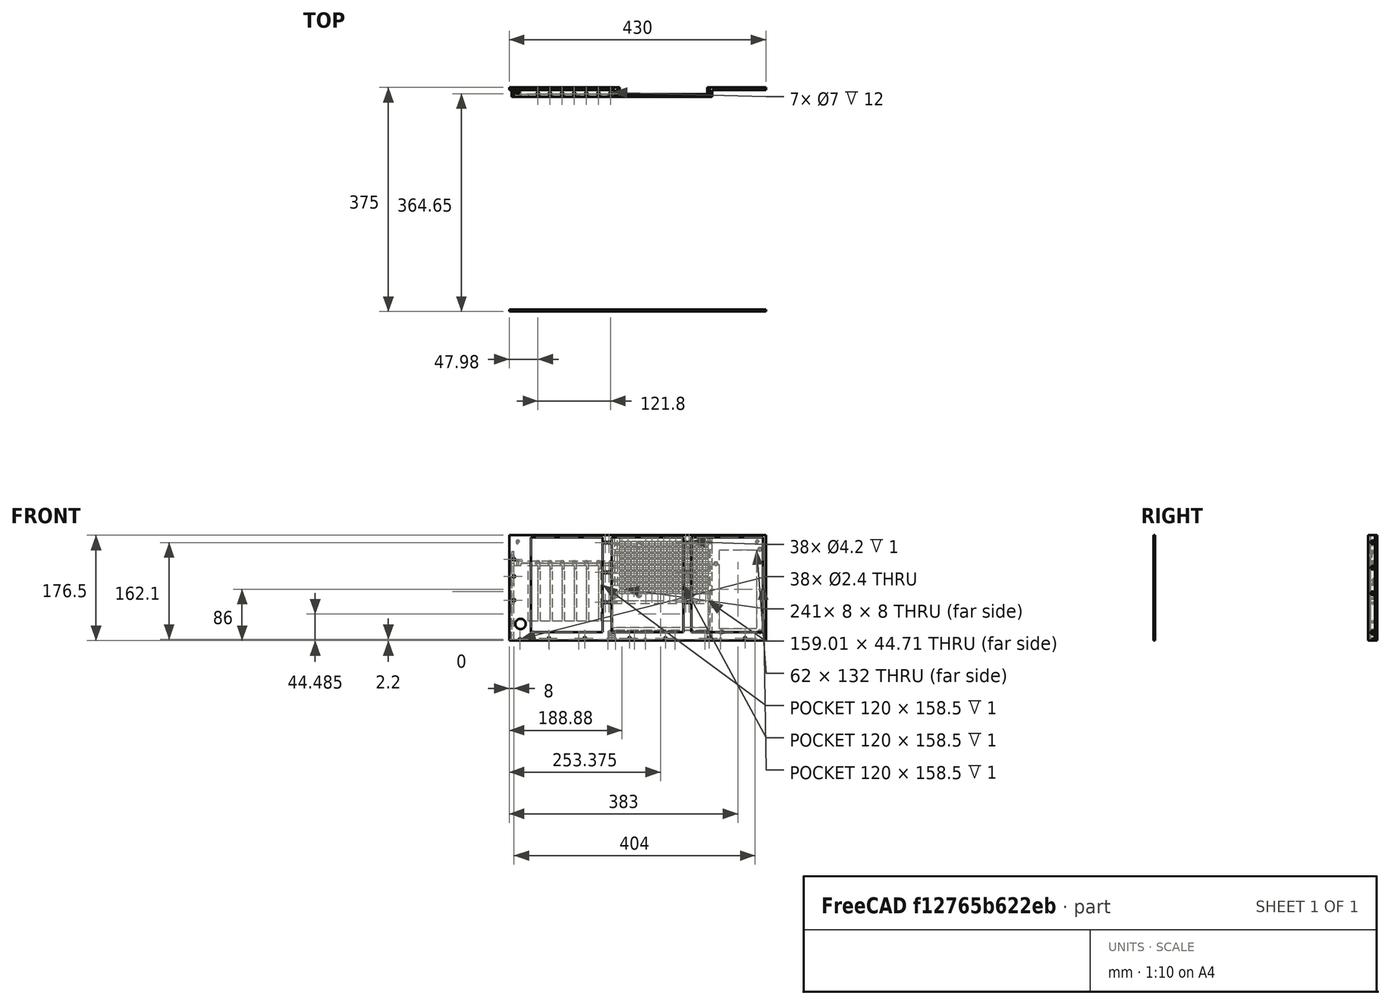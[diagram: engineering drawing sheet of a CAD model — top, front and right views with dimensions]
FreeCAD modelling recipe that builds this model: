
FCSTD DOCUMENT  (FreeCAD 1.0R39109 (Git))
Label: case-wrong-motherboard-height
License: Creative Commons Attribution-NonCommercial-ShareAlike 4.0
LicenseURL: https://creativecommons.org/licenses/by-nc-sa/4.0/
objects: Sketcher::SketchObject×78, Part::FeaturePython×52, PartDesign::Pocket×33, PartDesign::Hole×29, PartDesign::Body×15, PartDesign::FeatureBase×14, PartDesign::Pad×13, Part::Extrusion×11, App::DocumentObjectGroup×10, Part::Part2DObjectPython×6, PartDesign::LinearPattern×2, Spreadsheet::Sheet×1, PartDesign::MultiTransform×1, PartDesign::Fillet×1
note: 502 computed .brp shape members not serialized (recipe doc carries the construction recipe); baked Part::Feature solids carry a one-line shape summary decoded from their .brp

FEATURE [Sketcher::SketchObject] Sketch
  ArcFitTolerance = 1e-06
  AttachmentSupport = -> [XY_Plane]
  FullyConstrained = true
  MakeInternals = false
  MapMode = 5
  expr: Constraints[8] = Spreadsheet.width
  expr: Constraints[9] = Spreadsheet.depth
  sketch-geometry (4):
    g0: LineSegment StartX=-215 StartY=187.5 StartZ=0 EndX=-215 EndY=-187.5 EndZ=0
    g1: LineSegment StartX=-215 StartY=-187.5 StartZ=0 EndX=215 EndY=-187.5 EndZ=0
    g2: LineSegment StartX=215 StartY=-187.5 StartZ=0 EndX=215 EndY=187.5 EndZ=0
    g3: LineSegment StartX=215 StartY=187.5 StartZ=0 EndX=-215 EndY=187.5 EndZ=0
  constraints (11):
    c: Coincident(g0,g1)
    c: Coincident(g1,g2)
    c: Coincident(g2,g3)
    c: Coincident(g3,g0)
    c: Vertical(g0)
    c: Vertical(g2)
    c: Horizontal(g1)
    c: Horizontal(g3)
    c: Distance(g0,g2) = 430
    c: Distance(g1,g3) = 375
    c: Symmetric(g2,g0,g-1)
FEATURE [PartDesign::Pad] Pad  label="bottom"
  Direction = (0,0,1)
  Length = 8
  Length2 = 10
  Profile = -> Sketch
  ReferenceAxis = -> Sketch [N_Axis]
  Refine = true
  Suppressed = false
  Type = 0
  expr: Length = Spreadsheet.bottom_thickness
FEATURE [Spreadsheet::Sheet] Spreadsheet
  cells = A1='Width; B1(width)==430 mm; A2='Depth; B2(depth)==375 mm; A3='Rear wall height; B3(rear_wall_height)==176.5 mm; A4='Side walls height; B4(side_walls_height)==172.5 mm; A5='Front wall height; B5(front_wall_height)==176.5 mm; A6='Bottom thickness; B6(bottom_thickness)==8 mm; A7='Wall thickness; B7(wall_thickness)==4 mm; A8='Front wall thickness; B8(front_wall_thickness)==3 mm; A9='Motherboard left padding; B9(motherboard_left_padding)==6.5 mm; A10='Motherboard right padding; B10(motherboard_right_padding)==6.5 mm; A11='Motherboard front padding; B11(motherboard_front_padding)==6.35 mm; A12='Motherboard rear padding; B12(motherboard_rear_padding)==1.65 mm; A13='Motherboard width; B13(motherboard_width)==305 mm; A14='Motherboard depth; B14(motherboard_depth)==244 mm; A15='Motherboard standoff height; B15(motherboard_standoff_height)==6.5 mm; A16='Side fan thickness; B16(side_fan_thickness)==15 mm; A17='Chassis stiffening ribs height; B17(cChassis_stiffening_ribs_height)==10 mm; A18='PCIE begin; B18(pcie_begin)==160.8 mm; A19='PCIE end; B19(pcie_end)==298.6 mm; A20='PCIE center of first screw; B20(pcie_center_of_first_screw)==144.4 mm; C20='The location of the last PCIE tab screw hole from the left edge of an ATX motherboard; A21='PCIE tab depth; B21(pcie_tab_depth)==11.43 mm; D21='PCI Express™\nCard Electromechanical\nSpecification\nRevision 1.1; E21='Figure 6-4: Standard Add-in Card I/O Bracket; A22='PCIE bracket height; B22(pcie_bracket_height)=93.6; A23='PCIE motherboard thickness; B23(pcie_motherboard_thickness)==1.57 mm; D23='PCI Express™\nCard Electromechanical\nSpecification\nRevision 1.1; A24='PCIE finger bottom to motherboard top; B24(pcie_finger_bottom_to_motherboard_top)==7.9 mm; D24='PCI Express™\nCard Electromechanical\nSpecification\nRevision 1.1; E24='Figure 6-15: Card Assembled in Connector; A25='PCIE finger bottom to mounting tab bottom; B25(pcie_finger_bottom_to_mounting_tab_bottom)==100.36 mm; D25='PCI Express™\nCard Electromechanical\nSpecification\nRevision 1.1; E25='Figure 6-2: Standard Height PCI Express Add-in Card with the I/O Bracket and Card\nRetainer; A26='PCIE opening height from motherboard bottom; B26(pcie_opening_height_from_motherboard_bottom)==pcie_motherboard_thickness + pcie_finger_bottom_to_motherboard_top + pcie_finger_bottom_to_mounting_tab_bottom; C26='calculated; A27='PCIE opening from motherboard bottom; B27(pcie_opening_from_motherboard_bottom)==8.1 mm; A28='PCIE tab bottom padding; B28(pcie_tab_bottom_padding)==0.5 mm; A29='PCIE opening width; B29(pcie_opening_width)==15.9 mm; A30='PCIE spacing; B30(pcie_spacing)==4.4 mm; A31='PCIE opening distance from motherboard edge; B31(pcie_opening_distance_from_motherboard_edge)==6.4 mm; A32='PCIE fastener distance from bracket; B32(pcie_fastener_distance_from_bracket)==5.08 mm; A33='PCIE fastener distance from motherboard edge; B33(pcie_fastener_distance_from_motherboard_edge)==22.48 mm; A34='PCIE fastener spacing; B34(pcie_fastener_spacing)==20.3 mm; A35='IO cutout width; B35(io_cutout_width)==158.75 mm; A36='IO cutout height; B36(io_cutout_height)==44.45 mm; A37='IO cutout keepout zone; B37(io_cutout_keepout_zone)==2.5 mm; A38='IO cutout extra size; B38(io_cutout_extra_size)==0.13 mm; A39='IO cutout bottom to motherboard top; B39(io_cutout_bottom_to_motherboard_top)==3.81 mm; A40='ATX PSU width; B40(atx_psu_width)==150 mm; A41='ATX PSU height; B41(atx_psu_height)==86 mm; A42='ATX PSU depth; B42(atx_psu_depth)==170 mm; A43='Fan mounting hole diameter; B43(fan_mounting_hole_diameter)==4.2 mm; C43='Noctua seems to be using M5 screws which have 4.2. Arctic mentions 4.3. I have seen 4.4 in some drawings. Go figure :p; A44='PCIE mounting hole size; B44(pcie_mounting_hole_size)==3.5 mm; A46='Magnet diameter; B46(magnet_diameter)==6.05 mm; A47='Magnet thickness; B47(magnet_thickness)==3.05 mm; A49='Distance to top support screw; B49(distance_to_top_support_screw)==2.5 + 4 + 3 + 0.5; C49='Distance from the top of the wall to the top support screw
FEATURE [Sketcher::SketchObject] Sketch001
  ArcFitTolerance = 1e-06
  AttachmentSupport = -> [Pad]
  ExternalGeometry = -> [Pad]
  FullyConstrained = true
  MakeInternals = false
  MapMode = 5
  Placement = pos=(0,0,8) rot=(0,0,1;0rad)
  expr: Constraints[13] = Spreadsheet.wall_thickness
  expr: Constraints[14] = Spreadsheet.wall_thickness
  expr: Constraints[16] = Spreadsheet.front_wall_thickness
  expr: Constraints[17] = Spreadsheet.front_wall_thickness
  expr: Constraints[21] = Spreadsheet.wall_thickness
  expr: Constraints[23] = Spreadsheet.wall_thickness
  sketch-geometry (8):
    g0: LineSegment StartX=-215 StartY=183.5 StartZ=0 EndX=-215 EndY=-184.5 EndZ=0
    g1: LineSegment StartX=-215 StartY=-184.5 StartZ=0 EndX=-211 EndY=-184.5 EndZ=0
    g2: LineSegment StartX=-211 StartY=-184.5 StartZ=0 EndX=-211 EndY=183.5 EndZ=0
    g3: LineSegment StartX=-211 StartY=183.5 StartZ=0 EndX=-215 EndY=183.5 EndZ=0
    g4: LineSegment StartX=215 StartY=183.5 StartZ=0 EndX=211 EndY=183.5 EndZ=0
    g5: LineSegment StartX=211 StartY=183.5 StartZ=0 EndX=211 EndY=-184.5 EndZ=0
    g6: LineSegment StartX=211 StartY=-184.5 StartZ=0 EndX=215 EndY=-184.5 EndZ=0
    g7: LineSegment StartX=215 StartY=-184.5 StartZ=0 EndX=215 EndY=183.5 EndZ=0
  constraints (24):
    c: Coincident(g0,g1)
    c: Coincident(g1,g2)
    c: Coincident(g2,g3)
    c: Coincident(g3,g0)
    c: Vertical(g2)
    c: Horizontal(g1)
    c: Horizontal(g3)
    c: Coincident(g5,g6)
    c: Coincident(g6,g7)
    c: Coincident(g7,g4)
    c: Horizontal(g4)
    c: Horizontal(g6)
    c: Vertical(g5)
    c: Distance(g4,g4) = 4
    c: DistanceX(g0,g2) = 4
    c: PointOnObject(g6,g-5)
    c: DistanceY(g-5,g6) = 3
    c: DistanceY(g-4,g0) = 3
    c: PointOnObject(g0,g-4)
    c: Coincident(g4,g5)
    c: PointOnObject(g4,g-5)
    c: DistanceY(g4,g-5) = 4
    c: PointOnObject(g0,g-4)
    c: DistanceY(g0,g-4) = 4
FEATURE [PartDesign::Pad] Pad001  label="side walls"
  BaseFeature = -> Pad
  Direction = (0,0,1)
  Length = 164.5
  Length2 = 10
  Profile = -> Sketch001
  ReferenceAxis = -> Sketch001 [N_Axis]
  Refine = true
  Suppressed = false
  Type = 0
  expr: Length = Spreadsheet.side_walls_height - Spreadsheet.bottom_thickness
FEATURE [Sketcher::SketchObject] Sketch002
  ArcFitTolerance = 1e-06
  AttachmentSupport = -> [Pad001]
  ExternalGeometry = -> [Pad]
  FullyConstrained = true
  MakeInternals = false
  MapMode = 5
  Placement = pos=(0,0,8) rot=(0,0,1;0rad)
  expr: Constraints[16] = Spreadsheet.atx_psu_height + Spreadsheet.wall_thickness + 0.1 mm
  expr: Constraints[17] = Spreadsheet.wall_thickness
  expr: Constraints[22] = Spreadsheet.pcie_tab_depth + Spreadsheet.wall_thickness
  expr: Constraints[6] = Spreadsheet.wall_thickness
  sketch-geometry (8):
    g0: LineSegment StartX=120.9 StartY=176.07 StartZ=0 EndX=-215 EndY=176.07 EndZ=0
    g1: LineSegment StartX=-215 StartY=176.07 StartZ=0 EndX=-215 EndY=172.07 EndZ=0
    g2: LineSegment StartX=-215 StartY=172.07 StartZ=0 EndX=124.9 EndY=172.07 EndZ=0
    g3: LineSegment StartX=124.9 StartY=172.07 StartZ=0 EndX=124.9 EndY=183.5 EndZ=0
    g4: LineSegment StartX=120.9 StartY=176.07 StartZ=0 EndX=120.9 EndY=187.5 EndZ=0
    g5: LineSegment StartX=120.9 StartY=187.5 StartZ=0 EndX=215 EndY=187.5 EndZ=0
    g6: LineSegment StartX=215 StartY=187.5 StartZ=0 EndX=215 EndY=183.5 EndZ=0
    g7: LineSegment StartX=215 StartY=183.5 StartZ=0 EndX=124.9 EndY=183.5 EndZ=0
  constraints (23):
    c: Coincident(g0,g1)
    c: Coincident(g1,g2)
    c: Coincident(g2,g3)
    c: Horizontal(g0)
    c: Horizontal(g2)
    c: Vertical(g1)
    c: DistanceY(g1,g0) = 4
    c: Coincident(g0,g4)
    c: Vertical(g4)
    c: Coincident(g4,g5)
    c: Coincident(g5,g6)
    c: Coincident(g6,g7)
    c: Horizontal(g7)
    c: Coincident(g7,g3)
    c: Vertical(g3)
    c: Equal(g1,g6)
    c: DistanceX(g3,g6) = 90.1
    c: DistanceX(g4,g3) = 4
    c: PointOnObject(g0,g-3)
    c: Horizontal(g5)
    c: Coincident(g5,g-4)
    c: PointOnObject(g6,g-5)
    c: Distance(g2,g-4) = 15.43
FEATURE [PartDesign::Pad] Pad002  label="rear wall"
  BaseFeature = -> Pad001
  Direction = (0,0,1)
  Length = 121.83
  Length2 = 10
  Profile = -> Sketch002
  ReferenceAxis = -> Sketch002 [N_Axis]
  Refine = true
  Suppressed = false
  Type = 0
  expr: Length = Spreadsheet.cChassis_stiffening_ribs_height + Spreadsheet.motherboard_standoff_height + Spreadsheet.pcie_opening_height_from_motherboard_bottom - Spreadsheet.pcie_tab_bottom_padding - Spreadsheet.wall_thickness
FEATURE [Sketcher::SketchObject] Sketch003
  ArcFitTolerance = 1e-06
  AttachmentSupport = -> [Pad002]
  ExternalGeometry = -> [Pad002]
  FullyConstrained = true
  MakeInternals = false
  MapMode = 5
  Placement = pos=(0,0,129.83) rot=(0,0,1;0rad)
  expr: Constraints[9] = Spreadsheet.side_fan_thickness + Spreadsheet.motherboard_left_padding + Spreadsheet.pcie_center_of_first_screw + 2 * Spreadsheet.pcie_mounting_hole_size + Spreadsheet.wall_thickness
  sketch-geometry (7):
    g0: LineSegment StartX=-211 StartY=183.5 StartZ=0 EndX=-211 EndY=172.07 EndZ=0
    g1: LineSegment StartX=-211 StartY=172.07 StartZ=0 EndX=-34.1 EndY=172.07 EndZ=0
    g2: LineSegment StartX=-34.1 StartY=187.5 StartZ=0 EndX=-211 EndY=187.5 EndZ=0
    g3: LineSegment StartX=-34.1 StartY=187.5 StartZ=0 EndX=-34.1 EndY=172.07 EndZ=0
    g4: LineSegment StartX=-215 StartY=183.5 StartZ=0 EndX=-211 EndY=183.5 EndZ=0
    g5: LineSegment StartX=-211 StartY=187.5 StartZ=0 EndX=-215 EndY=187.5 EndZ=0
    g6: LineSegment StartX=-215 StartY=187.5 StartZ=0 EndX=-215 EndY=183.5 EndZ=0
  constraints (17):
    c: Coincident(g0,g1)
    c: Vertical(g0)
    c: Horizontal(g1)
    c: Horizontal(g2)
    c: Coincident(g2,g-3)
    c: PointOnObject(g1,g-4)
    c: Coincident(g3,g2)
    c: Coincident(g3,g1)
    c: Vertical(g3)
    c: DistanceX(g2,g2) = 176.9
    c: Coincident(g5,g6)
    c: Coincident(g6,g4)
    c: Coincident(g4,g-5)
    c: Coincident(g5,g-6)
    c: Coincident(g4,g-5)
    c: Coincident(g0,g4)
    c: Coincident(g2,g5)
FEATURE [PartDesign::Pad] Pad003  label="pcie flange"
  BaseFeature = -> Pad002
  Direction = (0,0,1)
  Length = 4
  Length2 = 10
  Profile = -> Sketch003
  ReferenceAxis = -> Sketch003 [N_Axis]
  Refine = true
  Suppressed = false
  Type = 0
  expr: Length = Spreadsheet.wall_thickness
FEATURE [Sketcher::SketchObject] Sketch004
  ArcFitTolerance = 1e-06
  AttachmentSupport = -> [Pad003]
  ExternalGeometry = -> [Pad003]
  FullyConstrained = true
  MakeInternals = false
  MapMode = 5
  Placement = pos=(0,176.07,0) rot=(0,0.707107,0.707107;3.14159rad)
  expr: Constraints[100] = Spreadsheet.io_cutout_extra_size
  expr: Constraints[106] = Spreadsheet.io_cutout_extra_size
  expr: Constraints[107] = Spreadsheet.io_cutout_extra_size
  expr: Constraints[108] = Spreadsheet.io_cutout_extra_size
  expr: Constraints[118] = Spreadsheet.pcie_opening_from_motherboard_bottom
  expr: Constraints[119] = Spreadsheet.pcie_bracket_height
  expr: Constraints[65] = Spreadsheet.pcie_opening_width
  expr: Constraints[66] = Spreadsheet.pcie_spacing
  expr: Constraints[67] = Spreadsheet.pcie_spacing
  expr: Constraints[68] = Spreadsheet.pcie_spacing
  expr: Constraints[69] = Spreadsheet.pcie_spacing
  expr: Constraints[70] = Spreadsheet.pcie_spacing
  expr: Constraints[71] = Spreadsheet.pcie_spacing
  expr: Constraints[80] = Spreadsheet.io_cutout_width
  expr: Constraints[81] = Spreadsheet.io_cutout_height
  expr: Constraints[82] = Spreadsheet.pcie_spacing
  expr: Constraints[91] = Spreadsheet.motherboard_width
  expr: Constraints[92] = Spreadsheet.pcie_motherboard_thickness
  expr: Constraints[93] = Spreadsheet.cChassis_stiffening_ribs_height + Spreadsheet.motherboard_standoff_height
  expr: Constraints[94] = Spreadsheet.io_cutout_bottom_to_motherboard_top
  expr: Constraints[95] = Spreadsheet.side_fan_thickness + Spreadsheet.motherboard_left_padding
  expr: Constraints[96] = Spreadsheet.pcie_opening_distance_from_motherboard_edge
  sketch-geometry (40):
    g0: LineSegment StartX=167.2 StartY=126.2 StartZ=0 EndX=167.2 EndY=32.6 EndZ=0
    g1: LineSegment StartX=183.1 StartY=32.6 StartZ=0 EndX=183.1 EndY=126.2 EndZ=0
    g2: LineSegment StartX=183.1 StartY=126.2 StartZ=0 EndX=167.2 EndY=126.2 EndZ=0
    g3: LineSegment StartX=146.9 StartY=126.2 StartZ=0 EndX=146.9 EndY=32.6 EndZ=0
    g4: LineSegment StartX=146.9 StartY=32.6 StartZ=0 EndX=162.8 EndY=32.6 EndZ=0
    g5: LineSegment StartX=162.8 StartY=32.6 StartZ=0 EndX=162.8 EndY=126.2 EndZ=0
    g6: LineSegment StartX=162.8 StartY=126.2 StartZ=0 EndX=146.9 EndY=126.2 EndZ=0
    g7: LineSegment StartX=106.3 StartY=126.2 StartZ=0 EndX=106.3 EndY=32.6 EndZ=0
    g8: LineSegment StartX=106.3 StartY=32.6 StartZ=0 EndX=122.2 EndY=32.6 EndZ=0
    g9: LineSegment StartX=122.2 StartY=32.6 StartZ=0 EndX=122.2 EndY=126.2 EndZ=0
    g10: LineSegment StartX=122.2 StartY=126.2 StartZ=0 EndX=106.3 EndY=126.2 EndZ=0
    g11: LineSegment StartX=126.6 StartY=126.2 StartZ=0 EndX=126.6 EndY=32.6 EndZ=0
    g12: LineSegment StartX=126.6 StartY=32.6 StartZ=0 EndX=142.5 EndY=32.6 EndZ=0
    g13: LineSegment StartX=142.5 StartY=32.6 StartZ=0 EndX=142.5 EndY=126.2 EndZ=0
    g14: LineSegment StartX=142.5 StartY=126.2 StartZ=0 EndX=126.6 EndY=126.2 EndZ=0
    g15: LineSegment StartX=101.9 StartY=126.2 StartZ=0 EndX=86 EndY=126.2 EndZ=0
    g16: LineSegment StartX=86 StartY=126.2 StartZ=0 EndX=86 EndY=32.6 EndZ=0
    g17: LineSegment StartX=86 StartY=32.6 StartZ=0 EndX=101.9 EndY=32.6 EndZ=0
    g18: LineSegment StartX=101.9 StartY=32.6 StartZ=0 EndX=101.9 EndY=126.2 EndZ=0
    g19: LineSegment StartX=81.6 StartY=126.2 StartZ=0 EndX=65.7 EndY=126.2 EndZ=0
    g20: LineSegment StartX=65.7 StartY=126.2 StartZ=0 EndX=65.7 EndY=32.6 EndZ=0
    g21: LineSegment StartX=65.7 StartY=32.6 StartZ=0 EndX=81.6 EndY=32.6 EndZ=0
    g22: LineSegment StartX=81.6 StartY=32.6 StartZ=0 EndX=81.6 EndY=126.2 EndZ=0
    g23: LineSegment StartX=61.3 StartY=126.2 StartZ=0 EndX=45.4 EndY=126.2 EndZ=0
    g24: LineSegment StartX=45.4 StartY=126.2 StartZ=0 EndX=45.4 EndY=32.6 EndZ=0
    g25: LineSegment StartX=45.4 StartY=32.6 StartZ=0 EndX=61.3 EndY=32.6 EndZ=0
    g26: LineSegment StartX=61.3 StartY=32.6 StartZ=0 EndX=61.3 EndY=126.2 EndZ=0
    g27: LineSegment [constr] StartX=41 StartY=66.71 StartZ=0 EndX=-117.75 EndY=66.71 EndZ=0
    g28: LineSegment [constr] StartX=-117.75 StartY=66.71 StartZ=0 EndX=-117.75 EndY=22.26 EndZ=0
    g29: LineSegment [constr] StartX=-117.75 StartY=22.26 StartZ=0 EndX=41 EndY=22.26 EndZ=0
    g30: LineSegment [constr] StartX=41 StartY=22.26 StartZ=0 EndX=41 EndY=66.71 EndZ=0
    g31: LineSegment [constr] StartX=-115.5 StartY=26.07 StartZ=0 EndX=-115.5 EndY=24.5 EndZ=0
    g32: LineSegment [constr] StartX=-115.5 StartY=24.5 StartZ=0 EndX=189.5 EndY=24.5 EndZ=0
    g33: LineSegment [constr] StartX=189.5 StartY=24.5 StartZ=0 EndX=189.5 EndY=26.07 EndZ=0
    g34: LineSegment [constr] StartX=189.5 StartY=26.07 StartZ=0 EndX=-115.5 EndY=26.07 EndZ=0
    g35: LineSegment StartX=41.13 StartY=22.13 StartZ=0 EndX=41.13 EndY=66.84 EndZ=0
    g36: LineSegment StartX=41.13 StartY=66.84 StartZ=0 EndX=-117.88 EndY=66.84 EndZ=0
    g37: LineSegment StartX=-117.88 StartY=66.84 StartZ=0 EndX=-117.88 EndY=22.13 EndZ=0
    g38: LineSegment StartX=-117.88 StartY=22.13 StartZ=0 EndX=41.13 EndY=22.13 EndZ=0
    g39: LineSegment StartX=167.2 StartY=32.6 StartZ=0 EndX=183.1 EndY=32.6 EndZ=0
  constraints (120):
    c: Coincident(g1,g2)
    c: Coincident(g2,g0)
    c: Vertical(g0)
    c: Vertical(g1)
    c: Horizontal(g2)
    c: Coincident(g3,g4)
    c: Coincident(g4,g5)
    c: Coincident(g5,g6)
    c: Coincident(g6,g3)
    c: Vertical(g3)
    c: Vertical(g5)
    c: Horizontal(g4)
    c: Horizontal(g6)
    c: Coincident(g7,g8)
    c: Coincident(g8,g9)
    c: Coincident(g9,g10)
    c: Coincident(g10,g7)
    c: Vertical(g7)
    c: Vertical(g9)
    c: Horizontal(g8)
    c: Horizontal(g10)
    c: Coincident(g11,g12)
    c: Coincident(g12,g13)
    c: Coincident(g13,g14)
    c: Coincident(g14,g11)
    c: Vertical(g11)
    c: Vertical(g13)
    c: Horizontal(g12)
    c: Horizontal(g14)
    c: Coincident(g15,g16)
    c: Coincident(g16,g17)
    c: Coincident(g17,g18)
    c: Coincident(g18,g15)
    c: Horizontal(g15)
    c: Horizontal(g17)
    c: Vertical(g16)
    c: Vertical(g18)
    c: Coincident(g19,g20)
    c: Coincident(g20,g21)
    c: Coincident(g21,g22)
    c: Coincident(g22,g19)
    c: Horizontal(g19)
    c: Horizontal(g21)
    c: Vertical(g20)
    c: Vertical(g22)
    c: Coincident(g23,g24)
    c: Coincident(g24,g25)
    c: Coincident(g25,g26)
    c: Coincident(g26,g23)
    c: Horizontal(g23)
    c: Horizontal(g25)
    c: Vertical(g24)
    c: Vertical(g26)
    c: Equal(g2,g6)
    c: Equal(g23,g19)
    c: Equal(g19,g15)
    c: Equal(g15,g10)
    c: Equal(g10,g14)
    c: Equal(g14,g6)
    c: Horizontal(g0,g5)
    c: Horizontal(g3,g13)
    c: Horizontal(g11,g9)
    c: Horizontal(g7,g15)
    c: Horizontal(g15,g19)
    c: Horizontal(g19,g23)
    c: DistanceX(g0,g1) = 15.9
    c: DistanceX(g4,g0) = 4.4
    c: DistanceX(g12,g3) = 4.4
    c: DistanceX(g8,g11) = 4.4
    c: DistanceX(g17,g7) = 4.4
    c: DistanceX(g21,g16) = 4.4
    c: DistanceX(g25,g20) = 4.4
    c: Coincident(g27,g28)
    c: Coincident(g28,g29)
    c: Coincident(g29,g30)
    c: Coincident(g30,g27)
    c: Horizontal(g27)
    c: Horizontal(g29)
    c: Vertical(g28)
    c: Vertical(g30)
    c: DistanceX(g27,g27) = 158.75
    c: DistanceY(g29,g27) = 44.45
    c: DistanceX(g29,g24) = 4.4
    c: Coincident(g31,g32)
    c: Coincident(g32,g33)
    c: Coincident(g33,g34)
    c: Coincident(g34,g31)
    c: Vertical(g31)
    c: Vertical(g33)
    c: Horizontal(g32)
    c: Horizontal(g34)
    c: DistanceX(g31,g33) = 305
    c: DistanceY(g31,g31) = 1.57
    c: Distance(g31,g-4) = 16.5
    c: DistanceY(g28,g31) = 3.81
    c: Distance(g33,g-3) = 21.5
    c: Distance(g33,g1) = 6.4
    c: Parallel(g35,g30)
    c: Parallel(g36,g27)
    c: Parallel(g37,g28)
    c: Distance(g38,g29) = 0.13
    c: Coincident(g37,g38)
    c: Coincident(g36,g37)
    c: Coincident(g35,g38)
    c: Coincident(g35,g36)
    c: Horizontal(g38)
    c: Distance(g27,g36) = 0.13
    c: DistanceX(g36,g27) = 0.13
    c: DistanceX(g29,g35) = 0.13
    c: Coincident(g39,g0)
    c: Coincident(g39,g1)
    c: Horizontal(g39)
    c: Horizontal(g0,g4)
    c: Horizontal(g3,g12)
    c: Horizontal(g11,g8)
    c: Horizontal(g7,g17)
    c: Horizontal(g16,g21)
    c: Horizontal(g20,g25)
    c: Distance(g32,g39) = 8.1
    c: DistanceY(g1,g1) = 93.6
FEATURE [PartDesign::Pocket] Pocket  label="rear cutouts"
  BaseFeature = -> Pad003
  Direction = (0,-1,2e-16)
  Length = 4
  Length2 = 5
  Profile = -> Sketch004
  ReferenceAxis = -> Sketch004 [N_Axis]
  Refine = true
  Suppressed = false
  Type = 0
  expr: Length = Spreadsheet.wall_thickness
FEATURE [Sketcher::SketchObject] Sketch005
  ArcFitTolerance = 1e-06
  AttachmentSupport = -> [Pad002]
  FullyConstrained = true
  MakeInternals = false
  MapMode = 5
  Placement = pos=(0,187.5,0) rot=(0,0.707107,0.707107;3.14159rad)
  sketch-geometry (12):
    g0: LineSegment [constr] StartX=-125 StartY=158 StartZ=0 EndX=-211 EndY=158 EndZ=0
    g1: LineSegment [constr] StartX=-211 StartY=158 StartZ=0 EndX=-211 EndY=8 EndZ=0
    g2: LineSegment [constr] StartX=-211 StartY=8 StartZ=0 EndX=-125 EndY=8 EndZ=0
    g3: LineSegment [constr] StartX=-125 StartY=8 StartZ=0 EndX=-125 EndY=158 EndZ=0
    g4: Circle CenterX=-205 CenterY=152 CenterZ=0 NormalX=0 NormalY=0 NormalZ=1 AngleXU=0 Radius=1.7525
    g5: Circle CenterX=-131 CenterY=128 CenterZ=0 NormalX=0 NormalY=0 NormalZ=1 AngleXU=0 Radius=1.7525
    g6: Circle CenterX=-205 CenterY=14 CenterZ=0 NormalX=0 NormalY=0 NormalZ=1 AngleXU=0 Radius=1.7525
    g7: Circle CenterX=-141 CenterY=14 CenterZ=0 NormalX=0 NormalY=0 NormalZ=1 AngleXU=0 Radius=1.7525
    g8: LineSegment StartX=-199 StartY=152 StartZ=0 EndX=-199 EndY=20 EndZ=0
    g9: LineSegment StartX=-199 StartY=20 StartZ=0 EndX=-137 EndY=20 EndZ=0
    g10: LineSegment StartX=-137 StartY=20 StartZ=0 EndX=-137 EndY=152 EndZ=0
    g11: LineSegment StartX=-137 StartY=152 StartZ=0 EndX=-199 EndY=152 EndZ=0
  constraints (35):
    c: Coincident(g0,g1)
    c: Coincident(g1,g2)
    c: Coincident(g2,g3)
    c: Coincident(g3,g0)
    c: Horizontal(g0)
    c: Horizontal(g2)
    c: Vertical(g1)
    c: Vertical(g3)
    c: DistanceX(g0,g0) = 86
    c: Distance(g0,g1) = 150
    c: DistanceY(g6,g4) = 138
    c: DistanceY(g7,g5) = 114
    c: DistanceX(g6,g7) = 64
    c: Horizontal(g7,g6)
    c: Vertical(g4,g6)
    c: Coincident(g1,g-4)
    c: DistanceY(g2,g7) = 6
    c: Distance(g7,g3) = 16
    c: Distance(g5,g3) = 6
    c: Diameter(g7) = 3.505
    c: Equal(g7,g6)
    c: Equal(g6,g4)
    c: Equal(g4,g5)
    c: Coincident(g8,g9)
    c: Coincident(g9,g10)
    c: Coincident(g10,g11)
    c: Coincident(g11,g8)
    c: Vertical(g8)
    c: Vertical(g10)
    c: Horizontal(g9)
    c: Horizontal(g11)
    c: Distance(g0,g11) = 6
    c: Distance(g8,g1) = 12
    c: Distance(g3,g10) = 12
    c: Distance(g2,g9) = 12
FEATURE [Sketcher::SketchObject] Sketch006
  ArcFitTolerance = 1e-06
  AttachmentSupport = -> [Pocket]
  ExternalGeometry = -> [Pocket,Pad003]
  FullyConstrained = true
  MakeInternals = false
  MapMode = 5
  Placement = pos=(0,0,133.83) rot=(0,0,1;0rad)
  expr: Constraints[10] = Spreadsheet.wall_thickness
  sketch-geometry (12):
    g0: LineSegment StartX=-215 StartY=187.5 StartZ=0 EndX=-215 EndY=183.5 EndZ=0
    g1: LineSegment StartX=-215 StartY=183.5 StartZ=0 EndX=-38.1 EndY=183.5 EndZ=0
    g2: LineSegment StartX=-38.1 StartY=172.07 StartZ=0 EndX=124.9 EndY=172.07 EndZ=0
    g3: LineSegment StartX=124.9 StartY=172.07 StartZ=0 EndX=124.9 EndY=183.5 EndZ=0
    g4: LineSegment StartX=120.9 StartY=176.07 StartZ=0 EndX=-34.1 EndY=176.07 EndZ=0
    g5: LineSegment StartX=-38.1 StartY=183.5 StartZ=0 EndX=-38.1 EndY=172.07 EndZ=0
    g6: LineSegment StartX=-34.1 StartY=176.07 StartZ=0 EndX=-34.1 EndY=187.5 EndZ=0
    g7: LineSegment StartX=120.9 StartY=176.07 StartZ=0 EndX=120.9 EndY=187.5 EndZ=0
    g8: LineSegment StartX=120.9 StartY=187.5 StartZ=0 EndX=215 EndY=187.5 EndZ=0
    g9: LineSegment StartX=215 StartY=187.5 StartZ=0 EndX=215 EndY=183.5 EndZ=0
    g10: LineSegment StartX=215 StartY=183.5 StartZ=0 EndX=124.9 EndY=183.5 EndZ=0
    g11: LineSegment StartX=-215 StartY=187.5 StartZ=0 EndX=-34.1 EndY=187.5 EndZ=0
  constraints (28):
    c: Coincident(g0,g1)
    c: Horizontal(g1)
    c: Coincident(g2,g3)
    c: Horizontal(g2)
    c: Horizontal(g4)
    c: Coincident(g1,g5)
    c: Vertical(g5)
    c: Coincident(g4,g6)
    c: Vertical(g6)
    c: Coincident(g2,g5)
    c: Distance(g5,g6) = 4
    c: Coincident(g-4,g4)
    c: Coincident(g-5,g2)
    c: Coincident(g3,g-5)
    c: Coincident(g4,g7)
    c: Coincident(g7,g-4)
    c: Coincident(g7,g8)
    c: Coincident(g8,g9)
    c: Coincident(g9,g-6)
    c: Coincident(g9,g10)
    c: Coincident(g10,g3)
    c: Vertical(g9)
    c: Horizontal(g8)
    c: Coincident(g11,g-7)
    c: Coincident(g11,g6)
    c: Coincident(g11,g0)
    c: Coincident(g0,g-8)
    c: Coincident(g-7,g6)
FEATURE [PartDesign::Pad] Pad004  label="rear wall top part"
  BaseFeature = -> Pocket
  Direction = (0,0,1)
  Length = 42.67
  Length2 = 4
  Profile = -> Sketch006
  ReferenceAxis = -> Sketch006 [N_Axis]
  Refine = true
  Suppressed = false
  Type = 4
  expr: Length = Spreadsheet.rear_wall_height - Spreadsheet.cChassis_stiffening_ribs_height - Spreadsheet.motherboard_standoff_height - Spreadsheet.pcie_opening_height_from_motherboard_bottom + Spreadsheet.pcie_tab_bottom_padding - 2 * Spreadsheet.wall_thickness
  expr: Length2 = <<pcie flange>>.Length
FEATURE [Sketcher::SketchObject] Sketch008
  ArcFitTolerance = 1e-06
  FullyConstrained = true
  MakeInternals = false
  MapMode = 5
  Placement = pos=(0,0,8) rot=(0,0,1;0rad)
  expr: Constraints[10] = Spreadsheet.motherboard_depth
  expr: Constraints[11] = Spreadsheet.motherboard_rear_padding
  expr: Constraints[8] = Spreadsheet.motherboard_width
  expr: Constraints[9] = Spreadsheet.side_fan_thickness + Spreadsheet.motherboard_left_padding
  sketch-geometry (16):
    g0: LineSegment StartX=-189.5 StartY=170.42 StartZ=0 EndX=-189.5 EndY=-73.58 EndZ=0
    g1: LineSegment StartX=-189.5 StartY=-73.58 StartZ=0 EndX=115.5 EndY=-73.58 EndZ=0
    g2: LineSegment StartX=115.5 StartY=-73.58 StartZ=0 EndX=115.5 EndY=170.42 EndZ=0
    g3: LineSegment StartX=115.5 StartY=170.42 StartZ=0 EndX=-189.5 EndY=170.42 EndZ=0
    g4: Circle CenterX=-172.8 CenterY=160.22 CenterZ=0 NormalX=0 NormalY=0 NormalZ=1 AngleXU=0 Radius=1.55
    g5: Circle CenterX=-94.1 CenterY=160.22 CenterZ=0 NormalX=0 NormalY=0 NormalZ=1 AngleXU=0 Radius=1.55
    g6: Circle CenterX=-48.3 CenterY=160.22 CenterZ=0 NormalX=0 NormalY=0 NormalZ=1 AngleXU=0 Radius=1.55
    g7: Circle CenterX=109.1 CenterY=137.42 CenterZ=0 NormalX=0 NormalY=0 NormalZ=1 AngleXU=0 Radius=1.55
    g8: Circle CenterX=-172.8 CenterY=5.32 CenterZ=0 NormalX=0 NormalY=0 NormalZ=1 AngleXU=0 Radius=1.55
    g9: Circle CenterX=-114.4 CenterY=5.32 CenterZ=0 NormalX=0 NormalY=0 NormalZ=1 AngleXU=0 Radius=1.55
    g10: Circle CenterX=-94.1 CenterY=5.32 CenterZ=0 NormalX=0 NormalY=0 NormalZ=1 AngleXU=0 Radius=1.55
    g11: Circle CenterX=-48.3 CenterY=5.32 CenterZ=0 NormalX=0 NormalY=0 NormalZ=1 AngleXU=0 Radius=1.55
    g12: Circle CenterX=109.1 CenterY=5.32 CenterZ=0 NormalX=0 NormalY=0 NormalZ=1 AngleXU=0 Radius=1.55
    g13: Circle CenterX=109.1 CenterY=-67.08 CenterZ=0 NormalX=0 NormalY=0 NormalZ=1 AngleXU=0 Radius=1.55
    g14: Circle CenterX=-172.8 CenterY=-67.08 CenterZ=0 NormalX=0 NormalY=0 NormalZ=1 AngleXU=0 Radius=1.55
    g15: Circle CenterX=-48.3 CenterY=-67.08 CenterZ=0 NormalX=0 NormalY=0 NormalZ=1 AngleXU=0 Radius=1.55
  constraints (48):
    c: Coincident(g0,g1)
    c: Coincident(g1,g2)
    c: Coincident(g2,g3)
    c: Coincident(g3,g0)
    c: Vertical(g0)
    c: Vertical(g2)
    c: Horizontal(g1)
    c: Horizontal(g3)
    c: DistanceX(g0,g2) = 305
    c: Distance(g-3,g0) = 21.5
    c: Distance(g1,g3) = 244
    c: Distance(g0,g-4) = 1.65
    c: Horizontal(g13,g15)
    c: Horizontal(g15,g14)
    c: Horizontal(g12,g11)
    c: Horizontal(g11,g10)
    c: Horizontal(g10,g9)
    c: Horizontal(g9,g8)
    c: Horizontal(g6,g5)
    c: Horizontal(g5,g4)
    c: Vertical(g4,g8)
    c: Vertical(g8,g14)
    c: Vertical(g5,g10)
    c: Vertical(g6,g11)
    c: Vertical(g11,g15)
    c: Vertical(g7,g12)
    c: Vertical(g12,g13)
    c: Equal(g4,g5)
    c: Equal(g5,g6)
    c: Equal(g6,g7)
    c: Equal(g7,g12)
    c: Equal(g12,g11)
    c: Equal(g11,g10)
    c: Equal(g10,g9)
    c: Equal(g9,g8)
    c: Equal(g8,g14)
    c: Equal(g14,g15)
    c: Equal(g15,g13)
    c: Diameter(g4) = 3.1
    c: Distance(g6,g3) = 10.2
    c: Distance(g7,g3) = 33
    c: Distance(g12,g3) = 165.1
    c: Distance(g13,g3) = 237.5
    c: Distance(g13,g2) = 6.4
    c: Distance(g15,g2) = 163.8
    c: Distance(g10,g2) = 209.6
    c: Distance(g9,g2) = 229.9
    c: Distance(g4,g2) = 288.3
FEATURE [Sketcher::SketchObject] Sketch011
  ArcFitTolerance = 1e-06
  FullyConstrained = true
  MakeInternals = false
  MapMode = 5
  Placement = pos=(0,0,133.83) rot=(0,0,1;0rad)
  expr: Constraints[11] = Spreadsheet.pcie_fastener_spacing
  expr: Constraints[12] = Spreadsheet.pcie_fastener_spacing
  expr: Constraints[13] = Spreadsheet.pcie_fastener_spacing
  expr: Constraints[14] = Spreadsheet.pcie_fastener_spacing
  expr: Constraints[15] = Spreadsheet.pcie_fastener_spacing
  expr: Constraints[17] = Spreadsheet.pcie_fastener_spacing
  expr: Constraints[24] = Spreadsheet.pcie_mounting_hole_size
  expr: Constraints[2] = Spreadsheet.pcie_fastener_distance_from_bracket
  expr: Constraints[5] = Spreadsheet.side_fan_thickness + Spreadsheet.motherboard_left_padding + Spreadsheet.pcie_fastener_distance_from_motherboard_edge
  sketch-geometry (8):
    g0: LineSegment [constr] StartX=-211 StartY=177.15 StartZ=0 EndX=-45 EndY=177.15 EndZ=0
    g1: Circle CenterX=-167.02 CenterY=177.15 CenterZ=0 NormalX=0 NormalY=0 NormalZ=1 AngleXU=0 Radius=1.75
    g2: Circle CenterX=-146.72 CenterY=177.15 CenterZ=0 NormalX=0 NormalY=0 NormalZ=1 AngleXU=0 Radius=1.75
    g3: Circle CenterX=-126.42 CenterY=177.15 CenterZ=0 NormalX=0 NormalY=0 NormalZ=1 AngleXU=0 Radius=1.75
    g4: Circle CenterX=-106.12 CenterY=177.15 CenterZ=0 NormalX=0 NormalY=0 NormalZ=1 AngleXU=0 Radius=1.75
    g5: Circle CenterX=-85.82 CenterY=177.15 CenterZ=0 NormalX=0 NormalY=0 NormalZ=1 AngleXU=0 Radius=1.75
    g6: Circle CenterX=-65.52 CenterY=177.15 CenterZ=0 NormalX=0 NormalY=0 NormalZ=1 AngleXU=0 Radius=1.75
    g7: Circle CenterX=-45.22 CenterY=177.15 CenterZ=0 NormalX=0 NormalY=0 NormalZ=1 AngleXU=0 Radius=1.75
  constraints (25):
    c: Horizontal(g0)
    c: PointOnObject(g0,g-4)
    c: Distance(g-3,g0) = 5.08
    c: PointOnObject(g0,g-3)
    c: PointOnObject(g1,g0)
    c: DistanceX(g0,g1) = 43.98
    c: PointOnObject(g2,g0)
    c: PointOnObject(g3,g0)
    c: PointOnObject(g4,g0)
    c: PointOnObject(g5,g0)
    c: PointOnObject(g6,g0)
    c: DistanceX(g1,g2) = 20.3
    c: Distance(g2,g3) = 20.3
    c: DistanceX(g5,g6) = 20.3
    c: DistanceX(g3,g4) = 20.3
    c: DistanceX(g4,g5) = 20.3
    c: PointOnObject(g7,g0)
    c: DistanceX(g6,g7) = 20.3
    c: Equal(g1,g2)
    c: Equal(g2,g3)
    c: Equal(g3,g4)
    c: Equal(g4,g5)
    c: Equal(g5,g6)
    c: Equal(g6,g7)
    c: Diameter(g1) = 3.5
FEATURE [Sketcher::SketchObject] Sketch020
  ArcFitTolerance = 1e-06
  FullyConstrained = true
  MakeInternals = false
  MapMode = 5
  Placement = pos=(215,0,0) rot=(0.57735,0.57735,0.57735;2.0944rad)
  sketch-geometry (4):
    g0: LineSegment StartX=162.07 StartY=156 StartZ=0 EndX=32.07 EndY=156 EndZ=0
    g1: LineSegment StartX=32.07 StartY=156 StartZ=0 EndX=32.07 EndY=10 EndZ=0
    g2: LineSegment StartX=32.07 StartY=10 StartZ=0 EndX=162.07 EndY=10 EndZ=0
    g3: LineSegment StartX=162.07 StartY=10 StartZ=0 EndX=162.07 EndY=156 EndZ=0
  constraints (12):
    c: Coincident(g0,g1)
    c: Coincident(g1,g2)
    c: Coincident(g2,g3)
    c: Coincident(g3,g0)
    c: Horizontal(g0)
    c: Horizontal(g2)
    c: Vertical(g1)
    c: Vertical(g3)
    c: DistanceY(g2,g0) = 146
    c: DistanceX(g0,g0) = 130
    c: DistanceX(g2,g-4) = 10
    c: DistanceY(g-4,g2) = 2
FEATURE [Part::Part2DObjectPython] ShapeString  label="ATX only"  # Draft 2D object (typed FeaturePython)
  FontFile = <path>
  Fuse = false
  Justification = 6
  JustificationReference = 0
  KeepLeftMargin = false
  MakeFace = true
  ObliqueAngle = 0
  Placement = pos=(-167.8,152.22,8) rot=(0,0,1;0rad)
  ScaleToSize = true
  Size = 10
  String = A
  Tracking = 0
FEATURE [Part::Part2DObjectPython] ShapeString001  label="ATX only001"  # Draft 2D object (typed FeaturePython)
  FontFile = <path>
  Fuse = false
  Justification = 6
  JustificationReference = 0
  KeepLeftMargin = false
  MakeFace = true
  ObliqueAngle = 0
  Placement = pos=(-165.8,-0.68,8) rot=(0,0,1;0rad)
  ScaleToSize = true
  Size = 10
  String = A
  Tracking = 0
FEATURE [Part::Part2DObjectPython] ShapeString002  label="ATX only002"  # Draft 2D object (typed FeaturePython)
  FontFile = <path>
  Fuse = false
  Justification = 6
  JustificationReference = 0
  KeepLeftMargin = false
  MakeFace = true
  ObliqueAngle = 0
  Placement = pos=(-165.8,-72.08,8) rot=(0,0,1;0rad)
  ScaleToSize = true
  Size = 10
  String = A
  Tracking = 0
FEATURE [Part::Part2DObjectPython] ShapeString003  label="mATX only"  # Draft 2D object (typed FeaturePython)
  FontFile = <path>
  Fuse = false
  Justification = 6
  JustificationReference = 0
  KeepLeftMargin = false
  MakeFace = true
  ObliqueAngle = 0
  Placement = pos=(-96.1,143.22,8) rot=(0,0,1;0rad)
  ScaleToSize = true
  Size = 10
  String = M
  Tracking = 0
FEATURE [Part::Part2DObjectPython] ShapeString004  label="mATX only001"  # Draft 2D object (typed FeaturePython)
  FontFile = <path>
  Fuse = false
  Justification = 6
  JustificationReference = 0
  KeepLeftMargin = false
  MakeFace = true
  ObliqueAngle = 0
  Placement = pos=(-119.4,-11.68,8) rot=(0,0,1;0rad)
  ScaleToSize = true
  Size = 10
  String = M
  Tracking = 0
FEATURE [Part::Part2DObjectPython] ShapeString005  label="mATX only002"  # Draft 2D object (typed FeaturePython)
  FontFile = <path>
  Fuse = false
  Justification = 6
  JustificationReference = 0
  KeepLeftMargin = false
  MakeFace = true
  ObliqueAngle = 0
  Placement = pos=(-99.1,-11.68,8) rot=(0,0,1;0rad)
  ScaleToSize = true
  Size = 10
  String = M
  Tracking = 0
FEATURE [PartDesign::Pocket] Pocket001  label="PSU cutout"
  BaseFeature = -> Pad004
  Direction = (0,-1,2e-16)
  Length = 4
  Length2 = 5
  Profile = -> Sketch005
  ReferenceAxis = -> Sketch005 [N_Axis]
  Refine = true
  Suppressed = false
  Type = 0
  expr: Length = Spreadsheet.wall_thickness
FEATURE [Sketcher::SketchObject] Sketch009
  ArcFitTolerance = 1e-06
  ExternalGeometry = -> [Pocket001]
  FullyConstrained = true
  MakeInternals = false
  MapMode = 5
  Placement = pos=(0,0,8) rot=(0,0,1;0rad)
  expr: Constraints[7] = Spreadsheet.front_wall_thickness
  sketch-geometry (4):
    g0: LineSegment StartX=-215 StartY=-187.5 StartZ=0 EndX=215 EndY=-187.5 EndZ=0
    g1: LineSegment StartX=215 StartY=-187.5 StartZ=0 EndX=215 EndY=-184.5 EndZ=0
    g2: LineSegment StartX=215 StartY=-184.5 StartZ=0 EndX=-215 EndY=-184.5 EndZ=0
    g3: LineSegment StartX=-215 StartY=-184.5 StartZ=0 EndX=-215 EndY=-187.5 EndZ=0
  constraints (10):
    c: Horizontal(g2)
    c: Vertical(g1)
    c: Vertical(g3)
    c: Coincident(g3,g2)
    c: Coincident(g3,g0)
    c: Coincident(g1,g0)
    c: Coincident(g2,g1)
    c: DistanceY(g0,g1) = 3
    c: Coincident(g0,g-5)
    c: Coincident(g0,g-6)
FEATURE [PartDesign::Pad] Pad006  label="front wall"
  BaseFeature = -> Pocket001
  Direction = (0,0,1)
  Length = 168.5
  Length2 = 10
  Profile = -> Sketch009
  ReferenceAxis = -> Sketch009 [N_Axis]
  Refine = true
  Suppressed = false
  Type = 0
  expr: Length = Spreadsheet.front_wall_height - Spreadsheet.bottom_thickness
FEATURE [PartDesign::Pocket] Pocket003  label="pcie fasteners"
  BaseFeature = -> Pad006
  Direction = (0,0,-1)
  Length = 8
  Length2 = 5
  Profile = -> Sketch011
  ReferenceAxis = -> Sketch011 [N_Axis]
  Refine = true
  Suppressed = false
  Type = 0
  expr: Length = Spreadsheet.wall_thickness * 2
FEATURE [Sketcher::SketchObject] Sketch016
  ArcFitTolerance = 1e-06
  ExternalGeometry = -> [Pocket003]
  FullyConstrained = true
  MakeInternals = false
  MapMode = 5
  Placement = pos=(0,176.07,0) rot=(0,0.707107,0.707107;3.14159rad)
  sketch-geometry (4):
    g0: LineSegment StartX=-117.88 StartY=166.5 StartZ=0 EndX=-117.88 EndY=158.5 EndZ=0
    g1: LineSegment StartX=-117.88 StartY=158.5 StartZ=0 EndX=-109.88 EndY=158.5 EndZ=0
    g2: LineSegment StartX=-109.88 StartY=158.5 StartZ=0 EndX=-109.88 EndY=166.5 EndZ=0
    g3: LineSegment StartX=-109.88 StartY=166.5 StartZ=0 EndX=-117.88 EndY=166.5 EndZ=0
  constraints (12):
    c: Coincident(g0,g1)
    c: Coincident(g1,g2)
    c: Coincident(g2,g3)
    c: Coincident(g3,g0)
    c: Vertical(g0)
    c: Vertical(g2)
    c: Horizontal(g1)
    c: Horizontal(g3)
    c: Distance(g0,g2) = 8
    c: Distance(g1,g3) = 8
    c: Vertical(g0,g-3)
    c: Distance(g2,g-4) = 10
FEATURE [PartDesign::Pocket] Pocket007  label="rear ventilation template"
  BaseFeature = -> Pocket003
  Direction = (-1e-16,-1,2e-16)
  Length = 4
  Length2 = 5
  Profile = -> Sketch016
  ReferenceAxis = -> Sketch016 [N_Axis]
  Refine = true
  Suppressed = false
  Type = 0
  expr: Length = Spreadsheet.wall_thickness
FEATURE [PartDesign::LinearPattern] LinearPattern
  Direction = -> Sketch016 [H_Axis]
  Length = 140
  Mode = 1
  Occurrences = 15
  Offset = 10
  Refine = true
  Suppressed = false
  TransformMode = 0
FEATURE [PartDesign::LinearPattern] LinearPattern004
  Direction = -> Sketch016 [V_Axis]
  Length = 80
  Mode = 1
  Occurrences = 9
  Offset = 10
  Refine = true
  Reversed = true
  Suppressed = false
  TransformMode = 0
FEATURE [PartDesign::MultiTransform] MultiTransform  label="rear ventilation"
  BaseFeature = -> Pocket007
  Originals = -> [Pocket007]
  Refine = true
  Suppressed = false
  TransformMode = 0
  Transformations = -> [LinearPattern,LinearPattern004]
FEATURE [PartDesign::Hole] Hole  label="motherboard standoff holes"
  BaseFeature = -> MultiTransform
  CustomThreadClearance = 0
  Depth = 1205.5
  DepthType = 1
  Diameter = 3.4
  DrillForDepth = false
  DrillPoint = 1
  DrillPointAngle = 118
  HoleCutCountersinkAngle = 90
  HoleCutCustomValues = false
  HoleCutDepth = 0
  HoleCutDiameter = 6.1
  HoleCutType = 0
  ModelThread = false
  Profile = -> Sketch008
  Refine = true
  Suppressed = false
  Tapered = false
  TaperedAngle = 90
  ThreadClass = 0
  ThreadDepth = 1205.5
  ThreadDepthType = 0
  ThreadDirection = 0
  ThreadFit = 0
  ThreadSize = 9
  ThreadType = 1
  Threaded = false
  UseCustomThreadClearance = false
FEATURE [Sketcher::SketchObject] Sketch021
  ArcFitTolerance = 1e-06
  ExternalGeometry = -> [Sketch008,Hole]
  FullyConstrained = true
  MakeInternals = false
  MapMode = 5
  Placement = pos=(0,0,8) rot=(0,0,1;0rad)
  expr: Constraints[8] = Spreadsheet.motherboard_front_padding
  sketch-geometry (24):
    g0: LineSegment StartX=-43.4 StartY=-79.93 StartZ=0 EndX=-43.4 EndY=-84.93 EndZ=0
    g1: LineSegment StartX=-43.4 StartY=-84.93 StartZ=0 EndX=76.6 EndY=-84.93 EndZ=0
    g2: LineSegment StartX=76.6 StartY=-84.93 StartZ=0 EndX=76.6 EndY=-79.93 EndZ=0
    g3: LineSegment StartX=76.6 StartY=-79.93 StartZ=0 EndX=-43.4 EndY=-79.93 EndZ=0
    g4: LineSegment StartX=-43.4 StartY=-136.6 StartZ=0 EndX=-43.4 EndY=-184.4 EndZ=0
    g5: LineSegment StartX=-43.4 StartY=-184.4 StartZ=0 EndX=76.6 EndY=-184.4 EndZ=0
    g6: LineSegment StartX=76.6 StartY=-184.4 StartZ=0 EndX=76.6 EndY=-136.6 EndZ=0
    g7: LineSegment StartX=76.6 StartY=-136.6 StartZ=0 EndX=-43.4 EndY=-136.6 EndZ=0
    g8: LineSegment StartX=-58.4 StartY=-79.93 StartZ=0 EndX=-178.4 EndY=-79.93 EndZ=0
    g9: LineSegment StartX=-178.4 StartY=-79.93 StartZ=0 EndX=-178.4 EndY=-84.93 EndZ=0
    g10: LineSegment StartX=-178.4 StartY=-84.93 StartZ=0 EndX=-58.4 EndY=-84.93 EndZ=0
    g11: LineSegment StartX=-58.4 StartY=-84.93 StartZ=0 EndX=-58.4 EndY=-79.93 EndZ=0
    g12: LineSegment StartX=-58.4 StartY=-136.6 StartZ=0 EndX=-178.4 EndY=-136.6 EndZ=0
    g13: LineSegment StartX=-178.4 StartY=-136.6 StartZ=0 EndX=-178.4 EndY=-184.4 EndZ=0
    g14: LineSegment StartX=-178.4 StartY=-184.4 StartZ=0 EndX=-58.4 EndY=-184.4 EndZ=0
    g15: LineSegment StartX=-58.4 StartY=-184.4 StartZ=0 EndX=-58.4 EndY=-136.6 EndZ=0
    g16: LineSegment StartX=90 StartY=-79.93 StartZ=0 EndX=90 EndY=-84.93 EndZ=0
    g17: LineSegment StartX=90 StartY=-84.93 StartZ=0 EndX=210 EndY=-84.93 EndZ=0
    g18: LineSegment StartX=210 StartY=-84.93 StartZ=0 EndX=210 EndY=-79.93 EndZ=0
    g19: LineSegment StartX=210 StartY=-79.93 StartZ=0 EndX=90 EndY=-79.93 EndZ=0
    g20: LineSegment StartX=90 StartY=-136.6 StartZ=0 EndX=90 EndY=-184.4 EndZ=0
    g21: LineSegment StartX=90 StartY=-184.4 StartZ=0 EndX=210 EndY=-184.4 EndZ=0
    g22: LineSegment StartX=210 StartY=-184.4 StartZ=0 EndX=210 EndY=-136.6 EndZ=0
    g23: LineSegment StartX=210 StartY=-136.6 StartZ=0 EndX=90 EndY=-136.6 EndZ=0
  constraints (72):
    c: Coincident(g0,g1)
    c: Coincident(g1,g2)
    c: Coincident(g2,g3)
    c: Coincident(g3,g0)
    c: Vertical(g0)
    c: Vertical(g2)
    c: Horizontal(g1)
    c: Horizontal(g3)
    c: Distance(g3,g-3) = 6.35
    c: DistanceY(g0,g0) = 5
    c: Coincident(g4,g5)
    c: Coincident(g5,g6)
    c: Coincident(g6,g7)
    c: Coincident(g7,g4)
    c: Vertical(g4)
    c: Vertical(g6)
    c: Horizontal(g5)
    c: Horizontal(g7)
    c: DistanceY(g4,g4) = 47.8
    c: Vertical(g0,g4)
    c: Vertical(g6,g1)
    c: Distance(g0,g7) = 51.67
    c: Coincident(g8,g9)
    c: Coincident(g9,g10)
    c: Coincident(g10,g11)
    c: Coincident(g11,g8)
    c: Horizontal(g8)
    c: Horizontal(g10)
    c: Vertical(g9)
    c: Vertical(g11)
    c: Coincident(g12,g13)
    c: Coincident(g13,g14)
    c: Coincident(g14,g15)
    c: Coincident(g15,g12)
    c: Horizontal(g12)
    c: Horizontal(g14)
    c: Vertical(g13)
    c: Vertical(g15)
    c: Equal(g11,g0)
    c: Horizontal(g0,g8)
    c: Equal(g4,g15)
    c: Horizontal(g4,g12)
    c: Vertical(g10,g12)
    c: DistanceX(g0,g1) = 120
    c: Equal(g1,g10)
    c: Equal(g10,g12)
    c: Coincident(g16,g17)
    c: Coincident(g17,g18)
    c: Coincident(g18,g19)
    c: Coincident(g19,g16)
    c: Vertical(g16)
    c: Vertical(g18)
    c: Horizontal(g17)
    c: Horizontal(g19)
    c: Coincident(g20,g21)
    c: Coincident(g21,g22)
    c: Coincident(g22,g23)
    c: Coincident(g23,g20)
    c: Vertical(g20)
    c: Vertical(g22)
    c: Horizontal(g21)
    c: Horizontal(g23)
    c: Horizontal(g2,g16)
    c: Equal(g18,g11)
    c: Vertical(g16,g20)
    c: Equal(g20,g6)
    c: Equal(g17,g23)
    c: Horizontal(g6,g20)
    c: Equal(g17,g1)
    c: DistanceX(g-6,g0) = 2
    c: Distance(g18,g-4) = 1
    c: Distance(g0,g8) = 15
FEATURE [PartDesign::Pad] Pad016  label="drive cage studs"
  BaseFeature = -> Hole
  Direction = (0,0,1)
  Length = 6.5
  Length2 = 10
  Profile = -> Sketch021
  ReferenceAxis = -> Sketch021 [N_Axis]
  Refine = true
  Suppressed = false
  Type = 0
FEATURE [Sketcher::SketchObject] Sketch022
  ArcFitTolerance = 1e-06
  AttachmentSupport = -> [Pad016]
  ExternalGeometry = -> [Pad016]
  FullyConstrained = true
  MakeInternals = false
  MapMode = 5
  Placement = pos=(0,0,14.5) rot=(0,0,1;0rad)
  sketch-geometry (37):
    g0: Circle CenterX=61.6 CenterY=-169.4 CenterZ=0 NormalX=0 NormalY=0 NormalZ=1 AngleXU=0 Radius=1.25
    g1: Circle CenterX=61.6 CenterY=-154.4 CenterZ=0 NormalX=0 NormalY=0 NormalZ=1 AngleXU=0 Radius=1.25
    g2: Circle CenterX=61.6 CenterY=-82.43 CenterZ=0 NormalX=0 NormalY=0 NormalZ=1 AngleXU=0 Radius=1.25
    g3: GeomPoint [constr] X=76.6 Y=-82.43 Z=0
    g4: Circle CenterX=31.6 CenterY=-82.43 CenterZ=0 NormalX=0 NormalY=0 NormalZ=1 AngleXU=0 Radius=1.25
    g5: Circle CenterX=1.6 CenterY=-82.43 CenterZ=0 NormalX=0 NormalY=0 NormalZ=1 AngleXU=0 Radius=1.25
    g6: Circle CenterX=-28.4 CenterY=-82.43 CenterZ=0 NormalX=0 NormalY=0 NormalZ=1 AngleXU=0 Radius=1.25
    g7: Circle CenterX=31.6 CenterY=-154.4 CenterZ=0 NormalX=0 NormalY=0 NormalZ=1 AngleXU=0 Radius=1.25
    g8: Circle CenterX=1.6 CenterY=-154.4 CenterZ=0 NormalX=0 NormalY=0 NormalZ=1 AngleXU=0 Radius=1.25
    g9: Circle CenterX=-28.4 CenterY=-154.4 CenterZ=0 NormalX=0 NormalY=0 NormalZ=1 AngleXU=0 Radius=1.25
    g10: Circle CenterX=31.6 CenterY=-169.4 CenterZ=0 NormalX=0 NormalY=0 NormalZ=1 AngleXU=0 Radius=1.25
    g11: Circle CenterX=1.6 CenterY=-169.4 CenterZ=0 NormalX=0 NormalY=0 NormalZ=1 AngleXU=0 Radius=1.25
    g12: Circle CenterX=-28.4 CenterY=-169.4 CenterZ=0 NormalX=0 NormalY=0 NormalZ=1 AngleXU=0 Radius=1.25
    g13: Circle CenterX=-163.4 CenterY=-82.43 CenterZ=0 NormalX=0 NormalY=0 NormalZ=1 AngleXU=0 Radius=1.25
    g14: Circle CenterX=-73.4 CenterY=-82.43 CenterZ=0 NormalX=0 NormalY=0 NormalZ=1 AngleXU=0 Radius=1.25
    g15: Circle CenterX=-103.4 CenterY=-82.43 CenterZ=0 NormalX=0 NormalY=0 NormalZ=1 AngleXU=0 Radius=1.25
    g16: Circle CenterX=-133.4 CenterY=-82.43 CenterZ=0 NormalX=0 NormalY=0 NormalZ=1 AngleXU=0 Radius=1.25
    g17: Circle CenterX=-163.4 CenterY=-154.4 CenterZ=0 NormalX=0 NormalY=0 NormalZ=1 AngleXU=0 Radius=1.25
    g18: Circle CenterX=-133.4 CenterY=-154.4 CenterZ=0 NormalX=0 NormalY=0 NormalZ=1 AngleXU=0 Radius=1.25
    g19: Circle CenterX=-103.4 CenterY=-154.4 CenterZ=0 NormalX=0 NormalY=0 NormalZ=1 AngleXU=0 Radius=1.25
    g20: Circle CenterX=-73.4 CenterY=-154.4 CenterZ=0 NormalX=0 NormalY=0 NormalZ=1 AngleXU=0 Radius=1.25
    g21: Circle CenterX=-73.4 CenterY=-169.4 CenterZ=0 NormalX=0 NormalY=0 NormalZ=1 AngleXU=0 Radius=1.25
    g22: Circle CenterX=-103.4 CenterY=-169.4 CenterZ=0 NormalX=0 NormalY=0 NormalZ=1 AngleXU=0 Radius=1.25
    g23: Circle CenterX=-133.4 CenterY=-169.4 CenterZ=0 NormalX=0 NormalY=0 NormalZ=1 AngleXU=0 Radius=1.25
    g24: Circle CenterX=-163.4 CenterY=-169.4 CenterZ=0 NormalX=0 NormalY=0 NormalZ=1 AngleXU=0 Radius=1.25
    g25: Circle CenterX=195 CenterY=-82.43 CenterZ=0 NormalX=0 NormalY=0 NormalZ=1 AngleXU=0 Radius=1.25
    g26: Circle CenterX=105 CenterY=-82.43 CenterZ=0 NormalX=0 NormalY=0 NormalZ=1 AngleXU=0 Radius=1.25
    g27: Circle CenterX=135 CenterY=-82.43 CenterZ=0 NormalX=0 NormalY=0 NormalZ=1 AngleXU=0 Radius=1.25
    g28: Circle CenterX=165 CenterY=-82.43 CenterZ=0 NormalX=0 NormalY=0 NormalZ=1 AngleXU=0 Radius=1.25
    g29: Circle CenterX=105 CenterY=-154.4 CenterZ=0 NormalX=0 NormalY=0 NormalZ=1 AngleXU=0 Radius=1.25
    g30: Circle CenterX=135 CenterY=-154.4 CenterZ=0 NormalX=0 NormalY=0 NormalZ=1 AngleXU=0 Radius=1.25
    g31: Circle CenterX=165 CenterY=-154.4 CenterZ=0 NormalX=0 NormalY=0 NormalZ=1 AngleXU=0 Radius=1.25
    g32: Circle CenterX=195 CenterY=-154.4 CenterZ=0 NormalX=0 NormalY=0 NormalZ=1 AngleXU=0 Radius=1.25
    g33: Circle CenterX=195 CenterY=-169.4 CenterZ=0 NormalX=0 NormalY=0 NormalZ=1 AngleXU=0 Radius=1.25
    g34: Circle CenterX=165 CenterY=-169.4 CenterZ=0 NormalX=0 NormalY=0 NormalZ=1 AngleXU=0 Radius=1.25
    g35: Circle CenterX=135 CenterY=-169.4 CenterZ=0 NormalX=0 NormalY=0 NormalZ=1 AngleXU=0 Radius=1.25
    g36: Circle CenterX=105 CenterY=-169.4 CenterZ=0 NormalX=0 NormalY=0 NormalZ=1 AngleXU=0 Radius=1.25
  constraints (109):
    c: Distance(g0,g-3) = 15
    c: Vertical(g1,g0)
    c: DistanceY(g0,g1) = 15
    c: Symmetric(g-5,g-5,g3)
    c: Horizontal(g2,g3)
    c: DistanceX(g2,g3) = 15
    c: Equal(g2,g1)
    c: Equal(g1,g0)
    c: Diameter(g2) = 2.5
    c: DistanceX(g1,g-4) = 15
    c: Equal(g2,g4)
    c: Equal(g4,g5)
    c: Equal(g5,g6)
    c: Equal(g1,g7)
    c: Equal(g7,g8)
    c: Equal(g8,g9)
    c: Horizontal(g2,g4)
    c: Horizontal(g4,g5)
    c: Horizontal(g5,g6)
    c: Equal(g12,g11)
    c: Equal(g11,g10)
    c: Equal(g10,g0)
    c: Horizontal(g1,g7)
    c: Horizontal(g7,g8)
    c: Horizontal(g8,g9)
    c: Horizontal(g12,g11)
    c: Horizontal(g11,g10)
    c: Horizontal(g10,g0)
    c: Vertical(g6,g9)
    c: Vertical(g9,g12)
    c: Vertical(g11,g8)
    c: Vertical(g8,g5)
    c: Vertical(g4,g7)
    c: Vertical(g7,g10)
    c: DistanceX(g10,g0) = 30
    c: DistanceX(g11,g10) = 30
    c: DistanceX(g12,g11) = 30
    c: Horizontal(g14,g15)
    c: Horizontal(g15,g16)
    c: Horizontal(g16,g13)
    c: Horizontal(g20,g19)
    c: Horizontal(g19,g18)
    c: Horizontal(g18,g17)
    c: Horizontal(g21,g22)
    c: Horizontal(g22,g23)
    c: Horizontal(g23,g24)
    c: Vertical(g14,g20)
    c: Vertical(g20,g21)
    c: Vertical(g22,g19)
    c: Vertical(g19,g15)
    c: Vertical(g16,g18)
    c: Vertical(g18,g23)
    c: Vertical(g13,g17)
    c: Vertical(g17,g24)
    c: DistanceX(g14,g-6) = 15
    c: Distance(g14,g15) = 30
    c: DistanceX(g16,g15) = 30
    c: DistanceX(g13,g16) = 30
    c: Horizontal(g6,g14)
    c: Horizontal(g9,g20)
    c: Horizontal(g12,g21)
    c: Equal(g20,g19)
    c: Equal(g19,g22)
    c: Equal(g22,g21)
    c: Equal(g21,g23)
    c: Equal(g23,g18)
    c: Equal(g18,g17)
    c: Equal(g17,g24)
    c: Equal(g24,g13)
    c: Equal(g13,g16)
    c: Equal(g16,g15)
    c: Equal(g15,g14)
    c: Equal(g14,g6)
    c: Horizontal(g26,g27)
    c: Horizontal(g27,g28)
    c: Horizontal(g28,g25)
    c: Horizontal(g32,g31)
    c: Horizontal(g31,g30)
    c: Horizontal(g30,g29)
    c: Horizontal(g36,g35)
    c: Horizontal(g35,g34)
    c: Horizontal(g34,g33)
    c: Vertical(g33,g32)
    c: Vertical(g32,g25)
    c: Vertical(g34,g31)
    c: Vertical(g31,g28)
    c: Vertical(g27,g30)
    c: Vertical(g30,g35)
    c: Vertical(g36,g29)
    c: Vertical(g29,g26)
    c: DistanceX(g28,g25) = 30
    c: DistanceX(g27,g28) = 30
    c: DistanceX(g26,g27) = 30
    c: DistanceX(g25,g-7) = 15
    c: Horizontal(g26,g2)
    c: Horizontal(g1,g29)
    c: Horizontal(g36,g0)
    c: Equal(g25,g28)
    c: Equal(g28,g27)
    c: Equal(g27,g26)
    c: Equal(g26,g29)
    c: Equal(g29,g36)
    c: Equal(g36,g35)
    c: Equal(g35,g30)
    c: Equal(g30,g31)
    c: Equal(g31,g34)
    c: Equal(g34,g33)
    c: Equal(g33,g32)
    c: Equal(g26,g2)
FEATURE [PartDesign::Hole] Hole001  label="drive cage hole"
  BaseFeature = -> Pad016
  CustomThreadClearance = 0
  Depth = 1205.5
  DepthType = 1
  Diameter = 2.9
  DrillForDepth = false
  DrillPoint = 1
  DrillPointAngle = 118
  HoleCutCountersinkAngle = 90
  HoleCutCustomValues = false
  HoleCutDepth = 0
  HoleCutDiameter = 6.1
  HoleCutType = 0
  ModelThread = false
  Profile = -> Sketch022
  Refine = true
  Suppressed = false
  Tapered = false
  TaperedAngle = 90
  ThreadClass = 0
  ThreadDepth = 1205.5
  ThreadDepthType = 0
  ThreadDirection = 0
  ThreadFit = 0
  ThreadSize = 8
  ThreadType = 1
  Threaded = false
  UseCustomThreadClearance = false
FEATURE [Sketcher::SketchObject] Sketch041
  ArcFitTolerance = 1e-06
  FullyConstrained = true
  MakeInternals = false
  MapMode = 5
  Placement = pos=(0,0,8) rot=(0,0,1;0rad)
  sketch-geometry (4):
    g0: LineSegment StartX=120.9 StartY=176.07 StartZ=0 EndX=120.9 EndY=187.5 EndZ=0
    g1: LineSegment StartX=120.9 StartY=187.5 StartZ=0 EndX=-215 EndY=187.5 EndZ=0
    g2: LineSegment StartX=-215 StartY=187.5 StartZ=0 EndX=-215 EndY=176.07 EndZ=0
    g3: LineSegment StartX=-215 StartY=176.07 StartZ=0 EndX=120.9 EndY=176.07 EndZ=0
  constraints (9):
    c: Coincident(g0,g1)
    c: Coincident(g1,g2)
    c: Coincident(g2,g3)
    c: Coincident(g3,g0)
    c: Vertical(g2)
    c: Horizontal(g3)
    c: Coincident(g0,g-4)
    c: Coincident(g0,g-4)
    c: Coincident(g1,g-6)
FEATURE [Sketcher::SketchObject] Sketch024
  ArcFitTolerance = 1e-06
  ExternalGeometry = -> [Hole001]
  FullyConstrained = true
  MakeInternals = false
  MapMode = 5
  Placement = pos=(0,-187.5,0) rot=(1,0,0;1.5708rad)
  sketch-geometry (1):
    g0: Circle CenterX=-196 CenterY=28 CenterZ=0 NormalX=0 NormalY=0 NormalZ=1 AngleXU=0 Radius=8
  constraints (3):
    c: Diameter(g0) = 16
    c: DistanceX(g-3,g0) = 15
    c: DistanceY(g-3,g0) = 20
FEATURE [PartDesign::Hole] Hole003  label="power switch"
  BaseFeature = -> Hole001
  CustomThreadClearance = 0
  Depth = 3
  DepthType = 0
  Diameter = 17.5
  DrillForDepth = false
  DrillPoint = 1
  DrillPointAngle = 118
  HoleCutCountersinkAngle = 90
  HoleCutCustomValues = false
  HoleCutDepth = 0
  HoleCutDiameter = 6.1
  HoleCutType = 0
  ModelThread = false
  Profile = -> Sketch024
  Refine = true
  Suppressed = false
  Tapered = false
  TaperedAngle = 90
  ThreadClass = 0
  ThreadDepth = 3
  ThreadDepthType = 0
  ThreadDirection = 0
  ThreadFit = 0
  ThreadSize = 22
  ThreadType = 1
  Threaded = false
  UseCustomThreadClearance = false
  expr: Depth = Spreadsheet.front_wall_thickness
FEATURE [PartDesign::Pocket] Pocket010
  BaseFeature = -> Hole003
  Direction = (0,0,-1)
  Length = 1
  Length2 = 5
  Profile = -> ShapeString
  ReferenceAxis = -> ShapeString [N_Axis]
  Refine = true
  Suppressed = false
  Type = 0
FEATURE [PartDesign::Pocket] Pocket011
  BaseFeature = -> Pocket010
  Direction = (0,0,-1)
  Length = 1
  Length2 = 5
  Profile = -> ShapeString001
  ReferenceAxis = -> ShapeString001 [N_Axis]
  Refine = true
  Suppressed = false
  Type = 0
FEATURE [PartDesign::Pocket] Pocket012
  BaseFeature = -> Pocket011
  Direction = (0,0,-1)
  Length = 1
  Length2 = 5
  Profile = -> ShapeString002
  ReferenceAxis = -> ShapeString002 [N_Axis]
  Refine = true
  Suppressed = false
  Type = 0
FEATURE [PartDesign::Pocket] Pocket013
  BaseFeature = -> Pocket012
  Direction = (0,0,-1)
  Length = 1
  Length2 = 5
  Profile = -> ShapeString003
  ReferenceAxis = -> ShapeString003 [N_Axis]
  Refine = true
  Suppressed = false
  Type = 0
FEATURE [PartDesign::Pocket] Pocket014
  BaseFeature = -> Pocket013
  Direction = (0,0,-1)
  Length = 1
  Length2 = 5
  Profile = -> ShapeString004
  ReferenceAxis = -> ShapeString004 [N_Axis]
  Refine = true
  Suppressed = false
  Type = 0
FEATURE [PartDesign::Pocket] Pocket015
  BaseFeature = -> Pocket014
  Direction = (0,0,-1)
  Length = 1
  Length2 = 5
  Profile = -> ShapeString005
  ReferenceAxis = -> ShapeString005 [N_Axis]
  Refine = true
  Suppressed = false
  Type = 0
FEATURE [PartDesign::Pocket] Pocket016  label="PSU fan opening"
  BaseFeature = -> Pocket015
  Direction = (-1,-1e-16,1e-16)
  Length = 1
  Length2 = 5
  Profile = -> Sketch020
  ReferenceAxis = -> Sketch020 [N_Axis]
  Refine = true
  Suppressed = false
  Type = 0
FEATURE [Sketcher::SketchObject] Sketch026
  ArcFitTolerance = 1e-06
  AttachmentSupport = -> [Pocket016]
  ExternalGeometry = -> [Pocket016]
  FullyConstrained = true
  MakeInternals = false
  MapMode = 5
  Placement = pos=(-215,0,0) rot=(0.57735,-0.57735,-0.57735;2.0944rad)
  expr: Constraints[33] = Spreadsheet.fan_mounting_hole_diameter
  sketch-geometry (15):
    g0: LineSegment [constr] StartX=-157.07 StartY=156 StartZ=0 EndX=-157.07 EndY=36 EndZ=0
    g1: LineSegment [constr] StartX=-157.07 StartY=36 StartZ=0 EndX=-37.07 EndY=36 EndZ=0
    g2: LineSegment [constr] StartX=-37.07 StartY=36 StartZ=0 EndX=-37.07 EndY=156 EndZ=0
    g3: LineSegment [constr] StartX=-37.07 StartY=156 StartZ=0 EndX=-157.07 EndY=156 EndZ=0
    g4: LineSegment [constr] StartX=-149.82 StartY=148.75 StartZ=0 EndX=-149.82 EndY=43.25 EndZ=0
    g5: LineSegment [constr] StartX=-149.82 StartY=43.25 StartZ=0 EndX=-44.32 EndY=43.25 EndZ=0
    g6: LineSegment [constr] StartX=-44.32 StartY=43.25 StartZ=0 EndX=-44.32 EndY=148.75 EndZ=0
    g7: LineSegment [constr] StartX=-44.32 StartY=148.75 StartZ=0 EndX=-149.82 EndY=148.75 EndZ=0
    g8: LineSegment [constr] StartX=-157.07 StartY=156 StartZ=0 EndX=-37.07 EndY=36 EndZ=0
    g9: LineSegment [constr] StartX=-37.07 StartY=156 StartZ=0 EndX=-157.07 EndY=36 EndZ=0
    g10: GeomPoint [constr] X=-97.07 Y=96 Z=0
    g11: Circle CenterX=-149.82 CenterY=43.25 CenterZ=0 NormalX=0 NormalY=0 NormalZ=1 AngleXU=0 Radius=2.1
    g12: Circle CenterX=-149.82 CenterY=148.75 CenterZ=0 NormalX=0 NormalY=0 NormalZ=1 AngleXU=0 Radius=2.1
    g13: Circle CenterX=-44.32 CenterY=148.75 CenterZ=0 NormalX=0 NormalY=0 NormalZ=1 AngleXU=0 Radius=2.1
    g14: Circle CenterX=-44.32 CenterY=43.25 CenterZ=0 NormalX=0 NormalY=0 NormalZ=1 AngleXU=0 Radius=2.1
  constraints (36):
    c: Coincident(g0,g1)
    c: Coincident(g1,g2)
    c: Coincident(g2,g3)
    c: Coincident(g3,g0)
    c: Vertical(g0)
    c: Vertical(g2)
    c: Horizontal(g1)
    c: Horizontal(g3)
    c: DistanceY(g1,g2) = 120
    c: Coincident(g4,g5)
    c: Coincident(g5,g6)
    c: Coincident(g6,g7)
    c: Coincident(g7,g4)
    c: Vertical(g4)
    c: Vertical(g6)
    c: Horizontal(g5)
    c: Horizontal(g7)
    c: Distance(g4,g6) = 105.5
    c: Distance(g5,g7) = 105.5
    c: Coincident(g8,g0)
    c: Coincident(g8,g1)
    c: Coincident(g9,g2)
    c: Coincident(g9,g0)
    c: Symmetric(g9,g9,g10)
    c: Equal(g2,g1)
    c: Symmetric(g6,g4,g10)
    c: Coincident(g11,g4)
    c: Coincident(g12,g4)
    c: Coincident(g13,g6)
    c: Coincident(g14,g5)
    c: Equal(g14,g11)
    c: Equal(g11,g12)
    c: Equal(g12,g13)
    c: Diameter(g12) = 4.2
    c: DistanceX(g-4,g0) = 15
    c: Distance(g-4,g1) = 28
FEATURE [PartDesign::Hole] Hole007  label="side fan mount holes"
  BaseFeature = -> Pocket016
  CustomThreadClearance = 0
  Depth = 4
  DepthType = 0
  Diameter = 5.5
  DrillForDepth = false
  DrillPoint = 0
  DrillPointAngle = 118
  HoleCutCountersinkAngle = 90
  HoleCutCustomValues = false
  HoleCutDepth = 1.5
  HoleCutDiameter = 10
  HoleCutType = 1
  ModelThread = false
  Profile = -> Sketch026
  Refine = true
  Suppressed = false
  Tapered = false
  TaperedAngle = 90
  ThreadClass = 0
  ThreadDepth = 4
  ThreadDepthType = 0
  ThreadDirection = 0
  ThreadFit = 0
  ThreadSize = 13
  ThreadType = 1
  Threaded = false
  UseCustomThreadClearance = false
  expr: Depth = Spreadsheet.wall_thickness
FEATURE [Sketcher::SketchObject] Sketch027
  ArcFitTolerance = 1e-06
  AttachmentSupport = -> [Hole007]
  ExternalGeometry = -> [Sketch026]
  FullyConstrained = true
  MakeInternals = false
  MapMode = 5
  Placement = pos=(-215,0,0) rot=(0.57735,-0.57735,-0.57735;2.0944rad)
  sketch-geometry (6):
    g0: GeomPoint [constr] X=-97.07 Y=96 Z=0
    g1: LineSegment [constr] StartX=-157.07 StartY=156 StartZ=0 EndX=-157.07 EndY=36 EndZ=0
    g2: LineSegment [constr] StartX=-157.07 StartY=36 StartZ=0 EndX=-37.07 EndY=36 EndZ=0
    g3: LineSegment [constr] StartX=-37.07 StartY=36 StartZ=0 EndX=-37.07 EndY=156 EndZ=0
    g4: LineSegment [constr] StartX=-37.07 StartY=156 StartZ=0 EndX=-157.07 EndY=156 EndZ=0
    g5: Circle CenterX=-97.07 CenterY=96 CenterZ=0 NormalX=0 NormalY=0 NormalZ=1 AngleXU=0 Radius=59
  constraints (14):
    c: Coincident(g1,g2)
    c: Coincident(g2,g3)
    c: Coincident(g3,g4)
    c: Coincident(g4,g1)
    c: Vertical(g1)
    c: Vertical(g3)
    c: Horizontal(g2)
    c: Horizontal(g4)
    c: Distance(g1,g3) = 120
    c: Distance(g2,g4) = 120
    c: Symmetric(g1,g3,g0)
    c: Diameter(g5) = 118
    c: Coincident(g5,g0)
    c: Symmetric(g-4,g-6,g0)
FEATURE [PartDesign::Pocket] Pocket017  label="side fan opening"
  BaseFeature = -> Hole007
  Direction = (1,0,0)
  Length = 1
  Length2 = 5
  Profile = -> Sketch027
  ReferenceAxis = -> Sketch027 [N_Axis]
  Refine = true
  Suppressed = false
  Type = 0
FEATURE [Sketcher::SketchObject] Sketch028
  ArcFitTolerance = 1e-06
  AttachmentSupport = -> [Pocket017]
  ExternalGeometry = -> [Pocket017]
  FullyConstrained = true
  MakeInternals = false
  MapMode = 5
  Placement = pos=(0,-187.5,0) rot=(1,0,0;1.5708rad)
  sketch-geometry (12):
    g0: LineSegment StartX=-178.4 StartY=173 StartZ=0 EndX=-178.4 EndY=14.5 EndZ=0
    g1: LineSegment StartX=-178.4 StartY=14.5 StartZ=0 EndX=-58.4 EndY=14.5 EndZ=0
    g2: LineSegment StartX=-58.4 StartY=14.5 StartZ=0 EndX=-58.4 EndY=173 EndZ=0
    g3: LineSegment StartX=-58.4 StartY=173 StartZ=0 EndX=-178.4 EndY=173 EndZ=0
    g4: LineSegment StartX=-43.4 StartY=173 StartZ=0 EndX=-43.4 EndY=14.5 EndZ=0
    g5: LineSegment StartX=-43.4 StartY=14.5 StartZ=0 EndX=76.6 EndY=14.5 EndZ=0
    g6: LineSegment StartX=76.6 StartY=14.5 StartZ=0 EndX=76.6 EndY=173 EndZ=0
    g7: LineSegment StartX=76.6 StartY=173 StartZ=0 EndX=-43.4 EndY=173 EndZ=0
    g8: LineSegment StartX=90 StartY=173 StartZ=0 EndX=90 EndY=14.5 EndZ=0
    g9: LineSegment StartX=90 StartY=14.5 StartZ=0 EndX=210 EndY=14.5 EndZ=0
    g10: LineSegment StartX=210 StartY=14.5 StartZ=0 EndX=210 EndY=173 EndZ=0
    g11: LineSegment StartX=210 StartY=173 StartZ=0 EndX=90 EndY=173 EndZ=0
  constraints (33):
    c: Coincident(g0,g1)
    c: Coincident(g1,g2)
    c: Coincident(g2,g3)
    c: Coincident(g3,g0)
    c: Vertical(g0)
    c: Vertical(g2)
    c: Horizontal(g1)
    c: Horizontal(g3)
    c: Coincident(g4,g5)
    c: Coincident(g5,g6)
    c: Coincident(g6,g7)
    c: Coincident(g7,g4)
    c: Vertical(g4)
    c: Vertical(g6)
    c: Horizontal(g5)
    c: Horizontal(g7)
    c: Coincident(g8,g9)
    c: Coincident(g9,g10)
    c: Coincident(g10,g11)
    c: Coincident(g11,g8)
    c: Vertical(g8)
    c: Vertical(g10)
    c: Horizontal(g9)
    c: Horizontal(g11)
    c: DistanceY(g0,g-6) = 2
    c: DistanceX(g0,g2) = 120
    c: Equal(g2,g4)
    c: Equal(g4,g8)
    c: Equal(g3,g7)
    c: Equal(g7,g11)
    c: Coincident(g0,g-3)
    c: Coincident(g-4,g4)
    c: Coincident(g8,g-5)
FEATURE [PartDesign::Pocket] Pocket018  label="front wall mesh placeholders"
  BaseFeature = -> Pocket017
  Direction = (0,1,-2e-16)
  Length = 1
  Length2 = 5
  Profile = -> Sketch028
  ReferenceAxis = -> Sketch028 [N_Axis]
  Refine = true
  Suppressed = false
  Type = 0
FEATURE [Sketcher::SketchObject] Sketch029
  ArcFitTolerance = 1e-06
  AttachmentSupport = -> [Pocket018]
  ExternalGeometry = -> [Pocket018]
  FullyConstrained = true
  MakeInternals = false
  MapMode = 5
  Placement = pos=(0,0,0) rot=(1,0,0;3.14159rad)
  sketch-geometry (36):
    g0: LineSegment StartX=200 StartY=172.4 StartZ=0 EndX=100 EndY=172.4 EndZ=0
    g1: LineSegment StartX=100 StartY=172.4 StartZ=0 EndX=100 EndY=166.4 EndZ=0
    g2: LineSegment StartX=100 StartY=166.4 StartZ=0 EndX=200 EndY=166.4 EndZ=0
    g3: LineSegment StartX=200 StartY=166.4 StartZ=0 EndX=200 EndY=172.4 EndZ=0
    g4: LineSegment StartX=200 StartY=157.4 StartZ=0 EndX=100 EndY=157.4 EndZ=0
    g5: LineSegment StartX=100 StartY=157.4 StartZ=0 EndX=100 EndY=151.4 EndZ=0
    g6: LineSegment StartX=100 StartY=151.4 StartZ=0 EndX=200 EndY=151.4 EndZ=0
    g7: LineSegment StartX=200 StartY=151.4 StartZ=0 EndX=200 EndY=157.4 EndZ=0
    g8: LineSegment StartX=200 StartY=85.43 StartZ=0 EndX=100 EndY=85.43 EndZ=0
    g9: LineSegment StartX=100 StartY=85.43 StartZ=0 EndX=100 EndY=79.43 EndZ=0
    g10: LineSegment StartX=100 StartY=79.43 StartZ=0 EndX=200 EndY=79.43 EndZ=0
    g11: LineSegment StartX=200 StartY=79.43 StartZ=0 EndX=200 EndY=85.43 EndZ=0
    g12: LineSegment StartX=66.6 StartY=85.43 StartZ=0 EndX=-33.4 EndY=85.43 EndZ=0
    g13: LineSegment StartX=-33.4 StartY=85.43 StartZ=0 EndX=-33.4 EndY=79.43 EndZ=0
    g14: LineSegment StartX=-33.4 StartY=79.43 StartZ=0 EndX=66.6 EndY=79.43 EndZ=0
    g15: LineSegment StartX=66.6 StartY=79.43 StartZ=0 EndX=66.6 EndY=85.43 EndZ=0
    g16: LineSegment StartX=66.6 StartY=157.4 StartZ=0 EndX=-33.4 EndY=157.4 EndZ=0
    g17: LineSegment StartX=-33.4 StartY=157.4 StartZ=0 EndX=-33.4 EndY=151.4 EndZ=0
    g18: LineSegment StartX=-33.4 StartY=151.4 StartZ=0 EndX=66.6 EndY=151.4 EndZ=0
    g19: LineSegment StartX=66.6 StartY=151.4 StartZ=0 EndX=66.6 EndY=157.4 EndZ=0
    g20: LineSegment StartX=66.6 StartY=172.4 StartZ=0 EndX=-33.4 EndY=172.4 EndZ=0
    g21: LineSegment StartX=-33.4 StartY=172.4 StartZ=0 EndX=-33.4 EndY=166.4 EndZ=0
    g22: LineSegment StartX=-33.4 StartY=166.4 StartZ=0 EndX=66.6 EndY=166.4 EndZ=0
    g23: LineSegment StartX=66.6 StartY=166.4 StartZ=0 EndX=66.6 EndY=172.4 EndZ=0
    g24: LineSegment StartX=-68.4 StartY=172.4 StartZ=0 EndX=-168.4 EndY=172.4 EndZ=0
    g25: LineSegment StartX=-168.4 StartY=172.4 StartZ=0 EndX=-168.4 EndY=166.4 EndZ=0
    g26: LineSegment StartX=-168.4 StartY=166.4 StartZ=0 EndX=-68.4 EndY=166.4 EndZ=0
    g27: LineSegment StartX=-68.4 StartY=166.4 StartZ=0 EndX=-68.4 EndY=172.4 EndZ=0
    g28: LineSegment StartX=-68.4 StartY=157.4 StartZ=0 EndX=-168.4 EndY=157.4 EndZ=0
    g29: LineSegment StartX=-168.4 StartY=157.4 StartZ=0 EndX=-168.4 EndY=151.4 EndZ=0
    g30: LineSegment StartX=-168.4 StartY=151.4 StartZ=0 EndX=-68.4 EndY=151.4 EndZ=0
    g31: LineSegment StartX=-68.4 StartY=151.4 StartZ=0 EndX=-68.4 EndY=157.4 EndZ=0
    g32: LineSegment StartX=-68.4 StartY=85.43 StartZ=0 EndX=-168.4 EndY=85.43 EndZ=0
    g33: LineSegment StartX=-168.4 StartY=85.43 StartZ=0 EndX=-168.4 EndY=79.43 EndZ=0
    g34: LineSegment StartX=-168.4 StartY=79.43 StartZ=0 EndX=-68.4 EndY=79.43 EndZ=0
    g35: LineSegment StartX=-68.4 StartY=79.43 StartZ=0 EndX=-68.4 EndY=85.43 EndZ=0
  constraints (108):
    c: Coincident(g0,g1)
    c: Coincident(g1,g2)
    c: Coincident(g2,g3)
    c: Coincident(g3,g0)
    c: Horizontal(g0)
    c: Horizontal(g2)
    c: Vertical(g1)
    c: Vertical(g3)
    c: Coincident(g4,g5)
    c: Coincident(g5,g6)
    c: Coincident(g6,g7)
    c: Coincident(g7,g4)
    c: Horizontal(g4)
    c: Horizontal(g6)
    c: Vertical(g5)
    c: Vertical(g7)
    c: Coincident(g8,g9)
    c: Coincident(g9,g10)
    c: Coincident(g10,g11)
    c: Coincident(g11,g8)
    c: Horizontal(g8)
    c: Horizontal(g10)
    c: Vertical(g9)
    c: Vertical(g11)
    c: Coincident(g12,g13)
    c: Coincident(g13,g14)
    c: Coincident(g14,g15)
    c: Coincident(g15,g12)
    c: Horizontal(g12)
    c: Horizontal(g14)
    c: Vertical(g13)
    c: Vertical(g15)
    c: Coincident(g16,g17)
    c: Coincident(g17,g18)
    c: Coincident(g18,g19)
    c: Coincident(g19,g16)
    c: Horizontal(g16)
    c: Horizontal(g18)
    c: Vertical(g17)
    c: Vertical(g19)
    c: Coincident(g20,g21)
    c: Coincident(g21,g22)
    c: Coincident(g22,g23)
    c: Coincident(g23,g20)
    c: Horizontal(g20)
    c: Horizontal(g22)
    c: Vertical(g21)
    c: Vertical(g23)
    c: Coincident(g24,g25)
    c: Coincident(g25,g26)
    c: Coincident(g26,g27)
    c: Coincident(g27,g24)
    c: Horizontal(g24)
    c: Horizontal(g26)
    c: Vertical(g25)
    c: Vertical(g27)
    c: Coincident(g28,g29)
    c: Coincident(g29,g30)
    c: Coincident(g30,g31)
    c: Coincident(g31,g28)
    c: Horizontal(g28)
    c: Horizontal(g30)
    c: Vertical(g29)
    c: Vertical(g31)
    c: Coincident(g32,g33)
    c: Coincident(g33,g34)
    c: Coincident(g34,g35)
    c: Coincident(g35,g32)
    c: Horizontal(g32)
    c: Horizontal(g34)
    c: Vertical(g33)
    c: Vertical(g35)
    c: DistanceX(g-8,g10) = 5
    c: DistanceX(g9,g-7) = 5
    c: DistanceX(g-6,g14) = 5
    c: DistanceX(g13,g-5) = 5
    c: DistanceX(g-4,g34) = 5
    c: DistanceX(g33,g-3) = 5
    c: Vertical(g32,g28)
    c: Vertical(g28,g24)
    c: Vertical(g24,g28)
    c: Vertical(g28,g32)
    c: Vertical(g12,g16)
    c: Vertical(g16,g20)
    c: Vertical(g12,g16)
    c: Vertical(g16,g20)
    c: Vertical(g0,g4)
    c: Vertical(g4,g8)
    c: Vertical(g8,g4)
    c: Vertical(g4,g0)
    c: DistanceY(g-6,g12) = 3
    c: DistanceY(g14,g-6) = 3
    c: Horizontal(g8,g12)
    c: Horizontal(g12,g32)
    c: Horizontal(g33,g13)
    c: Horizontal(g13,g9)
    c: Horizontal(g5,g17)
    c: Horizontal(g17,g29)
    c: Horizontal(g25,g21)
    c: Horizontal(g21,g1)
    c: Horizontal(g4,g16)
    c: Horizontal(g16,g28)
    c: Horizontal(g24,g20)
    c: Horizontal(g20,g0)
    c: DistanceY(g-9,g20) = 3
    c: DistanceY(g22,g-9) = 3
    c: DistanceY(g-10,g16) = 3
    c: DistanceY(g18,g-10) = 3
FEATURE [PartDesign::Pocket] Pocket019  label="drive screws bottom pocket"
  BaseFeature = -> Pocket018
  Direction = (0,0,1)
  Length = 2.2
  Length2 = 5
  Profile = -> Sketch029
  ReferenceAxis = -> Sketch029 [N_Axis]
  Refine = true
  Suppressed = false
  Type = 0
FEATURE [Sketcher::SketchObject] Sketch030
  ArcFitTolerance = 1e-06
  AttachmentSupport = -> [Pocket019]
  ExternalGeometry = -> [Pocket019]
  FullyConstrained = true
  MakeInternals = false
  MapMode = 5
  Placement = pos=(0,0,0) rot=(1,0,0;3.14159rad)
  sketch-geometry (12):
    g0: Circle CenterX=-172.8 CenterY=-160.22 CenterZ=0 NormalX=0 NormalY=0 NormalZ=1 AngleXU=0 Radius=5
    g1: Circle CenterX=-94.1 CenterY=-160.22 CenterZ=0 NormalX=0 NormalY=0 NormalZ=1 AngleXU=0 Radius=5
    g2: Circle CenterX=-48.3 CenterY=-160.22 CenterZ=0 NormalX=0 NormalY=0 NormalZ=1 AngleXU=0 Radius=5
    g3: Circle CenterX=109.1 CenterY=-137.42 CenterZ=0 NormalX=0 NormalY=0 NormalZ=1 AngleXU=0 Radius=5
    g4: Circle CenterX=109.1 CenterY=-5.32 CenterZ=0 NormalX=0 NormalY=0 NormalZ=1 AngleXU=0 Radius=5
    g5: Circle CenterX=-48.3 CenterY=-5.32 CenterZ=0 NormalX=0 NormalY=0 NormalZ=1 AngleXU=0 Radius=5
    g6: Circle CenterX=-94.1 CenterY=-5.32 CenterZ=0 NormalX=0 NormalY=0 NormalZ=1 AngleXU=0 Radius=5
    g7: Circle CenterX=-114.4 CenterY=-5.32 CenterZ=0 NormalX=0 NormalY=0 NormalZ=1 AngleXU=0 Radius=5
    g8: Circle CenterX=-172.8 CenterY=-5.32 CenterZ=0 NormalX=0 NormalY=0 NormalZ=1 AngleXU=0 Radius=5
    g9: Circle CenterX=-172.8 CenterY=67.08 CenterZ=0 NormalX=0 NormalY=0 NormalZ=1 AngleXU=0 Radius=5
    g10: Circle CenterX=-48.3 CenterY=67.08 CenterZ=0 NormalX=0 NormalY=0 NormalZ=1 AngleXU=0 Radius=5
    g11: Circle CenterX=109.1 CenterY=67.08 CenterZ=0 NormalX=0 NormalY=0 NormalZ=1 AngleXU=0 Radius=5
  constraints (24):
    c: Diameter(g0) = 10
    c: Coincident(g0,g-14)
    c: Coincident(g1,g-13)
    c: Coincident(g2,g-12)
    c: Coincident(g3,g-11)
    c: Coincident(g4,g-9)
    c: Coincident(g5,g-8)
    c: Coincident(g6,g-7)
    c: Coincident(g7,g-6)
    c: Coincident(g8,g-4)
    c: Coincident(g9,g-3)
    c: Coincident(g10,g-5)
    c: Coincident(g11,g-10)
    c: Equal(g11,g10)
    c: Equal(g10,g9)
    c: Equal(g9,g8)
    c: Equal(g8,g7)
    c: Equal(g7,g6)
    c: Equal(g6,g5)
    c: Equal(g5,g4)
    c: Equal(g4,g3)
    c: Equal(g3,g2)
    c: Equal(g2,g1)
    c: Equal(g1,g0)
FEATURE [PartDesign::Pocket] Pocket020  label="motherboard standoffs bottom pocket"
  BaseFeature = -> Pocket019
  Direction = (0,0,1)
  Length = 6.5
  Length2 = 5
  Profile = -> Sketch030
  ReferenceAxis = -> Sketch030 [N_Axis]
  Refine = true
  Suppressed = false
  Type = 0
FEATURE [Sketcher::SketchObject] Sketch031
  ArcFitTolerance = 1e-06
  AttachmentSupport = -> [Pocket020]
  ExternalGeometry = -> [Pad016,Pad006]
  FullyConstrained = true
  MakeInternals = false
  MapMode = 5
  Placement = pos=(0,0,8) rot=(0,0,1;0rad)
  expr: Constraints[65] = Spreadsheet.magnet_thickness + 1 mm
  expr: Constraints[66] = Spreadsheet.magnet_thickness
  expr: Constraints[67] = Spreadsheet.magnet_diameter
  sketch-geometry (30):
    g0: LineSegment StartX=-136.425 StartY=-177.4 StartZ=0 EndX=-136.425 EndY=-180.45 EndZ=0
    g1: LineSegment StartX=-136.425 StartY=-180.45 StartZ=0 EndX=-130.375 EndY=-180.45 EndZ=0
    g2: LineSegment StartX=-130.375 StartY=-180.45 StartZ=0 EndX=-130.375 EndY=-177.4 EndZ=0
    g3: LineSegment StartX=-130.375 StartY=-177.4 StartZ=0 EndX=-136.425 EndY=-177.4 EndZ=0
    g4: LineSegment StartX=-106.425 StartY=-177.4 StartZ=0 EndX=-106.425 EndY=-180.45 EndZ=0
    g5: LineSegment StartX=-106.425 StartY=-180.45 StartZ=0 EndX=-100.375 EndY=-180.45 EndZ=0
    g6: LineSegment StartX=-100.375 StartY=-180.45 StartZ=0 EndX=-100.375 EndY=-177.4 EndZ=0
    g7: LineSegment StartX=-100.375 StartY=-177.4 StartZ=0 EndX=-106.425 EndY=-177.4 EndZ=0
    g8: LineSegment StartX=-1.425 StartY=-177.4 StartZ=0 EndX=-1.425 EndY=-180.45 EndZ=0
    g9: LineSegment StartX=-1.425 StartY=-180.45 StartZ=0 EndX=4.625 EndY=-180.45 EndZ=0
    g10: LineSegment StartX=4.625 StartY=-180.45 StartZ=0 EndX=4.625 EndY=-177.4 EndZ=0
    g11: LineSegment StartX=4.625 StartY=-177.4 StartZ=0 EndX=-1.425 EndY=-177.4 EndZ=0
    g12: LineSegment StartX=28.575 StartY=-177.4 StartZ=0 EndX=28.575 EndY=-180.45 EndZ=0
    g13: LineSegment StartX=28.575 StartY=-180.45 StartZ=0 EndX=34.625 EndY=-180.45 EndZ=0
    g14: LineSegment StartX=34.625 StartY=-180.45 StartZ=0 EndX=34.625 EndY=-177.4 EndZ=0
    g15: LineSegment StartX=34.625 StartY=-177.4 StartZ=0 EndX=28.575 EndY=-177.4 EndZ=0
    g16: LineSegment StartX=131.975 StartY=-177.4 StartZ=0 EndX=131.975 EndY=-180.45 EndZ=0
    g17: LineSegment StartX=131.975 StartY=-180.45 StartZ=0 EndX=138.025 EndY=-180.45 EndZ=0
    g18: LineSegment StartX=138.025 StartY=-180.45 StartZ=0 EndX=138.025 EndY=-177.4 EndZ=0
    g19: LineSegment StartX=138.025 StartY=-177.4 StartZ=0 EndX=131.975 EndY=-177.4 EndZ=0
    g20: LineSegment StartX=161.975 StartY=-177.4 StartZ=0 EndX=161.975 EndY=-180.45 EndZ=0
    g21: LineSegment StartX=161.975 StartY=-180.45 StartZ=0 EndX=168.025 EndY=-180.45 EndZ=0
    g22: LineSegment StartX=168.025 StartY=-180.45 StartZ=0 EndX=168.025 EndY=-177.4 EndZ=0
    g23: LineSegment StartX=168.025 StartY=-177.4 StartZ=0 EndX=161.975 EndY=-177.4 EndZ=0
    g24: GeomPoint [constr] X=165 Y=-177.4 Z=0
    g25: GeomPoint [constr] X=135 Y=-177.4 Z=0
    g26: GeomPoint [constr] X=31.6 Y=-177.4 Z=0
    g27: GeomPoint [constr] X=1.6 Y=-177.4 Z=0
    g28: GeomPoint [constr] X=-103.4 Y=-177.4 Z=0
    g29: GeomPoint [constr] X=-133.4 Y=-177.4 Z=0
  constraints (78):
    c: Coincident(g0,g1)
    c: Coincident(g1,g2)
    c: Coincident(g2,g3)
    c: Coincident(g3,g0)
    c: Vertical(g0)
    c: Vertical(g2)
    c: Horizontal(g1)
    c: Horizontal(g3)
    c: Coincident(g4,g5)
    c: Coincident(g5,g6)
    c: Coincident(g6,g7)
    c: Coincident(g7,g4)
    c: Vertical(g4)
    c: Vertical(g6)
    c: Horizontal(g5)
    c: Horizontal(g7)
    c: Coincident(g8,g9)
    c: Coincident(g9,g10)
    c: Coincident(g10,g11)
    c: Coincident(g11,g8)
    c: Vertical(g8)
    c: Vertical(g10)
    c: Horizontal(g9)
    c: Horizontal(g11)
    c: Coincident(g12,g13)
    c: Coincident(g13,g14)
    c: Coincident(g14,g15)
    c: Coincident(g15,g12)
    c: Vertical(g12)
    c: Vertical(g14)
    c: Horizontal(g13)
    c: Horizontal(g15)
    c: Coincident(g16,g17)
    c: Coincident(g17,g18)
    c: Coincident(g18,g19)
    c: Coincident(g19,g16)
    c: Vertical(g16)
    c: Vertical(g18)
    c: Horizontal(g17)
    c: Horizontal(g19)
    c: Coincident(g20,g21)
    c: Coincident(g21,g22)
    c: Coincident(g22,g23)
    c: Coincident(g23,g20)
    c: Vertical(g20)
    c: Vertical(g22)
    c: Horizontal(g21)
    c: Horizontal(g23)
    c: Symmetric(g23,g23,g24)
    c: Symmetric(g19,g19,g25)
    c: Symmetric(g15,g15,g26)
    c: Symmetric(g11,g11,g27)
    c: Symmetric(g7,g7,g28)
    c: Symmetric(g3,g3,g29)
    c: DistanceX(g29,g28) = 30
    c: DistanceX(g27,g26) = 30
    c: DistanceX(g25,g24) = 30
    c: Distance(g25,g-5) = 45
    c: Distance(g27,g-6) = 45
    c: Distance(g29,g-7) = 45
    c: Horizontal(g20,g16)
    c: Horizontal(g16,g12)
    c: Horizontal(g12,g8)
    c: Horizontal(g8,g4)
    c: Horizontal(g4,g0)
    c: Distance(g0,g-9) = 4.05
    c: DistanceY(g2,g2) = 3.05
    c: DistanceX(g3,g3) = 6.05
    c: Equal(g2,g6)
    c: Equal(g6,g10)
    c: Equal(g10,g14)
    c: Equal(g14,g18)
    c: Equal(g18,g22)
    c: Equal(g21,g17)
    c: Equal(g17,g13)
    c: Equal(g13,g9)
    c: Equal(g9,g5)
    c: Equal(g5,g1)
FEATURE [PartDesign::Pocket] Pocket021  label="front magnets - body"
  BaseFeature = -> Pocket020
  Direction = (0,0,-1)
  Length = 6.55
  Length2 = 0.1
  Profile = -> Sketch031
  ReferenceAxis = -> Sketch031 [N_Axis]
  Refine = true
  Suppressed = false
  Type = 4
  expr: Length = Spreadsheet.magnet_diameter + 0.5 mm
FEATURE [Sketcher::SketchObject] Sketch035
  ArcFitTolerance = 1e-06
  ExternalGeometry = -> [Pocket021]
  FullyConstrained = true
  MakeInternals = false
  MapMode = 5
  Placement = pos=(0,176.07,0) rot=(0,0.707107,0.707107;3.14159rad)
  expr: Constraints[38] = Spreadsheet.fan_mounting_hole_diameter
  sketch-geometry (19):
    g0: LineSegment [constr] StartX=-84.65 StartY=160.25 StartZ=0 EndX=-84.65 EndY=77.75 EndZ=0
    g1: LineSegment [constr] StartX=-84.65 StartY=77.75 StartZ=0 EndX=-2.15 EndY=77.75 EndZ=0
    g2: LineSegment [constr] StartX=-2.15 StartY=77.75 StartZ=0 EndX=-2.15 EndY=160.25 EndZ=0
    g3: LineSegment [constr] StartX=-2.15 StartY=160.25 StartZ=0 EndX=-84.65 EndY=160.25 EndZ=0
    g4: LineSegment [constr] StartX=-89.4 StartY=165 StartZ=0 EndX=-89.4 EndY=73 EndZ=0
    g5: LineSegment [constr] StartX=-89.4 StartY=73 StartZ=0 EndX=2.6 EndY=73 EndZ=0
    g6: LineSegment [constr] StartX=2.6 StartY=73 StartZ=0 EndX=2.6 EndY=165 EndZ=0
    g7: LineSegment [constr] StartX=2.6 StartY=165 StartZ=0 EndX=-89.4 EndY=165 EndZ=0
    g8: LineSegment [constr] StartX=2.6 StartY=165 StartZ=0 EndX=-89.4 EndY=73 EndZ=0
    g9: GeomPoint [constr] X=-43.4 Y=119 Z=0
    g10: GeomPoint [constr] X=-43.4 Y=176.5 Z=0
    g11: Circle CenterX=-84.65 CenterY=160.25 CenterZ=0 NormalX=0 NormalY=0 NormalZ=1 AngleXU=0 Radius=2.1
    g12: Circle CenterX=-84.65 CenterY=160.25 CenterZ=0 NormalX=0 NormalY=0 NormalZ=1 AngleXU=0 Radius=5
    g13: Circle CenterX=-2.15 CenterY=160.25 CenterZ=0 NormalX=0 NormalY=0 NormalZ=1 AngleXU=0 Radius=2.1
    g14: Circle CenterX=-2.15 CenterY=160.25 CenterZ=0 NormalX=0 NormalY=0 NormalZ=1 AngleXU=0 Radius=5
    g15: Circle CenterX=-2.15 CenterY=77.75 CenterZ=0 NormalX=0 NormalY=0 NormalZ=1 AngleXU=0 Radius=2.1
    g16: Circle CenterX=-2.15 CenterY=77.75 CenterZ=0 NormalX=0 NormalY=0 NormalZ=1 AngleXU=0 Radius=5
    g17: Circle CenterX=-84.65 CenterY=77.75 CenterZ=0 NormalX=0 NormalY=0 NormalZ=1 AngleXU=0 Radius=2.1
    g18: Circle CenterX=-84.65 CenterY=77.75 CenterZ=0 NormalX=0 NormalY=0 NormalZ=1 AngleXU=0 Radius=5
  constraints (43):
    c: Coincident(g0,g1)
    c: Coincident(g1,g2)
    c: Coincident(g2,g3)
    c: Coincident(g3,g0)
    c: Vertical(g0)
    c: Vertical(g2)
    c: Horizontal(g1)
    c: Horizontal(g3)
    c: Distance(g0,g2) = 82.5
    c: Distance(g1,g3) = 82.5
    c: Coincident(g4,g5)
    c: Coincident(g5,g6)
    c: Coincident(g6,g7)
    c: Coincident(g7,g4)
    c: Vertical(g4)
    c: Vertical(g6)
    c: Horizontal(g5)
    c: Horizontal(g7)
    c: DistanceX(g4,g6) = 92
    c: DistanceY(g4,g4) = 92
    c: Coincident(g8,g6)
    c: Coincident(g8,g4)
    c: Symmetric(g8,g8,g9)
    c: Symmetric(g0,g2,g9)
    c: Coincident(g11,g0)
    c: Coincident(g12,g0)
    c: Coincident(g13,g2)
    c: Coincident(g14,g2)
    c: Coincident(g15,g1)
    c: Coincident(g16,g1)
    c: Coincident(g17,g0)
    c: Coincident(g18,g0)
    c: Equal(g18,g16)
    c: Equal(g16,g14)
    c: Equal(g14,g12)
    c: Equal(g11,g13)
    c: Equal(g13,g15)
    c: Equal(g15,g17)
    c: Diameter(g11) = 4.2
    c: Diameter(g12) = 10
    c: Symmetric(g-3,g-3,g10)
    c: Vertical(g10,g9)
    c: Distance(g4,g-3) = 11.5
FEATURE [PartDesign::Pad] Pad018  label="rear fan mount holes support"
  BaseFeature = -> Pocket021
  Direction = (1e-16,1,-2e-16)
  Length = 4
  Length2 = 10
  Profile = -> Sketch035
  ReferenceAxis = -> Sketch035 [N_Axis]
  Refine = true
  Reversed = true
  Suppressed = false
  Type = 0
  expr: Length = Spreadsheet.wall_thickness
FEATURE [Sketcher::SketchObject] Sketch036
  ArcFitTolerance = 1e-06
  AttachmentSupport = -> [Pad018]
  ExternalGeometry = -> [Sketch035]
  FullyConstrained = true
  MakeInternals = false
  MapMode = 5
  Placement = pos=(0,176.07,0) rot=(0,0.707107,0.707107;3.14159rad)
  sketch-geometry (4):
    g0: Circle CenterX=-84.65 CenterY=77.75 CenterZ=0 NormalX=0 NormalY=0 NormalZ=1 AngleXU=0 Radius=2.1
    g1: Circle CenterX=-2.15 CenterY=77.75 CenterZ=0 NormalX=0 NormalY=0 NormalZ=1 AngleXU=0 Radius=2.1
    g2: Circle CenterX=-2.15 CenterY=160.25 CenterZ=0 NormalX=0 NormalY=0 NormalZ=1 AngleXU=0 Radius=2.1
    g3: Circle CenterX=-84.65 CenterY=160.25 CenterZ=0 NormalX=0 NormalY=0 NormalZ=1 AngleXU=0 Radius=2.1
  constraints (8):
    c: Coincident(g0,g-5)
    c: Equal(g0,g-5)
    c: Coincident(g1,g-6)
    c: Equal(g1,g-6)
    c: Coincident(g2,g-4)
    c: Equal(g2,g-4)
    c: Coincident(g3,g-3)
    c: Equal(g3,g-3)
FEATURE [PartDesign::Hole] Hole009  label="rear fan mount holes"
  BaseFeature = -> Pad018
  CustomThreadClearance = 0
  Depth = 4
  DepthType = 0
  Diameter = 5.5
  DrillForDepth = false
  DrillPoint = 0
  DrillPointAngle = 118
  HoleCutCountersinkAngle = 90
  HoleCutCustomValues = false
  HoleCutDepth = 1.5
  HoleCutDiameter = 10
  HoleCutType = 1
  ModelThread = false
  Profile = -> Sketch036
  Refine = true
  Suppressed = false
  Tapered = false
  TaperedAngle = 90
  ThreadClass = 0
  ThreadDepth = 4
  ThreadDepthType = 0
  ThreadDirection = 0
  ThreadFit = 0
  ThreadSize = 13
  ThreadType = 1
  Threaded = false
  UseCustomThreadClearance = false
  expr: Depth = Spreadsheet.wall_thickness
FEATURE [Sketcher::SketchObject] Sketch037
  ArcFitTolerance = 1e-06
  AttachmentSupport = -> [Hole009]
  ExternalGeometry = -> [Hole009]
  FullyConstrained = true
  MakeInternals = false
  MapMode = 5
  Placement = pos=(-215,0,0) rot=(0.57735,-0.57735,-0.57735;2.0944rad)
  expr: Constraints[46] = 7.1
  sketch-geometry (16):
    g0: LineSegment StartX=14.5 StartY=168 StartZ=0 EndX=-1.5 EndY=168 EndZ=0
    g1: LineSegment StartX=-1.5 StartY=168 StartZ=0 EndX=-1.5 EndY=8 EndZ=0
    g2: LineSegment StartX=-1.5 StartY=8 StartZ=0 EndX=14.5 EndY=8 EndZ=0
    g3: LineSegment StartX=14.5 StartY=8 StartZ=0 EndX=14.5 EndY=168 EndZ=0
    g4: Circle CenterX=10.5 CenterY=148 CenterZ=0 NormalX=0 NormalY=0 NormalZ=1 AngleXU=0 Radius=1.5
    g5: Circle CenterX=2.5 CenterY=148 CenterZ=0 NormalX=0 NormalY=0 NormalZ=1 AngleXU=0 Radius=1.5
    g6: Circle CenterX=10.5 CenterY=108 CenterZ=0 NormalX=0 NormalY=0 NormalZ=1 AngleXU=0 Radius=1.5
    g7: Circle CenterX=2.5 CenterY=108 CenterZ=0 NormalX=0 NormalY=0 NormalZ=1 AngleXU=0 Radius=1.5
    g8: Circle CenterX=2.5 CenterY=68 CenterZ=0 NormalX=0 NormalY=0 NormalZ=1 AngleXU=0 Radius=1.5
    g9: Circle CenterX=10.5 CenterY=68 CenterZ=0 NormalX=0 NormalY=0 NormalZ=1 AngleXU=0 Radius=1.5
    g10: Circle CenterX=10.5 CenterY=28 CenterZ=0 NormalX=0 NormalY=0 NormalZ=1 AngleXU=0 Radius=1.5
    g11: Circle CenterX=2.5 CenterY=28 CenterZ=0 NormalX=0 NormalY=0 NormalZ=1 AngleXU=0 Radius=1.5
    g12: LineSegment [constr] StartX=-1.5 StartY=158 StartZ=0 EndX=2.5 EndY=158 EndZ=0
    g13: LineSegment [constr] StartX=2.5 StartY=158 StartZ=0 EndX=10.5 EndY=158 EndZ=0
    g14: LineSegment [constr] StartX=10.5 StartY=158 StartZ=0 EndX=14.5 EndY=158 EndZ=0
    g15: Circle CenterX=-173 CenterY=165.4 CenterZ=0 NormalX=0 NormalY=0 NormalZ=1 AngleXU=0 Radius=1.5
  constraints (49):
    c: Coincident(g0,g1)
    c: Coincident(g1,g2)
    c: Coincident(g2,g3)
    c: Coincident(g3,g0)
    c: Horizontal(g0)
    c: Horizontal(g2)
    c: Vertical(g1)
    c: Vertical(g3)
    c: DistanceX(g1,g2) = 16
    c: PointOnObject(g1,g-3)
    c: Equal(g4,g6)
    c: Equal(g6,g9)
    c: Equal(g9,g10)
    c: Equal(g10,g5)
    c: Equal(g5,g7)
    c: Equal(g7,g8)
    c: Equal(g8,g11)
    c: Horizontal(g4,g5)
    c: Horizontal(g6,g7)
    c: Horizontal(g9,g8)
    c: Horizontal(g10,g11)
    c: DistanceY(g2,g10) = 20
    c: DistanceY(g10,g9) = 40
    c: DistanceY(g9,g6) = 40
    c: DistanceY(g6,g4) = 40
    c: Horizontal(g12)
    c: Coincident(g12,g13)
    c: Horizontal(g13)
    c: Coincident(g13,g14)
    c: PointOnObject(g14,g3)
    c: Horizontal(g14)
    c: Vertical(g10,g9)
    c: Vertical(g9,g6)
    c: Vertical(g6,g4)
    c: Vertical(g4,g13)
    c: Vertical(g12,g5)
    c: Vertical(g5,g7)
    c: Vertical(g7,g8)
    c: Vertical(g8,g11)
    c: Diameter(g5) = 3
    c: DistanceY(g14,g0) = 10
    c: PointOnObject(g12,g1)
    c: Equal(g12,g14)
    c: DistanceX(g12,g13) = 8
    c: DistanceX(g2,g-5) = 170
    c: Diameter(g15) = 3
    c: Distance(g15,g-4) = 7.1
    c: DistanceY(g1,g0) = 160
    c: Distance(g15,g-6) = 10.5
FEATURE [PartDesign::Hole] Hole010  label="left side wall and corner support holes"
  BaseFeature = -> Hole009
  CustomThreadClearance = 0
  Depth = 4
  DepthType = 0
  Diameter = 3.4
  DrillForDepth = false
  DrillPoint = 1
  DrillPointAngle = 118
  HoleCutCountersinkAngle = 90
  HoleCutCustomValues = false
  HoleCutDepth = 0
  HoleCutDiameter = 6.1
  HoleCutType = 2
  ModelThread = false
  Profile = -> Sketch037
  Refine = true
  Suppressed = false
  Tapered = false
  TaperedAngle = 90
  ThreadClass = 0
  ThreadDepth = 4
  ThreadDepthType = 0
  ThreadDirection = 0
  ThreadFit = 0
  ThreadSize = 9
  ThreadType = 1
  Threaded = false
  UseCustomThreadClearance = false
  expr: Depth = Spreadsheet.wall_thickness
FEATURE [Sketcher::SketchObject] Sketch038
  ArcFitTolerance = 1e-06
  AttachmentSupport = -> [Hole010]
  ExternalGeometry = -> [Hole010]
  FullyConstrained = true
  MakeInternals = false
  MapMode = 5
  Placement = pos=(215,0,0) rot=(0.57735,0.57735,0.57735;2.0944rad)
  sketch-geometry (16):
    g0: LineSegment StartX=1.5 StartY=168 StartZ=0 EndX=-14.5 EndY=168 EndZ=0
    g1: LineSegment StartX=-14.5 StartY=168 StartZ=0 EndX=-14.5 EndY=8 EndZ=0
    g2: LineSegment StartX=-14.5 StartY=8 StartZ=0 EndX=1.5 EndY=8 EndZ=0
    g3: LineSegment StartX=1.5 StartY=8 StartZ=0 EndX=1.5 EndY=168 EndZ=0
    g4: Circle CenterX=-2.5 CenterY=28 CenterZ=0 NormalX=0 NormalY=0 NormalZ=1 AngleXU=0 Radius=1.5
    g5: Circle CenterX=-10.5 CenterY=28 CenterZ=0 NormalX=0 NormalY=0 NormalZ=1 AngleXU=0 Radius=1.5
    g6: Circle CenterX=-2.5 CenterY=68 CenterZ=0 NormalX=0 NormalY=0 NormalZ=1 AngleXU=0 Radius=1.5
    g7: Circle CenterX=-10.5 CenterY=68 CenterZ=0 NormalX=0 NormalY=0 NormalZ=1 AngleXU=0 Radius=1.5
    g8: Circle CenterX=-2.5 CenterY=108 CenterZ=0 NormalX=0 NormalY=0 NormalZ=1 AngleXU=0 Radius=1.5
    g9: Circle CenterX=-10.5 CenterY=108 CenterZ=0 NormalX=0 NormalY=0 NormalZ=1 AngleXU=0 Radius=1.5
    g10: Circle CenterX=-2.5 CenterY=148 CenterZ=0 NormalX=0 NormalY=0 NormalZ=1 AngleXU=0 Radius=1.5
    g11: Circle CenterX=-10.5 CenterY=148 CenterZ=0 NormalX=0 NormalY=0 NormalZ=1 AngleXU=0 Radius=1.5
    g12: Circle CenterX=173 CenterY=165.4 CenterZ=0 NormalX=0 NormalY=0 NormalZ=1 AngleXU=0 Radius=1.5
    g13: LineSegment [constr] StartX=-14.5 StartY=168 StartZ=0 EndX=-10.5 EndY=168 EndZ=0
    g14: LineSegment [constr] StartX=-10.5 StartY=168 StartZ=0 EndX=-2.5 EndY=168 EndZ=0
    g15: LineSegment [constr] StartX=-2.5 StartY=168 StartZ=0 EndX=1.5 EndY=168 EndZ=0
  constraints (48):
    c: Coincident(g0,g1)
    c: Coincident(g1,g2)
    c: Coincident(g2,g3)
    c: Coincident(g3,g0)
    c: Horizontal(g0)
    c: Horizontal(g2)
    c: Vertical(g1)
    c: Vertical(g3)
    c: Equal(g10,g11)
    c: Equal(g11,g9)
    c: Equal(g9,g8)
    c: Equal(g8,g6)
    c: Equal(g6,g7)
    c: Equal(g7,g4)
    c: Equal(g4,g5)
    c: Diameter(g11) = 3
    c: DistanceX(g0,g0) = 16
    c: Horizontal(g10,g11)
    c: Horizontal(g8,g9)
    c: Horizontal(g6,g7)
    c: Horizontal(g4,g5)
    c: Vertical(g4,g6)
    c: Vertical(g6,g8)
    c: Vertical(g8,g10)
    c: Vertical(g5,g7)
    c: Vertical(g7,g9)
    c: Vertical(g9,g11)
    c: DistanceY(g1,g0) = 160
    c: DistanceY(g2,g4) = 20
    c: DistanceY(g4,g6) = 40
    c: DistanceY(g6,g8) = 40
    c: DistanceY(g8,g10) = 40
    c: PointOnObject(g2,g-3)
    c: DistanceX(g-4,g1) = 170
    c: Diameter(g12) = 3
    c: Horizontal(g13)
    c: Coincident(g13,g14)
    c: Coincident(g14,g15)
    c: PointOnObject(g15,g3)
    c: Horizontal(g15)
    c: Horizontal(g14)
    c: Equal(g15,g13)
    c: DistanceX(g13,g14) = 8
    c: Vertical(g10,g14)
    c: Vertical(g11,g13)
    c: Coincident(g0,g13)
    c: Distance(g12,g-5) = 10.5
    c: DistanceY(g12,g-5) = 7.1
FEATURE [PartDesign::Hole] Hole011  label="right side wall and corner support holes"
  BaseFeature = -> Hole010
  CustomThreadClearance = 0
  Depth = 4
  DepthType = 0
  Diameter = 3.4
  DrillForDepth = false
  DrillPoint = 1
  DrillPointAngle = 118
  HoleCutCountersinkAngle = 90
  HoleCutCustomValues = false
  HoleCutDepth = 0
  HoleCutDiameter = 6.1
  HoleCutType = 2
  ModelThread = false
  Profile = -> Sketch038
  Refine = true
  Suppressed = false
  Tapered = false
  TaperedAngle = 90
  ThreadClass = 0
  ThreadDepth = 4
  ThreadDepthType = 0
  ThreadDirection = 0
  ThreadFit = 0
  ThreadSize = 9
  ThreadType = 1
  Threaded = false
  UseCustomThreadClearance = false
  expr: Depth = Spreadsheet.wall_thickness
FEATURE [Sketcher::SketchObject] Sketch039
  ArcFitTolerance = 1e-06
  AttachmentSupport = -> [Hole011]
  ExternalGeometry = -> [Hole011]
  FullyConstrained = true
  MakeInternals = false
  MapMode = 5
  Placement = pos=(0,187.5,0) rot=(0,0.707107,0.707107;3.14159rad)
  sketch-geometry (6):
    g0: Circle CenterX=200.5 CenterY=165.4 CenterZ=0 NormalX=0 NormalY=0 NormalZ=1 AngleXU=0 Radius=1.5
    g1: Circle CenterX=-200.5 CenterY=165.4 CenterZ=0 NormalX=0 NormalY=0 NormalZ=1 AngleXU=0 Radius=1.5
    g2: GeomPoint [constr] X=-213.65 Y=165.4 Z=0
    g3: LineSegment [constr] StartX=-213.65 StartY=165.4 StartZ=0 EndX=-211 EndY=165.4 EndZ=0
    g4: GeomPoint [constr] X=213.65 Y=165.4 Z=0
    g5: LineSegment [constr] StartX=213.65 StartY=165.4 StartZ=0 EndX=211 EndY=165.4 EndZ=0
  constraints (14):
    c: Diameter(g0) = 3
    c: Diameter(g1) = 3
    c: Symmetric(g-6,g-6,g2)
    c: Coincident(g3,g2)
    c: PointOnObject(g3,g-7)
    c: Horizontal(g3)
    c: Horizontal(g1,g3)
    c: DistanceX(g3,g1) = 10.5
    c: Symmetric(g-4,g-4,g4)
    c: Coincident(g5,g4)
    c: PointOnObject(g5,g-5)
    c: Horizontal(g4,g5)
    c: Horizontal(g5,g0)
    c: DistanceX(g0,g5) = 10.5
FEATURE [PartDesign::Hole] Hole012  label="rear corner support holes"
  BaseFeature = -> Hole011
  CustomThreadClearance = 0
  Depth = 4
  DepthType = 0
  Diameter = 3.4
  DrillForDepth = false
  DrillPoint = 1
  DrillPointAngle = 118
  HoleCutCountersinkAngle = 90
  HoleCutCustomValues = false
  HoleCutDepth = 0
  HoleCutDiameter = 6.1
  HoleCutType = 2
  ModelThread = false
  Profile = -> Sketch039
  Refine = true
  Suppressed = false
  Tapered = false
  TaperedAngle = 90
  ThreadClass = 0
  ThreadDepth = 4
  ThreadDepthType = 0
  ThreadDirection = 0
  ThreadFit = 0
  ThreadSize = 9
  ThreadType = 1
  Threaded = false
  UseCustomThreadClearance = false
  expr: Depth = Spreadsheet.wall_thickness
FEATURE [PartDesign::Pocket] Pocket022  label="bottom shaper"
  BaseFeature = -> Hole012
  Direction = (0,0,-1)
  Length = 8
  Length2 = 122
  Profile = -> Sketch041
  ReferenceAxis = -> Sketch041 [N_Axis]
  Refine = true
  Suppressed = false
  Type = 4
  expr: Length = Spreadsheet.bottom_thickness
FEATURE [Sketcher::SketchObject] Sketch042
  ArcFitTolerance = 1e-06
  AttachmentSupport = -> [Pocket022]
  ExternalGeometry = -> [Pocket022]
  FullyConstrained = true
  MakeInternals = false
  MapMode = 5
  Placement = pos=(-215,0,0) rot=(0.57735,-0.57735,-0.57735;2.0944rad)
  sketch-geometry (14):
    g0: Circle CenterX=-158.07 CenterY=2.2 CenterZ=0 NormalX=0 NormalY=0 NormalZ=1 AngleXU=0 Radius=1
    g1: Circle CenterX=-51.0233 CenterY=2.2 CenterZ=0 NormalX=0 NormalY=0 NormalZ=1 AngleXU=0 Radius=1
    g2: Circle CenterX=-104.547 CenterY=2.2 CenterZ=0 NormalX=0 NormalY=0 NormalZ=1 AngleXU=0 Radius=1
    g3: Circle CenterX=116.5 CenterY=2.2 CenterZ=0 NormalX=0 NormalY=0 NormalZ=1 AngleXU=0 Radius=1
    g4: Circle CenterX=169.5 CenterY=2.2 CenterZ=0 NormalX=0 NormalY=0 NormalZ=1 AngleXU=0 Radius=1
    g5: Circle CenterX=2.5 CenterY=2.2 CenterZ=0 NormalX=0 NormalY=0 NormalZ=1 AngleXU=0 Radius=1
    g6: LineSegment [constr] StartX=2.5 StartY=2.2 StartZ=0 EndX=-51.0233 EndY=2.2 EndZ=0
    g7: LineSegment [constr] StartX=-51.0233 StartY=2.2 StartZ=0 EndX=-104.547 EndY=2.2 EndZ=0
    g8: LineSegment [constr] StartX=-104.547 StartY=2.2 StartZ=0 EndX=-158.07 EndY=2.2 EndZ=0
    g9: Circle CenterX=63.5 CenterY=2.2 CenterZ=0 NormalX=0 NormalY=0 NormalZ=1 AngleXU=0 Radius=1
    g10: Circle CenterX=10.5 CenterY=2.2 CenterZ=0 NormalX=0 NormalY=0 NormalZ=1 AngleXU=0 Radius=1
    g11: LineSegment [constr] StartX=169.5 StartY=2.2 StartZ=0 EndX=116.5 EndY=2.2 EndZ=0
    g12: LineSegment [constr] StartX=116.5 StartY=2.2 StartZ=0 EndX=63.5 EndY=2.2 EndZ=0
    g13: LineSegment [constr] StartX=10.5 StartY=2.2 StartZ=0 EndX=63.5 EndY=2.2 EndZ=0
  constraints (36):
    c: Diameter(g0) = 2
    c: Diameter(g1) = 2
    c: Diameter(g2) = 2
    c: Diameter(g3) = 2
    c: Diameter(g4) = 2
    c: Diameter(g5) = 2
    c: Horizontal(g0,g2)
    c: Horizontal(g2,g1)
    c: Horizontal(g1,g5)
    c: Horizontal(g5,g3)
    c: Horizontal(g3,g4)
    c: Distance(g0,g-3) = 2.2
    c: Distance(g0,g-4) = 18
    c: Vertical(g-5,g5)
    c: Coincident(g6,g5)
    c: Coincident(g6,g1)
    c: Coincident(g7,g1)
    c: Coincident(g7,g2)
    c: Coincident(g8,g2)
    c: Coincident(g8,g0)
    c: Equal(g8,g7)
    c: Equal(g7,g6)
    c: Diameter(g9) = 2
    c: Diameter(g10) = 2
    c: Horizontal(g3,g9)
    c: Horizontal(g9,g10)
    c: Vertical(g10,g-6)
    c: DistanceX(g4,g-3) = 18
    c: Coincident(g11,g4)
    c: Coincident(g11,g3)
    c: Coincident(g11,g12)
    c: Coincident(g12,g9)
    c: Coincident(g13,g10)
    c: Coincident(g13,g9)
    c: Equal(g13,g12)
    c: Equal(g12,g11)
FEATURE [PartDesign::Hole] Hole013  label="left bottom screw holes"
  BaseFeature = -> Pocket022
  CustomThreadClearance = 0
  Depth = 8
  DepthType = 0
  Diameter = 2.4
  DrillForDepth = false
  DrillPoint = 0
  DrillPointAngle = 118
  HoleCutCountersinkAngle = 90
  HoleCutCustomValues = false
  HoleCutDepth = 1
  HoleCutDiameter = 4.2
  HoleCutType = 1
  ModelThread = false
  Profile = -> Sketch042
  Refine = true
  Suppressed = false
  Tapered = false
  TaperedAngle = 90
  ThreadClass = 0
  ThreadDepth = 8
  ThreadDepthType = 0
  ThreadDirection = 0
  ThreadFit = 0
  ThreadSize = 6
  ThreadType = 1
  Threaded = false
  UseCustomThreadClearance = false
  expr: Depth = Spreadsheet.wall_thickness * 2
FEATURE [Sketcher::SketchObject] Sketch043
  ArcFitTolerance = 1e-06
  AttachmentSupport = -> [Hole013]
  ExternalGeometry = -> [Hole013]
  FullyConstrained = true
  MakeInternals = false
  MapMode = 5
  Placement = pos=(215,0,0) rot=(0.57735,0.57735,0.57735;2.0944rad)
  sketch-geometry (14):
    g0: Circle CenterX=-169.5 CenterY=2.2 CenterZ=0 NormalX=0 NormalY=0 NormalZ=1 AngleXU=0 Radius=1.2
    g1: Circle CenterX=-116.5 CenterY=2.2 CenterZ=0 NormalX=0 NormalY=0 NormalZ=1 AngleXU=0 Radius=1.2
    g2: Circle CenterX=-63.5 CenterY=2.2 CenterZ=0 NormalX=0 NormalY=0 NormalZ=1 AngleXU=0 Radius=1.2
    g3: Circle CenterX=-10.5 CenterY=2.2 CenterZ=0 NormalX=0 NormalY=0 NormalZ=1 AngleXU=0 Radius=1.2
    g4: Circle CenterX=-2.5 CenterY=2.2 CenterZ=0 NormalX=0 NormalY=0 NormalZ=1 AngleXU=0 Radius=1.2
    g5: Circle CenterX=54.8333 CenterY=2.2 CenterZ=0 NormalX=0 NormalY=0 NormalZ=1 AngleXU=0 Radius=1.2
    g6: Circle CenterX=112.167 CenterY=2.2 CenterZ=0 NormalX=0 NormalY=0 NormalZ=1 AngleXU=0 Radius=1.2
    g7: Circle CenterX=169.5 CenterY=2.2 CenterZ=0 NormalX=0 NormalY=0 NormalZ=1 AngleXU=0 Radius=1.2
    g8: LineSegment [constr] StartX=-2.5 StartY=2.2 StartZ=0 EndX=54.8333 EndY=2.2 EndZ=0
    g9: LineSegment [constr] StartX=54.8333 StartY=2.2 StartZ=0 EndX=112.167 EndY=2.2 EndZ=0
    g10: LineSegment [constr] StartX=112.167 StartY=2.2 StartZ=0 EndX=169.5 EndY=2.2 EndZ=0
    g11: LineSegment [constr] StartX=-10.5 StartY=2.2 StartZ=0 EndX=-63.5 EndY=2.2 EndZ=0
    g12: LineSegment [constr] StartX=-63.5 StartY=2.2 StartZ=0 EndX=-116.5 EndY=2.2 EndZ=0
    g13: LineSegment [constr] StartX=-116.5 StartY=2.2 StartZ=0 EndX=-169.5 EndY=2.2 EndZ=0
  constraints (35):
    c: Coincident(g0,g-3)
    c: Equal(g0,g-3)
    c: DistanceX(g7,g-4) = 18
    c: Horizontal(g7,g6)
    c: Horizontal(g6,g5)
    c: Horizontal(g5,g4)
    c: Coincident(g8,g5)
    c: Coincident(g9,g5)
    c: Coincident(g9,g6)
    c: Coincident(g10,g6)
    c: Coincident(g10,g7)
    c: Equal(g10,g9)
    c: Equal(g9,g8)
    c: Equal(g4,g5)
    c: Equal(g5,g6)
    c: Equal(g6,g7)
    c: Coincident(g4,g8)
    c: Vertical(g-5,g4)
    c: Vertical(g-6,g3)
    c: Equal(g0,g1)
    c: Equal(g1,g2)
    c: Equal(g2,g3)
    c: Equal(g3,g4)
    c: Horizontal(g0,g1)
    c: Horizontal(g1,g2)
    c: Horizontal(g2,g3)
    c: Horizontal(g3,g4)
    c: Coincident(g11,g3)
    c: Coincident(g11,g2)
    c: Coincident(g11,g12)
    c: Coincident(g12,g1)
    c: Coincident(g12,g13)
    c: Coincident(g13,g0)
    c: Equal(g13,g12)
    c: Equal(g12,g11)
FEATURE [PartDesign::Hole] Hole014  label="right bottom screw holes"
  BaseFeature = -> Hole013
  CustomThreadClearance = 0
  Depth = 8
  DepthType = 0
  Diameter = 2.4
  DrillForDepth = false
  DrillPoint = 0
  DrillPointAngle = 118
  HoleCutCountersinkAngle = 90
  HoleCutCustomValues = false
  HoleCutDepth = 1
  HoleCutDiameter = 4.2
  HoleCutType = 1
  ModelThread = false
  Profile = -> Sketch043
  Refine = true
  Suppressed = false
  Tapered = false
  TaperedAngle = 90
  ThreadClass = 0
  ThreadDepth = 8
  ThreadDepthType = 0
  ThreadDirection = 0
  ThreadFit = 0
  ThreadSize = 6
  ThreadType = 1
  Threaded = false
  UseCustomThreadClearance = false
  expr: Depth = Spreadsheet.wall_thickness * 2
FEATURE [Sketcher::SketchObject] Sketch044
  ArcFitTolerance = 1e-06
  AttachmentSupport = -> [Hole014]
  ExternalGeometry = -> [Hole014]
  FullyConstrained = true
  MakeInternals = false
  MapMode = 5
  Placement = pos=(0,0,0) rot=(1,0,0;3.14159rad)
  expr: Constraints[153] = Spreadsheet.wall_thickness * 2
  expr: Constraints[154] = Spreadsheet.wall_thickness * 2
  expr: Constraints[185] = Spreadsheet.wall_thickness * 2
  expr: Constraints[72] = Spreadsheet.wall_thickness * 2
  expr: Constraints[73] = Spreadsheet.wall_thickness * 2
  sketch-geometry (84):
    g0: LineSegment StartX=-207 StartY=126.6 StartZ=0 EndX=-207 EndY=106.6 EndZ=0
    g1: LineSegment StartX=-207 StartY=106.6 StartZ=0 EndX=-197 EndY=106.6 EndZ=0
    g2: LineSegment StartX=-197 StartY=106.6 StartZ=0 EndX=-197 EndY=126.6 EndZ=0
    g3: LineSegment StartX=-197 StartY=126.6 StartZ=0 EndX=-207 EndY=126.6 EndZ=0
    g4: LineSegment StartX=-207 StartY=73.6 StartZ=0 EndX=-207 EndY=53.6 EndZ=0
    g5: LineSegment StartX=-207 StartY=53.6 StartZ=0 EndX=-187 EndY=53.6 EndZ=0
    g6: LineSegment StartX=-187 StartY=53.6 StartZ=0 EndX=-187 EndY=73.6 EndZ=0
    g7: LineSegment StartX=-187 StartY=73.6 StartZ=0 EndX=-207 EndY=73.6 EndZ=0
    g8: LineSegment StartX=-207 StartY=-40.9233 StartZ=0 EndX=-207 EndY=-60.9233 EndZ=0
    g9: LineSegment StartX=-207 StartY=-60.9233 StartZ=0 EndX=-187 EndY=-60.9233 EndZ=0
    g10: LineSegment StartX=-187 StartY=-60.9233 StartZ=0 EndX=-187 EndY=-40.9233 EndZ=0
    g11: LineSegment StartX=-187 StartY=-40.9233 StartZ=0 EndX=-207 EndY=-40.9233 EndZ=0
    g12: LineSegment StartX=-207 StartY=-94.4467 StartZ=0 EndX=-207 EndY=-114.447 EndZ=0
    g13: LineSegment StartX=-207 StartY=-114.447 StartZ=0 EndX=-187 EndY=-114.447 EndZ=0
    g14: LineSegment StartX=-187 StartY=-114.447 StartZ=0 EndX=-187 EndY=-94.4467 EndZ=0
    g15: LineSegment StartX=-187 StartY=-94.4467 StartZ=0 EndX=-207 EndY=-94.4467 EndZ=0
    g16: LineSegment StartX=-207 StartY=179.5 StartZ=0 EndX=-207 EndY=159.5 EndZ=0
    g17: LineSegment StartX=-207 StartY=159.5 StartZ=0 EndX=-187 EndY=159.5 EndZ=0
    g18: LineSegment StartX=-187 StartY=159.5 StartZ=0 EndX=-187 EndY=179.5 EndZ=0
    g19: LineSegment StartX=-187 StartY=179.5 StartZ=0 EndX=-207 EndY=179.5 EndZ=0
    g20: LineSegment StartX=-207 StartY=20.6 StartZ=0 EndX=-207 EndY=-7.6 EndZ=0
    g21: LineSegment StartX=-207 StartY=-7.6 StartZ=0 EndX=-187 EndY=-7.6 EndZ=0
    g22: LineSegment StartX=-187 StartY=-7.6 StartZ=0 EndX=-187 EndY=20.6 EndZ=0
    g23: LineSegment StartX=-187 StartY=20.6 StartZ=0 EndX=-207 EndY=20.6 EndZ=0
    g24: LineSegment StartX=-207 StartY=-148.07 StartZ=0 EndX=-207 EndY=-168.07 EndZ=0
    g25: LineSegment StartX=-207 StartY=-168.07 StartZ=0 EndX=-187 EndY=-168.07 EndZ=0
    g26: LineSegment StartX=-187 StartY=-168.07 StartZ=0 EndX=-187 EndY=-148.07 EndZ=0
    g27: LineSegment StartX=-187 StartY=-148.07 StartZ=0 EndX=-207 EndY=-148.07 EndZ=0
    g28: LineSegment StartX=207 StartY=-159.5 StartZ=0 EndX=187 EndY=-159.5 EndZ=0
    g29: LineSegment StartX=187 StartY=-159.5 StartZ=0 EndX=187 EndY=-179.5 EndZ=0
    g30: LineSegment StartX=187 StartY=-179.5 StartZ=0 EndX=207 EndY=-179.5 EndZ=0
    g31: LineSegment StartX=207 StartY=-179.5 StartZ=0 EndX=207 EndY=-159.5 EndZ=0
    g32: LineSegment StartX=207 StartY=-102.067 StartZ=0 EndX=187 EndY=-102.067 EndZ=0
    g33: LineSegment StartX=187 StartY=-102.067 StartZ=0 EndX=187 EndY=-122.067 EndZ=0
    g34: LineSegment StartX=187 StartY=-122.067 StartZ=0 EndX=207 EndY=-122.067 EndZ=0
    g35: LineSegment StartX=207 StartY=-122.067 StartZ=0 EndX=207 EndY=-102.067 EndZ=0
    g36: LineSegment StartX=207 StartY=-44.7333 StartZ=0 EndX=187 EndY=-44.7333 EndZ=0
    g37: LineSegment StartX=187 StartY=-44.7333 StartZ=0 EndX=187 EndY=-64.7333 EndZ=0
    g38: LineSegment StartX=187 StartY=-64.7333 StartZ=0 EndX=207 EndY=-64.7333 EndZ=0
    g39: LineSegment StartX=207 StartY=-64.7333 StartZ=0 EndX=207 EndY=-44.7333 EndZ=0
    g40: LineSegment StartX=207 StartY=20.6 StartZ=0 EndX=187 EndY=20.6 EndZ=0
    g41: LineSegment StartX=187 StartY=20.6 StartZ=0 EndX=187 EndY=-7.6 EndZ=0
    g42: LineSegment StartX=187 StartY=-7.6 StartZ=0 EndX=207 EndY=-7.6 EndZ=0
    g43: LineSegment StartX=207 StartY=-7.6 StartZ=0 EndX=207 EndY=20.6 EndZ=0
    g44: LineSegment StartX=207 StartY=73.6 StartZ=0 EndX=187 EndY=73.6 EndZ=0
    g45: LineSegment StartX=187 StartY=73.6 StartZ=0 EndX=187 EndY=53.6 EndZ=0
    g46: LineSegment StartX=187 StartY=53.6 StartZ=0 EndX=207 EndY=53.6 EndZ=0
    g47: LineSegment StartX=207 StartY=53.6 StartZ=0 EndX=207 EndY=73.6 EndZ=0
    g48: LineSegment StartX=207 StartY=126.6 StartZ=0 EndX=197 EndY=126.6 EndZ=0
    g49: LineSegment StartX=197 StartY=126.6 StartZ=0 EndX=197 EndY=106.6 EndZ=0
    g50: LineSegment StartX=197 StartY=106.6 StartZ=0 EndX=207 EndY=106.6 EndZ=0
    g51: LineSegment StartX=207 StartY=106.6 StartZ=0 EndX=207 EndY=126.6 EndZ=0
    g52: LineSegment StartX=207 StartY=179.5 StartZ=0 EndX=187 EndY=179.5 EndZ=0
    g53: LineSegment StartX=187 StartY=179.5 StartZ=0 EndX=187 EndY=159.5 EndZ=0
    g54: LineSegment StartX=187 StartY=159.5 StartZ=0 EndX=207 EndY=159.5 EndZ=0
    g55: LineSegment StartX=207 StartY=159.5 StartZ=0 EndX=207 EndY=179.5 EndZ=0
    g56: LineSegment StartX=128.9 StartY=-159.5 StartZ=0 EndX=128.9 EndY=-179.5 EndZ=0
    g57: LineSegment StartX=128.9 StartY=-179.5 StartZ=0 EndX=148.9 EndY=-179.5 EndZ=0
    g58: LineSegment StartX=148.9 StartY=-179.5 StartZ=0 EndX=148.9 EndY=-159.5 EndZ=0
    g59: LineSegment StartX=148.9 StartY=-159.5 StartZ=0 EndX=128.9 EndY=-159.5 EndZ=0
    g60: LineSegment StartX=-61.5 StartY=-148.07 StartZ=0 EndX=-61.5 EndY=-168.07 EndZ=0
    g61: LineSegment StartX=-61.5 StartY=-168.07 StartZ=0 EndX=-25.03 EndY=-168.07 EndZ=0
    g62: LineSegment StartX=-25.03 StartY=-168.07 StartZ=0 EndX=-25.03 EndY=-148.07 EndZ=0
    g63: LineSegment StartX=-25.03 StartY=-148.07 StartZ=0 EndX=-61.5 EndY=-148.07 EndZ=0
    g64: LineSegment StartX=74.99 StartY=-148.07 StartZ=0 EndX=54.99 EndY=-148.07 EndZ=0
    g65: LineSegment StartX=54.99 StartY=-148.07 StartZ=0 EndX=54.99 EndY=-168.07 EndZ=0
    g66: LineSegment StartX=54.99 StartY=-168.07 StartZ=0 EndX=74.99 EndY=-168.07 EndZ=0
    g67: LineSegment StartX=74.99 StartY=-168.07 StartZ=0 EndX=74.99 EndY=-148.07 EndZ=0
    g68: LineSegment StartX=24.98 StartY=-148.07 StartZ=0 EndX=4.98 EndY=-148.07 EndZ=0
    g69: LineSegment StartX=4.98 StartY=-148.07 StartZ=0 EndX=4.98 EndY=-168.07 EndZ=0
    g70: LineSegment StartX=4.98 StartY=-168.07 StartZ=0 EndX=24.98 EndY=-168.07 EndZ=0
    g71: LineSegment StartX=24.98 StartY=-168.07 StartZ=0 EndX=24.98 EndY=-148.07 EndZ=0
    g72: LineSegment StartX=-139.9 StartY=-148.07 StartZ=0 EndX=-159.9 EndY=-148.07 EndZ=0
    g73: LineSegment StartX=-159.9 StartY=-148.07 StartZ=0 EndX=-159.9 EndY=-168.07 EndZ=0
    g74: LineSegment StartX=-159.9 StartY=-168.07 StartZ=0 EndX=-139.9 EndY=-168.07 EndZ=0
    g75: LineSegment StartX=-139.9 StartY=-168.07 StartZ=0 EndX=-139.9 EndY=-148.07 EndZ=0
    g76: LineSegment StartX=-110.7 StartY=-148.07 StartZ=0 EndX=-110.7 EndY=-168.07 EndZ=0
    g77: LineSegment StartX=-110.7 StartY=-168.07 StartZ=0 EndX=-81.5 EndY=-168.07 EndZ=0
    g78: LineSegment StartX=-81.5 StartY=-168.07 StartZ=0 EndX=-81.5 EndY=-148.07 EndZ=0
    g79: LineSegment StartX=-81.5 StartY=-148.07 StartZ=0 EndX=-110.7 EndY=-148.07 EndZ=0
    g80: LineSegment StartX=128.9 StartY=-176.97 StartZ=0 EndX=128.9 EndY=-183.17 EndZ=0
    g81: LineSegment StartX=128.9 StartY=-183.17 StartZ=0 EndX=133.9 EndY=-183.17 EndZ=0
    g82: LineSegment StartX=133.9 StartY=-183.17 StartZ=0 EndX=133.9 EndY=-176.97 EndZ=0
    g83: LineSegment StartX=133.9 StartY=-176.97 StartZ=0 EndX=128.9 EndY=-176.97 EndZ=0
  constraints (252):
    c: Coincident(g0,g1)
    c: Coincident(g1,g2)
    c: Coincident(g2,g3)
    c: Coincident(g3,g0)
    c: Vertical(g0)
    c: Vertical(g2)
    c: Horizontal(g1)
    c: Horizontal(g3)
    c: Distance(g0,g2) = 10
    c: Distance(g1,g3) = 20
    c: Coincident(g4,g5)
    c: Coincident(g5,g6)
    c: Coincident(g6,g7)
    c: Coincident(g7,g4)
    c: Vertical(g4)
    c: Vertical(g6)
    c: Horizontal(g5)
    c: Horizontal(g7)
    c: Coincident(g8,g9)
    c: Coincident(g9,g10)
    c: Coincident(g10,g11)
    c: Coincident(g11,g8)
    c: Vertical(g8)
    c: Vertical(g10)
    c: Horizontal(g9)
    c: Horizontal(g11)
    c: Coincident(g12,g13)
    c: Coincident(g13,g14)
    c: Coincident(g14,g15)
    c: Coincident(g15,g12)
    c: Vertical(g12)
    c: Vertical(g14)
    c: Horizontal(g13)
    c: Horizontal(g15)
    c: Coincident(g16,g17)
    c: Coincident(g17,g18)
    c: Coincident(g18,g19)
    c: Coincident(g19,g16)
    c: Vertical(g16)
    c: Vertical(g18)
    c: Horizontal(g17)
    c: Horizontal(g19)
    c: Coincident(g20,g21)
    c: Coincident(g21,g22)
    c: Coincident(g22,g23)
    c: Coincident(g23,g20)
    c: Vertical(g20)
    c: Vertical(g22)
    c: Horizontal(g21)
    c: Horizontal(g23)
    c: Coincident(g24,g25)
    c: Coincident(g25,g26)
    c: Coincident(g26,g27)
    c: Coincident(g27,g24)
    c: Vertical(g24)
    c: Vertical(g26)
    c: Horizontal(g25)
    c: Horizontal(g27)
    c: Equal(g13,g12)
    c: Equal(g12,g9)
    c: Equal(g9,g8)
    c: Equal(g8,g21)
    c: Equal(g21,g5)
    c: Equal(g5,g4)
    c: Equal(g0,g17)
    c: Equal(g17,g27)
    c: Vertical(g24,g12)
    c: Vertical(g12,g8)
    c: Vertical(g8,g20)
    c: Vertical(g20,g4)
    c: Vertical(g4,g0)
    c: Vertical(g0,g16)
    c: Distance(g16,g-3) = 8
    c: DistanceY(g-3,g24) = 8
    c: DistanceY(g-4,g12) = 8
    c: DistanceY(g-5,g8) = 8
    c: DistanceY(g-6,g4) = 8
    c: DistanceY(g-7,g0) = 8
    c: DistanceY(g-8,g20) = 8
    c: DistanceY(g20,g-9) = 8
    c: Equal(g27,g26)
    c: Coincident(g28,g29)
    c: Coincident(g29,g30)
    c: Coincident(g30,g31)
    c: Coincident(g31,g28)
    c: Horizontal(g28)
    c: Horizontal(g30)
    c: Vertical(g29)
    c: Vertical(g31)
    c: Coincident(g32,g33)
    c: Coincident(g33,g34)
    c: Coincident(g34,g35)
    c: Coincident(g35,g32)
    c: Horizontal(g32)
    c: Horizontal(g34)
    c: Vertical(g33)
    c: Vertical(g35)
    c: Coincident(g36,g37)
    c: Coincident(g37,g38)
    c: Coincident(g38,g39)
    c: Coincident(g39,g36)
    c: Horizontal(g36)
    c: Horizontal(g38)
    c: Vertical(g37)
    c: Vertical(g39)
    c: Coincident(g40,g41)
    c: Coincident(g41,g42)
    c: Coincident(g42,g43)
    c: Coincident(g43,g40)
    c: Horizontal(g40)
    c: Horizontal(g42)
    c: Vertical(g41)
    c: Vertical(g43)
    c: Coincident(g44,g45)
    c: Coincident(g45,g46)
    c: Coincident(g46,g47)
    c: Coincident(g47,g44)
    c: Horizontal(g44)
    c: Horizontal(g46)
    c: Vertical(g45)
    c: Vertical(g47)
    c: Coincident(g48,g49)
    c: Coincident(g49,g50)
    c: Coincident(g50,g51)
    c: Coincident(g51,g48)
    c: Horizontal(g48)
    c: Horizontal(g50)
    c: Vertical(g49)
    c: Vertical(g51)
    c: Coincident(g52,g53)
    c: Coincident(g53,g54)
    c: Coincident(g54,g55)
    c: Coincident(g55,g52)
    c: Horizontal(g52)
    c: Horizontal(g54)
    c: Vertical(g53)
    c: Vertical(g55)
    c: Equal(g42,g46)
    c: Equal(g46,g47)
    c: Equal(g51,g54)
    c: Equal(g54,g39)
    c: Equal(g39,g38)
    c: Equal(g38,g35)
    c: Equal(g35,g34)
    c: Equal(g34,g31)
    c: Equal(g31,g30)
    c: Equal(g30,g25)
    c: Vertical(g28,g32)
    c: Vertical(g32,g36)
    c: Vertical(g36,g40)
    c: Vertical(g40,g44)
    c: Vertical(g44,g48)
    c: Vertical(g48,g52)
    c: DistanceY(g-13,g30) = 8
    c: DistanceX(g30,g-13) = 8
    c: DistanceY(g-14,g32) = 8
    c: DistanceY(g-15,g36) = 8
    c: DistanceY(g-19,g48) = 8
    c: DistanceY(g-18,g44) = 8
    c: DistanceY(g-16,g40) = 8
    c: DistanceY(g42,g-17) = 8
    c: Distance(g19,g-20) = 8
    c: Distance(g52,g-20) = 8
    c: Equal(g52,g55)
    c: Equal(g18,g19)
    c: Coincident(g56,g57)
    c: Coincident(g57,g58)
    c: Coincident(g58,g59)
    c: Coincident(g59,g56)
    c: Vertical(g56)
    c: Vertical(g58)
    c: Horizontal(g57)
    c: Horizontal(g59)
    c: Equal(g57,g56)
    c: Equal(g56,g30)
    c: Horizontal(g29,g57)
    c: DistanceX(g-12,g56) = 8
    c: Coincident(g60,g61)
    c: Coincident(g61,g62)
    c: Coincident(g62,g63)
    c: Coincident(g63,g60)
    c: Vertical(g60)
    c: Vertical(g62)
    c: Horizontal(g61)
    c: Horizontal(g63)
    c: Distance(g60,g-21) = 8
    c: Equal(g56,g62)
    c: Coincident(g64,g65)
    c: Coincident(g65,g66)
    c: Coincident(g66,g67)
    c: Coincident(g67,g64)
    c: Horizontal(g64)
    c: Horizontal(g66)
    c: Vertical(g65)
    c: Vertical(g67)
    c: Coincident(g68,g69)
    c: Coincident(g69,g70)
    c: Coincident(g70,g71)
    c: Coincident(g71,g68)
    c: Horizontal(g68)
    c: Horizontal(g70)
    c: Vertical(g69)
    c: Vertical(g71)
    c: Coincident(g72,g73)
    c: Coincident(g73,g74)
    c: Coincident(g74,g75)
    c: Coincident(g75,g72)
    c: Horizontal(g72)
    c: Horizontal(g74)
    c: Vertical(g73)
    c: Vertical(g75)
    c: Coincident(g76,g77)
    c: Coincident(g77,g78)
    c: Coincident(g78,g79)
    c: Coincident(g79,g76)
    c: Vertical(g76)
    c: Vertical(g78)
    c: Horizontal(g77)
    c: Equal(g73,g74)
    c: Equal(g74,g76)
    c: Equal(g70,g69)
    c: Equal(g69,g65)
    c: Equal(g65,g66)
    c: Equal(g66,g34)
    c: Horizontal(g65,g69)
    c: Horizontal(g69,g60)
    c: Horizontal(g60,g76)
    c: Horizontal(g76,g73)
    c: DistanceX(g-25,g66) = 10
    c: DistanceX(g-24,g70) = 10
    c: DistanceX(g76,g-23) = 10
    c: DistanceX(g73,g-22) = 10
    c: DistanceX(g-27,g61) = 10
    c: DistanceX(g60,g-26) = 10
    c: Equal(g78,g76)
    c: Equal(g76,g60)
    c: DistanceX(g-23,g77) = 15
    c: Coincident(g80,g81)
    c: Coincident(g81,g82)
    c: Coincident(g82,g83)
    c: Coincident(g83,g80)
    c: Vertical(g80)
    c: Vertical(g82)
    c: Horizontal(g81)
    c: Horizontal(g83)
    c: DistanceX(g-21,g80) = 8
    c: DistanceX(g80,g82) = 5
    c: DistanceY(g-28,g80) = 1
    c: DistanceY(g80,g-28) = 1
    c: Equal(g15,g27)
    c: Equal(g42,g38)
    c: DistanceX(g50,g50) = 10
FEATURE [Sketcher::SketchObject] Sketch045
  ArcFitTolerance = 1e-06
  ExternalGeometry = -> [Hole014]
  FullyConstrained = true
  MakeInternals = false
  MapMode = 5
  Placement = pos=(0,187.5,0) rot=(0,0.707107,0.707107;3.14159rad)
  sketch-geometry (2):
    g0: Circle CenterX=-197 CenterY=2.2 CenterZ=0 NormalX=0 NormalY=0 NormalZ=1 AngleXU=0 Radius=1
    g1: Circle CenterX=-138.9 CenterY=2.2 CenterZ=0 NormalX=0 NormalY=0 NormalZ=1 AngleXU=0 Radius=1
  constraints (6):
    c: Diameter(g0) = 2
    c: Diameter(g1) = 2
    c: Horizontal(g1,g0)
    c: Distance(g0,g-3) = 2.2
    c: DistanceX(g-3,g0) = 18
    c: DistanceX(g1,g-3) = 18
FEATURE [PartDesign::Hole] Hole015  label="PSU bottom screw holes"
  BaseFeature = -> Hole014
  CustomThreadClearance = 0
  Depth = 8
  DepthType = 0
  Diameter = 2.4
  DrillForDepth = false
  DrillPoint = 1
  DrillPointAngle = 118
  HoleCutCountersinkAngle = 90
  HoleCutCustomValues = false
  HoleCutDepth = 1
  HoleCutDiameter = 4.2
  HoleCutType = 1
  ModelThread = false
  Profile = -> Sketch045
  Refine = true
  Suppressed = false
  Tapered = false
  TaperedAngle = 90
  ThreadClass = 0
  ThreadDepth = 8
  ThreadDepthType = 0
  ThreadDirection = 0
  ThreadFit = 0
  ThreadSize = 6
  ThreadType = 1
  Threaded = false
  UseCustomThreadClearance = false
  expr: Depth = Spreadsheet.wall_thickness * 2
FEATURE [Sketcher::SketchObject] Sketch046
  ArcFitTolerance = 1e-06
  ExternalGeometry = -> [Hole015]
  FullyConstrained = true
  MakeInternals = false
  MapMode = 5
  Placement = pos=(0,176.07,0) rot=(0,0.707107,0.707107;3.14159rad)
  sketch-geometry (15):
    g0: Circle CenterX=197 CenterY=2.2 CenterZ=0 NormalX=0 NormalY=0 NormalZ=1 AngleXU=0 Radius=1
    g1: Circle CenterX=147.8 CenterY=2.2 CenterZ=0 NormalX=0 NormalY=0 NormalZ=1 AngleXU=0 Radius=1
    g2: Circle CenterX=-12.88 CenterY=2.2 CenterZ=0 NormalX=0 NormalY=0 NormalZ=1 AngleXU=0 Radius=1
    g3: Circle CenterX=49.4 CenterY=2.2 CenterZ=0 NormalX=0 NormalY=0 NormalZ=1 AngleXU=0 Radius=1
    g4: Circle CenterX=-112.9 CenterY=2.2 CenterZ=0 NormalX=0 NormalY=0 NormalZ=1 AngleXU=0 Radius=1
    g5: Circle CenterX=37.13 CenterY=2.2 CenterZ=0 NormalX=0 NormalY=0 NormalZ=1 AngleXU=0 Radius=1
    g6: Circle CenterX=98.6 CenterY=2.2 CenterZ=0 NormalX=0 NormalY=0 NormalZ=1 AngleXU=0 Radius=1
    g7: Circle CenterX=-62.89 CenterY=2.2 CenterZ=0 NormalX=0 NormalY=0 NormalZ=1 AngleXU=0 Radius=1
    g8: LineSegment [constr] StartX=49.4 StartY=2.2 StartZ=0 EndX=98.6 EndY=2.2 EndZ=0
    g9: LineSegment [constr] StartX=98.6 StartY=2.2 StartZ=0 EndX=147.8 EndY=2.2 EndZ=0
    g10: LineSegment [constr] StartX=147.8 StartY=2.2 StartZ=0 EndX=197 EndY=2.2 EndZ=0
    g11: LineSegment [constr] StartX=-112.9 StartY=2.2 StartZ=0 EndX=-62.89 EndY=2.2 EndZ=0
    g12: LineSegment [constr] StartX=-62.89 StartY=2.2 StartZ=0 EndX=-12.88 EndY=2.2 EndZ=0
    g13: LineSegment [constr] StartX=-12.88 StartY=2.2 StartZ=0 EndX=37.13 EndY=2.2 EndZ=0
    g14: Circle CenterX=5.12 CenterY=2.2 CenterZ=0 NormalX=0 NormalY=0 NormalZ=1 AngleXU=0 Radius=1
  constraints (39):
    c: Diameter(g0) = 2
    c: DistanceX(g0,g-3) = 18
    c: Distance(g0,g-3) = 2.2
    c: Diameter(g1) = 2
    c: Diameter(g2) = 2
    c: Diameter(g3) = 2
    c: Diameter(g4) = 2
    c: Diameter(g5) = 2
    c: Horizontal(g1,g3)
    c: Horizontal(g3,g5)
    c: Horizontal(g5,g2)
    c: Horizontal(g2,g4)
    c: DistanceX(g-5,g3) = 4
    c: DistanceX(g5,g-4) = 4
    c: Diameter(g6) = 2
    c: Diameter(g7) = 2
    c: Horizontal(g6,g7)
    c: Horizontal(g7,g0)
    c: Horizontal(g0,g1)
    c: Coincident(g8,g3)
    c: Coincident(g8,g6)
    c: Coincident(g8,g9)
    c: Coincident(g9,g1)
    c: Coincident(g9,g10)
    c: Coincident(g10,g0)
    c: Equal(g10,g8)
    c: Equal(g8,g9)
    c: DistanceX(g-3,g4) = 8
    c: Coincident(g11,g4)
    c: Coincident(g11,g7)
    c: Coincident(g11,g12)
    c: Coincident(g12,g2)
    c: Coincident(g12,g13)
    c: Coincident(g13,g5)
    c: Equal(g13,g12)
    c: Equal(g12,g11)
    c: Diameter(g14) = 2
    c: PointOnObject(g14,g12)
    c: DistanceX(g2,g14) = 18
FEATURE [PartDesign::Hole] Hole016  label="rear bottom screw holes"
  BaseFeature = -> Hole015
  CustomThreadClearance = 0
  Depth = 8
  DepthType = 0
  Diameter = 2.4
  DrillForDepth = false
  DrillPoint = 0
  DrillPointAngle = 118
  HoleCutCountersinkAngle = 90
  HoleCutCustomValues = false
  HoleCutDepth = 1
  HoleCutDiameter = 4.2
  HoleCutType = 1
  ModelThread = false
  Profile = -> Sketch046
  Refine = true
  Suppressed = false
  Tapered = false
  TaperedAngle = 90
  ThreadClass = 0
  ThreadDepth = 8
  ThreadDepthType = 0
  ThreadDirection = 0
  ThreadFit = 0
  ThreadSize = 6
  ThreadType = 1
  Threaded = false
  UseCustomThreadClearance = false
  expr: Depth = Spreadsheet.wall_thickness * 2
FEATURE [Sketcher::SketchObject] Sketch047
  ArcFitTolerance = 1e-06
  AttachmentSupport = -> [Hole016]
  ExternalGeometry = -> [Hole016]
  FullyConstrained = true
  MakeInternals = false
  MapMode = 5
  Placement = pos=(120.9,0,0) rot=(0.57735,-0.57735,-0.57735;2.0944rad)
  sketch-geometry (1):
    g0: Circle CenterX=-180.07 CenterY=2.2 CenterZ=0 NormalX=0 NormalY=0 NormalZ=1 AngleXU=0 Radius=1
  constraints (3):
    c: Diameter(g0) = 2
    c: Distance(g0,g-1) = 2.2
    c: DistanceX(g0,g-3) = 4
FEATURE [PartDesign::Hole] Hole017  label="PSU side bottom screw holes"
  BaseFeature = -> Hole016
  CustomThreadClearance = 0
  Depth = 8
  DepthType = 0
  Diameter = 2.4
  DrillForDepth = false
  DrillPoint = 0
  DrillPointAngle = 118
  HoleCutCountersinkAngle = 90
  HoleCutCustomValues = false
  HoleCutDepth = 1
  HoleCutDiameter = 4.2
  HoleCutType = 1
  ModelThread = false
  Profile = -> Sketch047
  Refine = true
  Suppressed = false
  Tapered = false
  TaperedAngle = 90
  ThreadClass = 0
  ThreadDepth = 8
  ThreadDepthType = 0
  ThreadDirection = 0
  ThreadFit = 0
  ThreadSize = 6
  ThreadType = 1
  Threaded = false
  UseCustomThreadClearance = false
  expr: Depth = Spreadsheet.wall_thickness * 2
FEATURE [PartDesign::Pocket] Pocket023  label="bottom pockets for bottom screws"
  BaseFeature = -> Hole017
  Direction = (0,0,1)
  Length = 4.4
  Length2 = 5
  Profile = -> Sketch044
  ReferenceAxis = -> Sketch044 [N_Axis]
  Refine = true
  Suppressed = false
  Type = 0
FEATURE [Sketcher::SketchObject] Sketch049
  ArcFitTolerance = 1e-06
  AttachmentSupport = -> [Pocket023]
  ExternalGeometry = -> [Pocket023]
  FullyConstrained = true
  MakeInternals = false
  MapMode = 5
  Placement = pos=(0,-187.5,0) rot=(1,0,0;1.5708rad)
  sketch-geometry (32):
    g0: Circle CenterX=180 CenterY=4 CenterZ=0 NormalX=0 NormalY=0 NormalZ=1 AngleXU=0 Radius=1.5
    g1: Circle CenterX=120 CenterY=4 CenterZ=0 NormalX=0 NormalY=0 NormalZ=1 AngleXU=0 Radius=1.5
    g2: Circle CenterX=46.6 CenterY=4 CenterZ=0 NormalX=0 NormalY=0 NormalZ=1 AngleXU=0 Radius=1.5
    g3: Circle CenterX=-13.4 CenterY=4 CenterZ=0 NormalX=0 NormalY=0 NormalZ=1 AngleXU=0 Radius=1.5
    g4: Circle CenterX=-88.4 CenterY=4 CenterZ=0 NormalX=0 NormalY=0 NormalZ=1 AngleXU=0 Radius=1.5
    g5: Circle CenterX=-148.4 CenterY=4 CenterZ=0 NormalX=0 NormalY=0 NormalZ=1 AngleXU=0 Radius=1.5
    g6: GeomPoint [constr] X=180 Y=14.5 Z=0
    g7: GeomPoint [constr] X=120 Y=14.5 Z=0
    g8: GeomPoint [constr] X=46.6 Y=14.5 Z=0
    g9: GeomPoint [constr] X=-13.4 Y=14.5 Z=0
    g10: GeomPoint [constr] X=-88.4 Y=14.5 Z=0
    g11: GeomPoint [constr] X=-148.4 Y=14.5 Z=0
    g12: Circle CenterX=-197 CenterY=2.2 CenterZ=0 NormalX=0 NormalY=0 NormalZ=1 AngleXU=0 Radius=1.5
    g13: GeomPoint [constr] X=-197 Y=1.8e-15 Z=0
    g14: Circle CenterX=86.3 CenterY=164.3 CenterZ=0 NormalX=0 NormalY=0 NormalZ=1 AngleXU=0 Radius=1
    g15: Circle CenterX=80.3 CenterY=164.3 CenterZ=0 NormalX=0 NormalY=0 NormalZ=1 AngleXU=0 Radius=1
    g16: Circle CenterX=86.3 CenterY=114.3 CenterZ=0 NormalX=0 NormalY=0 NormalZ=1 AngleXU=0 Radius=1
    g17: Circle CenterX=80.3 CenterY=114.3 CenterZ=0 NormalX=0 NormalY=0 NormalZ=1 AngleXU=0 Radius=1
    g18: Circle CenterX=86.3 CenterY=64.3 CenterZ=0 NormalX=0 NormalY=0 NormalZ=1 AngleXU=0 Radius=1
    g19: Circle CenterX=80.3 CenterY=64.3 CenterZ=0 NormalX=0 NormalY=0 NormalZ=1 AngleXU=0 Radius=1
    g20: Circle CenterX=-47.9 CenterY=164.3 CenterZ=0 NormalX=0 NormalY=0 NormalZ=1 AngleXU=0 Radius=1
    g21: Circle CenterX=-47.9 CenterY=114.3 CenterZ=0 NormalX=0 NormalY=0 NormalZ=1 AngleXU=0 Radius=1
    g22: Circle CenterX=-47.9 CenterY=64.3 CenterZ=0 NormalX=0 NormalY=0 NormalZ=1 AngleXU=0 Radius=1
    g23: Circle CenterX=-53.9 CenterY=164.3 CenterZ=0 NormalX=0 NormalY=0 NormalZ=1 AngleXU=0 Radius=1
    g24: Circle CenterX=-53.9 CenterY=114.3 CenterZ=0 NormalX=0 NormalY=0 NormalZ=1 AngleXU=0 Radius=1
    g25: Circle CenterX=-53.9 CenterY=64.3 CenterZ=0 NormalX=0 NormalY=0 NormalZ=1 AngleXU=0 Radius=1
    g26: GeomPoint [constr] X=83.3 Y=173 Z=0
    g27: GeomPoint [constr] X=-50.9 Y=173 Z=0
    g28: LineSegment [constr] StartX=-47.9 StartY=164.3 StartZ=0 EndX=-50.9 EndY=173 EndZ=0
    g29: LineSegment [constr] StartX=-50.9 StartY=173 StartZ=0 EndX=-53.9 EndY=164.3 EndZ=0
    g30: LineSegment [constr] StartX=86.3 StartY=164.3 StartZ=0 EndX=83.3 EndY=173 EndZ=0
    g31: LineSegment [constr] StartX=83.3 StartY=173 StartZ=0 EndX=80.3 EndY=164.3 EndZ=0
  constraints (74):
    c: Diameter(g0) = 3
    c: Diameter(g1) = 3
    c: Diameter(g2) = 3
    c: Diameter(g3) = 3
    c: Diameter(g4) = 3
    c: Diameter(g5) = 3
    c: Distance(g5,g-15) = 4
    c: Horizontal(g5,g4)
    c: Horizontal(g4,g3)
    c: Horizontal(g3,g2)
    c: Horizontal(g2,g1)
    c: Horizontal(g1,g0)
    c: Symmetric(g-5,g-6,g11)
    c: Symmetric(g-3,g-4,g10)
    c: Symmetric(g-8,g-7,g9)
    c: Symmetric(g-10,g-9,g8)
    c: Symmetric(g-12,g-11,g7)
    c: Symmetric(g-14,g-13,g6)
    c: Vertical(g0,g6)
    c: Vertical(g7,g1)
    c: Vertical(g8,g2)
    c: Vertical(g3,g9)
    c: Vertical(g10,g4)
    c: Vertical(g11,g5)
    c: Symmetric(g-19,g-19,g13)
    c: DistanceY(g13,g12) = 2.2
    c: Vertical(g12,g13)
    c: Equal(g12,g5)
    c: Vertical(g14,g16)
    c: Vertical(g16,g18)
    c: Vertical(g19,g17)
    c: Vertical(g17,g15)
    c: Vertical(g20,g21)
    c: Vertical(g21,g22)
    c: Vertical(g25,g24)
    c: Vertical(g24,g23)
    c: Horizontal(g14,g15)
    c: Horizontal(g15,g20)
    c: Horizontal(g20,g23)
    c: Horizontal(g24,g21)
    c: Horizontal(g21,g17)
    c: Horizontal(g17,g16)
    c: Horizontal(g18,g19)
    c: Horizontal(g19,g22)
    c: Horizontal(g22,g25)
    c: Equal(g23,g24)
    c: Equal(g24,g25)
    c: Equal(g25,g20)
    c: Equal(g20,g21)
    c: Equal(g21,g22)
    c: Equal(g22,g19)
    c: Equal(g19,g17)
    c: Equal(g17,g15)
    c: Equal(g15,g18)
    c: Equal(g18,g16)
    c: Equal(g16,g14)
    c: Diameter(g18) = 2
    c: DistanceX(g15,g14) = 6
    c: DistanceX(g23,g20) = 6
    c: DistanceY(g24,g23) = 50
    c: DistanceY(g25,g24) = 50
    c: Distance(g23,g-20) = 12.2
    c: Symmetric(g-21,g-22,g27)
    c: Coincident(g28,g20)
    c: Coincident(g28,g27)
    c: Coincident(g29,g27)
    c: Coincident(g29,g23)
    c: Equal(g28,g29)
    c: Symmetric(g-24,g-23,g26)
    c: Coincident(g30,g14)
    c: Coincident(g30,g26)
    c: Coincident(g31,g26)
    c: Coincident(g31,g15)
    c: Equal(g30,g31)
FEATURE [PartDesign::Hole] Hole019  label="front wall screws"
  BaseFeature = -> Pocket023
  CustomThreadClearance = 0
  Depth = 11
  DepthType = 0
  Diameter = 2.4
  DrillForDepth = false
  DrillPoint = 0
  DrillPointAngle = 118
  HoleCutCountersinkAngle = 90
  HoleCutCustomValues = false
  HoleCutDepth = 1
  HoleCutDiameter = 4.2
  HoleCutType = 1
  ModelThread = false
  Profile = -> Sketch049
  Refine = true
  Suppressed = false
  Tapered = false
  TaperedAngle = 90
  ThreadClass = 0
  ThreadDepth = 11
  ThreadDepthType = 0
  ThreadDirection = 0
  ThreadFit = 0
  ThreadSize = 6
  ThreadType = 1
  Threaded = false
  UseCustomThreadClearance = false
FEATURE [Sketcher::SketchObject] Sketch050
  ArcFitTolerance = 1e-06
  AttachmentSupport = -> [Hole019]
  ExternalGeometry = -> [Hole019]
  FullyConstrained = true
  MakeInternals = false
  MapMode = 5
  Placement = pos=(0,0,0) rot=(1,0,0;3.14159rad)
  expr: Constraints[94] = Spreadsheet.wall_thickness * 2
  expr: Constraints[95] = Spreadsheet.wall_thickness * 2
  sketch-geometry (32):
    g0: LineSegment StartX=-4 StartY=74.43 StartZ=0 EndX=-14 EndY=74.43 EndZ=0
    g1: LineSegment StartX=-14 StartY=74.43 StartZ=0 EndX=-14 EndY=10.6 EndZ=0
    g2: LineSegment StartX=-14 StartY=-168.07 StartZ=0 EndX=-4 EndY=-168.07 EndZ=0
    g3: LineSegment StartX=-4 StartY=-168.07 StartZ=0 EndX=-4 EndY=2.6 EndZ=0
    g4: LineSegment StartX=4 StartY=74.43 StartZ=0 EndX=4 EndY=10.6 EndZ=0
    g5: LineSegment StartX=4 StartY=-168.07 StartZ=0 EndX=14 EndY=-168.07 EndZ=0
    g6: LineSegment StartX=14 StartY=-168.07 StartZ=0 EndX=14 EndY=2.6 EndZ=0
    g7: LineSegment StartX=14 StartY=74.43 StartZ=0 EndX=4 EndY=74.43 EndZ=0
    g8: LineSegment StartX=182 StartY=20.6 StartZ=0 EndX=22 EndY=20.6 EndZ=0
    g9: LineSegment StartX=22 StartY=20.6 StartZ=0 EndX=22 EndY=10.6 EndZ=0
    g10: LineSegment StartX=22 StartY=10.6 StartZ=0 EndX=182 EndY=10.6 EndZ=0
    g11: LineSegment StartX=182 StartY=10.6 StartZ=0 EndX=182 EndY=20.6 EndZ=0
    g12: LineSegment StartX=182 StartY=2.6 StartZ=0 EndX=22 EndY=2.6 EndZ=0
    g13: LineSegment StartX=22 StartY=2.6 StartZ=0 EndX=22 EndY=-7.4 EndZ=0
    g14: LineSegment StartX=22 StartY=-7.4 StartZ=0 EndX=182 EndY=-7.4 EndZ=0
    g15: LineSegment StartX=182 StartY=-7.4 StartZ=0 EndX=182 EndY=2.6 EndZ=0
    g16: LineSegment StartX=-182 StartY=20.6 StartZ=0 EndX=-182 EndY=10.6 EndZ=0
    g17: LineSegment StartX=-182 StartY=10.6 StartZ=0 EndX=-22 EndY=10.6 EndZ=0
    g18: LineSegment StartX=-22 StartY=10.6 StartZ=0 EndX=-22 EndY=20.6 EndZ=0
    g19: LineSegment StartX=-22 StartY=20.6 StartZ=0 EndX=-182 EndY=20.6 EndZ=0
    g20: LineSegment StartX=-22 StartY=2.6 StartZ=0 EndX=-182 EndY=2.6 EndZ=0
    g21: LineSegment StartX=-182 StartY=2.6 StartZ=0 EndX=-182 EndY=-7.4 EndZ=0
    g22: LineSegment StartX=-182 StartY=-7.4 StartZ=0 EndX=-22 EndY=-7.4 EndZ=0
    g23: LineSegment StartX=-22 StartY=-7.4 StartZ=0 EndX=-22 EndY=2.6 EndZ=0
    g24: LineSegment StartX=14 StartY=2.6 StartZ=0 EndX=4 EndY=2.6 EndZ=0
    g25: LineSegment StartX=14 StartY=10.6 StartZ=0 EndX=4 EndY=10.6 EndZ=0
    g26: LineSegment StartX=14 StartY=10.6 StartZ=0 EndX=14 EndY=74.43 EndZ=0
    g27: LineSegment StartX=4 StartY=2.6 StartZ=0 EndX=4 EndY=-168.07 EndZ=0
    g28: LineSegment StartX=-14 StartY=10.6 StartZ=0 EndX=-4 EndY=10.6 EndZ=0
    g29: LineSegment StartX=-14 StartY=2.6 StartZ=0 EndX=-4 EndY=2.6 EndZ=0
    g30: LineSegment StartX=-14 StartY=2.6 StartZ=0 EndX=-14 EndY=-168.07 EndZ=0
    g31: LineSegment StartX=-4 StartY=10.6 StartZ=0 EndX=-4 EndY=74.43 EndZ=0
  constraints (99):
    c: Coincident(g0,g1)
    c: Coincident(g30,g2)
    c: Coincident(g2,g3)
    c: Coincident(g31,g0)
    c: Horizontal(g0)
    c: Horizontal(g2)
    c: Vertical(g1)
    c: Vertical(g3)
    c: Coincident(g27,g5)
    c: Coincident(g5,g6)
    c: Coincident(g26,g7)
    c: Coincident(g7,g4)
    c: Vertical(g4)
    c: Vertical(g6)
    c: Horizontal(g5)
    c: Horizontal(g7)
    c: Equal(g7,g0)
    c: Horizontal(g4,g0)
    c: Horizontal(g27,g2)
    c: Distance(g5,g-4) = 8
    c: Distance(g26,g-3) = 5
    c: Coincident(g8,g9)
    c: Coincident(g9,g10)
    c: Coincident(g10,g11)
    c: Coincident(g11,g8)
    c: Horizontal(g8)
    c: Horizontal(g10)
    c: Vertical(g9)
    c: Vertical(g11)
    c: Coincident(g12,g13)
    c: Coincident(g13,g14)
    c: Coincident(g14,g15)
    c: Coincident(g15,g12)
    c: Horizontal(g12)
    c: Horizontal(g14)
    c: Vertical(g13)
    c: Vertical(g15)
    c: Equal(g8,g14)
    c: Vertical(g10,g12)
    c: Equal(g11,g15)
    c: Horizontal(g-5,g8)
    c: Distance(g8,g10) = 10
    c: DistanceX(g8,g-5) = 5
    c: Coincident(g16,g17)
    c: Coincident(g17,g18)
    c: Coincident(g18,g19)
    c: Coincident(g19,g16)
    c: Vertical(g16)
    c: Vertical(g18)
    c: Horizontal(g17)
    c: Horizontal(g19)
    c: Coincident(g20,g21)
    c: Coincident(g21,g22)
    c: Coincident(g22,g23)
    c: Coincident(g23,g20)
    c: Horizontal(g20)
    c: Horizontal(g22)
    c: Vertical(g21)
    c: Vertical(g23)
    c: Equal(g19,g22)
    c: Equal(g16,g21)
    c: Vertical(g16,g20)
    c: Horizontal(g16,g-6)
    c: DistanceX(g-6,g16) = 5
    c: Distance(g16,g16) = 10
    c: Distance(g18,g1) = 8
    c: PointOnObject(g24,g27)
    c: Horizontal(g24)
    c: PointOnObject(g25,g26)
    c: Horizontal(g25)
    c: Horizontal(g9,g25)
    c: Horizontal(g12,g24)
    c: Coincident(g6,g24)
    c: PointOnObject(g26,g25)
    c: Coincident(g4,g25)
    c: PointOnObject(g27,g24)
    c: Distance(g8,g26) = 8
    c: Vertical(g26)
    c: Vertical(g25,g6)
    c: Equal(g24,g25)
    c: Equal(g25,g5)
    c: PointOnObject(g28,g31)
    c: Horizontal(g28)
    c: Horizontal(g29)
    c: Coincident(g29,g30)
    c: Coincident(g28,g1)
    c: Vertical(g30)
    c: Horizontal(g29,g20)
    c: Horizontal(g1,g17)
    c: Equal(g28,g29)
    c: Coincident(g3,g29)
    c: PointOnObject(g31,g28)
    c: Vertical(g31)
    c: Vertical(g28,g3)
    c: DistanceY(g12,g10) = 8
    c: DistanceY(g20,g16) = 8
    c: DistanceX(g0,g0) = 10
    c: Distance(g4,g0) = 8
    c: DistanceX(g19,g19) = 160
FEATURE [PartDesign::Pocket] Pocket024  label="bottom screws pocket"
  BaseFeature = -> Hole019
  Direction = (0,0,1)
  Length = 4.4
  Length2 = 5
  Profile = -> Sketch050
  ReferenceAxis = -> Sketch050 [N_Axis]
  Refine = true
  Suppressed = false
  Type = 0
FEATURE [Sketcher::SketchObject] Sketch051
  ArcFitTolerance = 1e-06
  AttachmentSupport = -> [Pocket024]
  ExternalGeometry = -> [Pocket024]
  FullyConstrained = true
  MakeInternals = false
  MapMode = 5
  Placement = pos=(4,0,0) rot=(0.57735,0.57735,0.57735;2.0944rad)
  sketch-geometry (13):
    g0: Circle CenterX=-71.43 CenterY=2.2 CenterZ=0 NormalX=0 NormalY=0 NormalZ=1 AngleXU=0 Radius=1
    g1: Circle CenterX=-13.6 CenterY=2.2 CenterZ=0 NormalX=0 NormalY=0 NormalZ=1 AngleXU=0 Radius=1
    g2: Circle CenterX=-42.515 CenterY=2.2 CenterZ=0 NormalX=0 NormalY=0 NormalZ=1 AngleXU=0 Radius=1
    g3: Circle CenterX=9.4 CenterY=2.2 CenterZ=0 NormalX=0 NormalY=0 NormalZ=1 AngleXU=0 Radius=1
    g4: Circle CenterX=160.07 CenterY=2.2 CenterZ=0 NormalX=0 NormalY=0 NormalZ=1 AngleXU=0 Radius=1
    g5: Circle CenterX=47.0675 CenterY=2.2 CenterZ=0 NormalX=0 NormalY=0 NormalZ=1 AngleXU=0 Radius=1
    g6: Circle CenterX=122.403 CenterY=2.2 CenterZ=0 NormalX=0 NormalY=0 NormalZ=1 AngleXU=0 Radius=1
    g7: Circle CenterX=84.735 CenterY=2.2 CenterZ=0 NormalX=0 NormalY=0 NormalZ=1 AngleXU=0 Radius=1
    g8: LineSegment [constr] StartX=9.4 StartY=2.2 StartZ=0 EndX=47.0675 EndY=2.2 EndZ=0
    g9: LineSegment [constr] StartX=47.0675 StartY=2.2 StartZ=0 EndX=84.735 EndY=2.2 EndZ=0
    g10: LineSegment [constr] StartX=84.735 StartY=2.2 StartZ=0 EndX=122.403 EndY=2.2 EndZ=0
    g11: LineSegment [constr] StartX=122.403 StartY=2.2 StartZ=0 EndX=160.07 EndY=2.2 EndZ=0
    g12: GeomPoint X=-74.43 Y=2.2 Z=0
  constraints (32):
    c: Diameter(g0) = 2
    c: Distance(g0,g-3) = 3
    c: Diameter(g1) = 2
    c: Diameter(g2) = 2
    c: Diameter(g3) = 2
    c: Diameter(g4) = 2
    c: Diameter(g5) = 2
    c: Diameter(g6) = 2
    c: Diameter(g7) = 2
    c: DistanceX(g1,g-5) = 3
    c: DistanceX(g-4,g3) = 12
    c: DistanceX(g4,g-6) = 8
    c: Symmetric(g0,g1,g2)
    c: Coincident(g8,g3)
    c: Coincident(g8,g5)
    c: Horizontal(g8)
    c: Coincident(g8,g9)
    c: Horizontal(g9)
    c: Coincident(g9,g10)
    c: Coincident(g10,g6)
    c: Horizontal(g10)
    c: Coincident(g10,g11)
    c: Coincident(g11,g4)
    c: Horizontal(g11)
    c: Equal(g11,g10)
    c: Equal(g10,g9)
    c: Equal(g9,g8)
    c: Horizontal(g0,g2)
    c: Horizontal(g1,g3)
    c: Coincident(g7,g9)
    c: Symmetric(g-3,g-3,g12)
    c: Horizontal(g0,g12)
FEATURE [PartDesign::Hole] Hole020  label="bottom vertical screws"
  BaseFeature = -> Pocket024
  CustomThreadClearance = 0
  Depth = 8
  DepthType = 0
  Diameter = 2.4
  DrillForDepth = false
  DrillPoint = 0
  DrillPointAngle = 118
  HoleCutCountersinkAngle = 90
  HoleCutCustomValues = false
  HoleCutDepth = 1
  HoleCutDiameter = 4.2
  HoleCutType = 1
  ModelThread = false
  Profile = -> Sketch051
  Refine = true
  Suppressed = false
  Tapered = false
  TaperedAngle = 90
  ThreadClass = 0
  ThreadDepth = 8
  ThreadDepthType = 0
  ThreadDirection = 0
  ThreadFit = 0
  ThreadSize = 6
  ThreadType = 1
  Threaded = false
  UseCustomThreadClearance = false
  expr: Depth = Spreadsheet.wall_thickness * 2
FEATURE [Sketcher::SketchObject] Sketch052
  ArcFitTolerance = 1e-06
  AttachmentSupport = -> [Hole020]
  ExternalGeometry = -> [Hole020]
  FullyConstrained = true
  MakeInternals = false
  MapMode = 5
  Placement = pos=(0,-10.6,0) rot=(1,0,0;1.5708rad)
  sketch-geometry (11):
    g0: Circle CenterX=9 CenterY=2.2 CenterZ=0 NormalX=0 NormalY=0 NormalZ=1 AngleXU=0 Radius=1
    g1: GeomPoint [constr] X=9 Y=0 Z=0
    g2: Circle CenterX=26 CenterY=2.2 CenterZ=0 NormalX=0 NormalY=0 NormalZ=1 AngleXU=0 Radius=1
    g3: Circle CenterX=178 CenterY=2.2 CenterZ=0 NormalX=0 NormalY=0 NormalZ=1 AngleXU=0 Radius=1
    g4: Circle CenterX=140 CenterY=2.2 CenterZ=0 NormalX=0 NormalY=0 NormalZ=1 AngleXU=0 Radius=1
    g5: Circle CenterX=102 CenterY=2.2 CenterZ=0 NormalX=0 NormalY=0 NormalZ=1 AngleXU=0 Radius=1
    g6: Circle CenterX=64 CenterY=2.2 CenterZ=0 NormalX=0 NormalY=0 NormalZ=1 AngleXU=0 Radius=1
    g7: LineSegment [constr] StartX=26 StartY=2.2 StartZ=0 EndX=64 EndY=2.2 EndZ=0
    g8: LineSegment [constr] StartX=64 StartY=2.2 StartZ=0 EndX=102 EndY=2.2 EndZ=0
    g9: LineSegment [constr] StartX=102 StartY=2.2 StartZ=0 EndX=140 EndY=2.2 EndZ=0
    g10: LineSegment [constr] StartX=140 StartY=2.2 StartZ=0 EndX=178 EndY=2.2 EndZ=0
  constraints (27):
    c: Diameter(g0) = 2
    c: Symmetric(g-3,g-3,g1)
    c: Vertical(g0,g1)
    c: DistanceY(g1,g0) = 2.2
    c: Diameter(g2) = 2
    c: Diameter(g3) = 2
    c: Diameter(g4) = 2
    c: Diameter(g5) = 2
    c: Diameter(g6) = 2
    c: Horizontal(g3,g4)
    c: Horizontal(g4,g5)
    c: Horizontal(g5,g6)
    c: Horizontal(g6,g2)
    c: Horizontal(g2,g0)
    c: DistanceX(g3,g-5) = 4
    c: DistanceX(g-4,g2) = 4
    c: Coincident(g7,g2)
    c: Coincident(g7,g6)
    c: Coincident(g7,g8)
    c: Coincident(g8,g5)
    c: Coincident(g8,g9)
    c: Coincident(g9,g4)
    c: Coincident(g9,g10)
    c: Coincident(g10,g3)
    c: Equal(g10,g9)
    c: Equal(g9,g8)
    c: Equal(g8,g7)
FEATURE [PartDesign::Hole] Hole021  label="bottom right screws"
  BaseFeature = -> Hole020
  CustomThreadClearance = 0
  Depth = 8
  DepthType = 0
  Diameter = 2.4
  DrillForDepth = false
  DrillPoint = 0
  DrillPointAngle = 118
  HoleCutCountersinkAngle = 90
  HoleCutCustomValues = false
  HoleCutDepth = 1
  HoleCutDiameter = 4.2
  HoleCutType = 1
  ModelThread = false
  Profile = -> Sketch052
  Refine = true
  Suppressed = false
  Tapered = false
  TaperedAngle = 90
  ThreadClass = 0
  ThreadDepth = 8
  ThreadDepthType = 0
  ThreadDirection = 0
  ThreadFit = 0
  ThreadSize = 6
  ThreadType = 1
  Threaded = false
  UseCustomThreadClearance = false
  expr: Depth = Spreadsheet.wall_thickness * 2
FEATURE [Sketcher::SketchObject] Sketch053
  ArcFitTolerance = 1e-06
  AttachmentSupport = -> [Hole021]
  ExternalGeometry = -> [Hole021]
  FullyConstrained = true
  MakeInternals = false
  MapMode = 5
  Placement = pos=(0,-2.6,0) rot=(0,0.707107,0.707107;3.14159rad)
  sketch-geometry (11):
    g0: Circle CenterX=9 CenterY=2.2 CenterZ=0 NormalX=0 NormalY=0 NormalZ=1 AngleXU=0 Radius=1
    g1: GeomPoint [constr] X=9 Y=0 Z=0
    g2: Circle CenterX=26 CenterY=2.2 CenterZ=0 NormalX=0 NormalY=0 NormalZ=1 AngleXU=0 Radius=1
    g3: Circle CenterX=178 CenterY=2.2 CenterZ=0 NormalX=0 NormalY=0 NormalZ=1 AngleXU=0 Radius=1
    g4: Circle CenterX=102 CenterY=2.2 CenterZ=0 NormalX=0 NormalY=0 NormalZ=1 AngleXU=0 Radius=1
    g5: Circle CenterX=140 CenterY=2.2 CenterZ=0 NormalX=0 NormalY=0 NormalZ=1 AngleXU=0 Radius=1
    g6: Circle CenterX=64 CenterY=2.2 CenterZ=0 NormalX=0 NormalY=0 NormalZ=1 AngleXU=0 Radius=1
    g7: LineSegment [constr] StartX=26 StartY=2.2 StartZ=0 EndX=64 EndY=2.2 EndZ=0
    g8: LineSegment [constr] StartX=64 StartY=2.2 StartZ=0 EndX=102 EndY=2.2 EndZ=0
    g9: LineSegment [constr] StartX=102 StartY=2.2 StartZ=0 EndX=140 EndY=2.2 EndZ=0
    g10: LineSegment [constr] StartX=140 StartY=2.2 StartZ=0 EndX=178 EndY=2.2 EndZ=0
  constraints (27):
    c: Diameter(g0) = 2
    c: Symmetric(g-3,g-3,g1)
    c: Vertical(g0,g1)
    c: DistanceY(g1,g0) = 2.2
    c: Diameter(g2) = 2
    c: Diameter(g3) = 2
    c: Diameter(g4) = 2
    c: Diameter(g5) = 2
    c: Diameter(g6) = 2
    c: DistanceX(g-5,g2) = 4
    c: DistanceX(g3,g-4) = 4
    c: Horizontal(g3,g5)
    c: Horizontal(g5,g4)
    c: Horizontal(g4,g6)
    c: Horizontal(g6,g2)
    c: Horizontal(g2,g0)
    c: Coincident(g7,g2)
    c: Coincident(g7,g6)
    c: Coincident(g7,g8)
    c: Coincident(g8,g4)
    c: Coincident(g8,g9)
    c: Coincident(g9,g5)
    c: Coincident(g9,g10)
    c: Coincident(g10,g3)
    c: Equal(g10,g9)
    c: Equal(g9,g8)
    c: Equal(g8,g7)
FEATURE [PartDesign::Hole] Hole022  label="bottom left screws"
  BaseFeature = -> Hole021
  CustomThreadClearance = 0
  Depth = 8
  DepthType = 0
  Diameter = 2.4
  DrillForDepth = false
  DrillPoint = 0
  DrillPointAngle = 118
  HoleCutCountersinkAngle = 90
  HoleCutCustomValues = false
  HoleCutDepth = 1
  HoleCutDiameter = 4.2
  HoleCutType = 1
  ModelThread = false
  Profile = -> Sketch053
  Refine = true
  Suppressed = false
  Tapered = false
  TaperedAngle = 90
  ThreadClass = 0
  ThreadDepth = 8
  ThreadDepthType = 0
  ThreadDirection = 0
  ThreadFit = 0
  ThreadSize = 6
  ThreadType = 1
  Threaded = false
  UseCustomThreadClearance = false
  expr: Depth = Spreadsheet.wall_thickness * 2
FEATURE [Sketcher::SketchObject] Sketch054
  ArcFitTolerance = 1e-06
  AttachmentSupport = -> [Hole022]
  ExternalGeometry = -> [Hole022]
  FullyConstrained = true
  MakeInternals = false
  MapMode = 5
  Placement = pos=(0,0,4.4) rot=(1,0,0;3.14159rad)
  sketch-geometry (116):
    g0: LineSegment StartX=74.1 StartY=20.6 StartZ=0 EndX=74.1 EndY=10.6 EndZ=0
    g1: LineSegment StartX=74.1 StartY=10.6 StartZ=0 EndX=91.9 EndY=10.6 EndZ=0
    g2: LineSegment StartX=91.9 StartY=10.6 StartZ=0 EndX=91.9 EndY=20.6 EndZ=0
    g3: LineSegment StartX=91.9 StartY=20.6 StartZ=0 EndX=74.1 EndY=20.6 EndZ=0
    g4: LineSegment StartX=112.1 StartY=20.6 StartZ=0 EndX=112.1 EndY=10.6 EndZ=0
    g5: LineSegment StartX=112.1 StartY=10.6 StartZ=0 EndX=129.9 EndY=10.6 EndZ=0
    g6: LineSegment StartX=129.9 StartY=10.6 StartZ=0 EndX=129.9 EndY=20.6 EndZ=0
    g7: LineSegment StartX=129.9 StartY=20.6 StartZ=0 EndX=112.1 EndY=20.6 EndZ=0
    g8: LineSegment StartX=150.1 StartY=20.6 StartZ=0 EndX=150.1 EndY=10.6 EndZ=0
    g9: LineSegment StartX=150.1 StartY=10.6 StartZ=0 EndX=159.9 EndY=10.6 EndZ=0
    g10: LineSegment StartX=159.9 StartY=10.6 StartZ=0 EndX=159.9 EndY=20.6 EndZ=0
    g11: LineSegment StartX=159.9 StartY=20.6 StartZ=0 EndX=150.1 EndY=20.6 EndZ=0
    g12: LineSegment StartX=44.1 StartY=20.6 StartZ=0 EndX=44.1 EndY=10.6 EndZ=0
    g13: LineSegment StartX=44.1 StartY=10.6 StartZ=0 EndX=53.9 EndY=10.6 EndZ=0
    g14: LineSegment StartX=53.9 StartY=10.6 StartZ=0 EndX=53.9 EndY=20.6 EndZ=0
    g15: LineSegment StartX=53.9 StartY=20.6 StartZ=0 EndX=44.1 EndY=20.6 EndZ=0
    g16: LineSegment StartX=159.9 StartY=2.6 StartZ=0 EndX=150.1 EndY=2.6 EndZ=0
    g17: LineSegment StartX=150.1 StartY=2.6 StartZ=0 EndX=150.1 EndY=-7.4 EndZ=0
    g18: LineSegment StartX=150.1 StartY=-7.4 StartZ=0 EndX=159.9 EndY=-7.4 EndZ=0
    g19: LineSegment StartX=159.9 StartY=-7.4 StartZ=0 EndX=159.9 EndY=2.6 EndZ=0
    g20: LineSegment StartX=129.9 StartY=2.6 StartZ=0 EndX=112.1 EndY=2.6 EndZ=0
    g21: LineSegment StartX=112.1 StartY=2.6 StartZ=0 EndX=112.1 EndY=-1.32 EndZ=0
    g22: LineSegment StartX=113.647 StartY=-7.4 StartZ=0 EndX=129.9 EndY=-7.4 EndZ=0
    g23: LineSegment StartX=129.9 StartY=-7.4 StartZ=0 EndX=129.9 EndY=2.6 EndZ=0
    g24: LineSegment StartX=91.9 StartY=2.6 StartZ=0 EndX=74.1 EndY=2.6 EndZ=0
    g25: LineSegment StartX=74.1 StartY=2.6 StartZ=0 EndX=74.1 EndY=-7.4 EndZ=0
    g26: LineSegment StartX=74.1 StartY=-7.4 StartZ=0 EndX=91.9 EndY=-7.4 EndZ=0
    g27: LineSegment StartX=91.9 StartY=-7.4 StartZ=0 EndX=91.9 EndY=2.6 EndZ=0
    g28: LineSegment StartX=53.9 StartY=2.6 StartZ=0 EndX=44.1 EndY=2.6 EndZ=0
    g29: LineSegment StartX=44.1 StartY=2.6 StartZ=0 EndX=44.1 EndY=-7.4 EndZ=0
    g30: LineSegment StartX=44.1 StartY=-7.4 StartZ=0 EndX=53.9 EndY=-7.4 EndZ=0
    g31: LineSegment StartX=53.9 StartY=-7.4 StartZ=0 EndX=53.9 EndY=2.6 EndZ=0
    g32: LineSegment StartX=-159.9 StartY=2.6 StartZ=0 EndX=-159.9 EndY=-7.4 EndZ=0
    g33: LineSegment StartX=-159.9 StartY=-7.4 StartZ=0 EndX=-150.1 EndY=-7.4 EndZ=0
    g34: LineSegment StartX=-150.1 StartY=-7.4 StartZ=0 EndX=-150.1 EndY=2.6 EndZ=0
    g35: LineSegment StartX=-150.1 StartY=2.6 StartZ=0 EndX=-159.9 EndY=2.6 EndZ=0
    g36: LineSegment StartX=-129.9 StartY=2.6 StartZ=0 EndX=-129.9 EndY=-7.4 EndZ=0
    g37: LineSegment StartX=-129.9 StartY=-7.4 StartZ=0 EndX=-118.947 EndY=-7.4 EndZ=0
    g38: LineSegment StartX=-112.1 StartY=-0.880405 StartZ=0 EndX=-112.1 EndY=2.6 EndZ=0
    g39: LineSegment StartX=-112.1 StartY=2.6 StartZ=0 EndX=-129.9 EndY=2.6 EndZ=0
    g40: LineSegment StartX=-74.1 StartY=2.6 StartZ=0 EndX=-91.9 EndY=2.6 EndZ=0
    g41: LineSegment StartX=-91.9 StartY=2.6 StartZ=0 EndX=-91.9 EndY=-0.830011 EndZ=0
    g42: LineSegment StartX=-89.5532 StartY=-7.4 StartZ=0 EndX=-74.1 EndY=-7.4 EndZ=0
    g43: LineSegment StartX=-74.1 StartY=-7.4 StartZ=0 EndX=-74.1 EndY=2.6 EndZ=0
    g44: LineSegment StartX=-44.1 StartY=2.6 StartZ=0 EndX=-53.9 EndY=2.6 EndZ=0
    g45: LineSegment StartX=-53.9 StartY=2.6 StartZ=0 EndX=-53.9 EndY=-7.4 EndZ=0
    g46: LineSegment StartX=-53.9 StartY=-7.4 StartZ=0 EndX=-52.8468 EndY=-7.4 EndZ=0
    g47: LineSegment StartX=-44.1 StartY=-2.60707 StartZ=0 EndX=-44.1 EndY=2.6 EndZ=0
    g48: ArcOfCircle CenterX=-114.4 CenterY=-5.32 CenterZ=0 NormalX=0 NormalY=0 NormalZ=1 AngleXU=0 Radius=5 StartAngle=1.0928 EndAngle=3.57063
    g49: ArcOfCircle CenterX=-94.1 CenterY=-5.32 CenterZ=0 NormalX=0 NormalY=0 NormalZ=1 AngleXU=0 Radius=5 StartAngle=5.85414 EndAngle=7.39838
    g50: ArcOfCircle CenterX=-48.3 CenterY=-5.32 CenterZ=0 NormalX=0 NormalY=0 NormalZ=1 AngleXU=0 Radius=5 StartAngle=0.573513 EndAngle=3.57063
    g51: LineSegment StartX=-44.1 StartY=20.6 StartZ=0 EndX=-53.9 EndY=20.6 EndZ=0
    g52: LineSegment StartX=-53.9 StartY=20.6 StartZ=0 EndX=-53.9 EndY=10.6 EndZ=0
    g53: LineSegment StartX=-53.9 StartY=10.6 StartZ=0 EndX=-44.1 EndY=10.6 EndZ=0
    g54: LineSegment StartX=-44.1 StartY=10.6 StartZ=0 EndX=-44.1 EndY=20.6 EndZ=0
    g55: LineSegment StartX=-74.1 StartY=20.6 StartZ=0 EndX=-91.9 EndY=20.6 EndZ=0
    g56: LineSegment StartX=-91.9 StartY=20.6 StartZ=0 EndX=-91.9 EndY=10.6 EndZ=0
    g57: LineSegment StartX=-91.9 StartY=10.6 StartZ=0 EndX=-74.1 EndY=10.6 EndZ=0
    g58: LineSegment StartX=-74.1 StartY=10.6 StartZ=0 EndX=-74.1 EndY=20.6 EndZ=0
    g59: LineSegment StartX=-112.1 StartY=20.6 StartZ=0 EndX=-129.9 EndY=20.6 EndZ=0
    g60: LineSegment StartX=-129.9 StartY=20.6 StartZ=0 EndX=-129.9 EndY=10.6 EndZ=0
    g61: LineSegment StartX=-129.9 StartY=10.6 StartZ=0 EndX=-112.1 EndY=10.6 EndZ=0
    g62: LineSegment StartX=-112.1 StartY=10.6 StartZ=0 EndX=-112.1 EndY=20.6 EndZ=0
    g63: LineSegment StartX=-150.1 StartY=20.6 StartZ=0 EndX=-159.9 EndY=20.6 EndZ=0
    g64: LineSegment StartX=-159.9 StartY=20.6 StartZ=0 EndX=-159.9 EndY=10.6 EndZ=0
    g65: LineSegment StartX=-159.9 StartY=10.6 StartZ=0 EndX=-150.1 EndY=10.6 EndZ=0
    g66: LineSegment StartX=-150.1 StartY=10.6 StartZ=0 EndX=-150.1 EndY=20.6 EndZ=0
    g67: LineSegment StartX=4 StartY=146.4 StartZ=0 EndX=4 EndY=128.515 EndZ=0
    g68: LineSegment StartX=4 StartY=128.515 StartZ=0 EndX=14 EndY=128.515 EndZ=0
    g69: LineSegment StartX=14 StartY=128.515 StartZ=0 EndX=14 EndY=146.4 EndZ=0
    g70: LineSegment StartX=14 StartY=146.4 StartZ=0 EndX=4 EndY=146.4 EndZ=0
    g71: LineSegment StartX=4 StartY=108.315 StartZ=0 EndX=4 EndY=90.43 EndZ=0
    g72: LineSegment StartX=4 StartY=90.43 StartZ=0 EndX=14 EndY=90.43 EndZ=0
    g73: LineSegment StartX=14 StartY=90.43 StartZ=0 EndX=14 EndY=108.315 EndZ=0
    g74: LineSegment StartX=14 StartY=108.315 StartZ=0 EndX=4 EndY=108.315 EndZ=0
    g75: LineSegment StartX=-4 StartY=108.315 StartZ=0 EndX=-14 EndY=108.315 EndZ=0
    g76: LineSegment StartX=-14 StartY=108.315 StartZ=0 EndX=-14 EndY=90.43 EndZ=0
    g77: LineSegment StartX=-14 StartY=90.43 StartZ=0 EndX=-4 EndY=90.43 EndZ=0
    g78: LineSegment StartX=-4 StartY=90.43 StartZ=0 EndX=-4 EndY=108.315 EndZ=0
    g79: LineSegment StartX=-4 StartY=146.4 StartZ=0 EndX=-14 EndY=146.4 EndZ=0
    g80: LineSegment StartX=-14 StartY=146.4 StartZ=0 EndX=-14 EndY=128.515 EndZ=0
    g81: LineSegment StartX=-14 StartY=128.515 StartZ=0 EndX=-4 EndY=128.515 EndZ=0
    g82: LineSegment StartX=-4 StartY=128.515 StartZ=0 EndX=-4 EndY=146.4 EndZ=0
    g83: LineSegment StartX=4 StartY=-17.4 StartZ=0 EndX=4 EndY=-36.9675 EndZ=0
    g84: LineSegment StartX=4 StartY=-36.9675 StartZ=0 EndX=14 EndY=-36.9675 EndZ=0
    g85: LineSegment StartX=14 StartY=-36.9675 StartZ=0 EndX=14 EndY=-17.4 EndZ=0
    g86: LineSegment StartX=14 StartY=-17.4 StartZ=0 EndX=4 EndY=-17.4 EndZ=0
    g87: LineSegment StartX=4 StartY=-53.2875 StartZ=0 EndX=4 EndY=-74.635 EndZ=0
    g88: LineSegment StartX=4 StartY=-74.635 StartZ=0 EndX=14 EndY=-74.635 EndZ=0
    g89: LineSegment StartX=14 StartY=-74.635 StartZ=0 EndX=14 EndY=-53.2875 EndZ=0
    g90: LineSegment StartX=14 StartY=-53.2875 StartZ=0 EndX=4 EndY=-53.2875 EndZ=0
    g91: LineSegment StartX=4 StartY=-94.835 StartZ=0 EndX=4 EndY=-112.303 EndZ=0
    g92: LineSegment StartX=4 StartY=-112.303 StartZ=0 EndX=14 EndY=-112.303 EndZ=0
    g93: LineSegment StartX=14 StartY=-112.303 StartZ=0 EndX=14 EndY=-94.835 EndZ=0
    g94: LineSegment StartX=14 StartY=-94.835 StartZ=0 EndX=4 EndY=-94.835 EndZ=0
    g95: LineSegment StartX=4 StartY=-132.503 StartZ=0 EndX=4 EndY=-149.97 EndZ=0
    g96: LineSegment StartX=4 StartY=-149.97 StartZ=0 EndX=14 EndY=-149.97 EndZ=0
    g97: LineSegment StartX=14 StartY=-149.97 StartZ=0 EndX=14 EndY=-132.503 EndZ=0
    g98: LineSegment StartX=14 StartY=-132.503 StartZ=0 EndX=4 EndY=-132.503 EndZ=0
    g99: LineSegment StartX=-4 StartY=-132.503 StartZ=0 EndX=-14 EndY=-132.503 EndZ=0
    g100: LineSegment StartX=-14 StartY=-132.503 StartZ=0 EndX=-14 EndY=-149.97 EndZ=0
    g101: LineSegment StartX=-14 StartY=-149.97 StartZ=0 EndX=-4 EndY=-149.97 EndZ=0
    g102: LineSegment StartX=-4 StartY=-149.97 StartZ=0 EndX=-4 EndY=-132.503 EndZ=0
    g103: LineSegment StartX=-4 StartY=-94.835 StartZ=0 EndX=-14 EndY=-94.835 EndZ=0
    g104: LineSegment StartX=-14 StartY=-94.835 StartZ=0 EndX=-14 EndY=-112.303 EndZ=0
    g105: LineSegment StartX=-14 StartY=-112.303 StartZ=0 EndX=-4 EndY=-112.303 EndZ=0
    g106: LineSegment StartX=-4 StartY=-112.303 StartZ=0 EndX=-4 EndY=-94.835 EndZ=0
    g107: LineSegment StartX=-4 StartY=-53.2875 StartZ=0 EndX=-14 EndY=-53.2875 EndZ=0
    g108: LineSegment StartX=-14 StartY=-53.2875 StartZ=0 EndX=-14 EndY=-74.635 EndZ=0
    g109: LineSegment StartX=-14 StartY=-74.635 StartZ=0 EndX=-4 EndY=-74.635 EndZ=0
    g110: LineSegment StartX=-4 StartY=-74.635 StartZ=0 EndX=-4 EndY=-53.2875 EndZ=0
    g111: LineSegment StartX=-4 StartY=-17.4 StartZ=0 EndX=-14 EndY=-17.4 EndZ=0
    g112: LineSegment StartX=-14 StartY=-17.4 StartZ=0 EndX=-14 EndY=-36.9675 EndZ=0
    g113: LineSegment StartX=-14 StartY=-36.9675 StartZ=0 EndX=-4 EndY=-36.9675 EndZ=0
    g114: LineSegment StartX=-4 StartY=-36.9675 StartZ=0 EndX=-4 EndY=-17.4 EndZ=0
    g115: ArcOfCircle CenterX=109.1 CenterY=-5.32 CenterZ=0 NormalX=0 NormalY=0 NormalZ=1 AngleXU=0 Radius=5 StartAngle=5.85414 EndAngle=7.21048
  constraints (345):
    c: Coincident(g0,g1)
    c: Coincident(g1,g2)
    c: Coincident(g2,g3)
    c: Coincident(g3,g0)
    c: Vertical(g0)
    c: Vertical(g2)
    c: Horizontal(g1)
    c: Horizontal(g3)
    c: PointOnObject(g0,g-8)
    c: PointOnObject(g1,g-9)
    c: DistanceX(g1,g-5) = 8
    c: DistanceX(g-6,g0) = 8
    c: Coincident(g4,g5)
    c: Coincident(g5,g6)
    c: Coincident(g6,g7)
    c: Coincident(g7,g4)
    c: Vertical(g4)
    c: Vertical(g6)
    c: Horizontal(g5)
    c: Horizontal(g7)
    c: PointOnObject(g4,g-8)
    c: PointOnObject(g5,g-9)
    c: Coincident(g8,g9)
    c: Coincident(g9,g10)
    c: Coincident(g10,g11)
    c: Coincident(g11,g8)
    c: Vertical(g8)
    c: Vertical(g10)
    c: Horizontal(g9)
    c: Horizontal(g11)
    c: PointOnObject(g8,g-8)
    c: PointOnObject(g9,g-9)
    c: Coincident(g12,g13)
    c: Coincident(g13,g14)
    c: Coincident(g14,g15)
    c: Coincident(g15,g12)
    c: Vertical(g12)
    c: Vertical(g14)
    c: Horizontal(g13)
    c: Horizontal(g15)
    c: PointOnObject(g12,g-8)
    c: PointOnObject(g13,g-9)
    c: DistanceX(g13,g-6) = 8
    c: DistanceX(g-7,g12) = 16
    c: DistanceX(g-5,g4) = 8
    c: DistanceX(g5,g-3) = 8
    c: DistanceX(g-3,g8) = 8
    c: DistanceX(g9,g-4) = 16
    c: Coincident(g16,g17)
    c: Coincident(g17,g18)
    c: Coincident(g18,g19)
    c: Coincident(g19,g16)
    c: Horizontal(g16)
    c: Horizontal(g18)
    c: Vertical(g17)
    c: Vertical(g19)
    c: PointOnObject(g16,g-10)
    c: Coincident(g20,g21)
    c: Coincident(g22,g23)
    c: Coincident(g23,g20)
    c: Horizontal(g20)
    c: Horizontal(g22)
    c: Vertical(g21)
    c: Vertical(g23)
    c: PointOnObject(g20,g-10)
    c: Coincident(g24,g25)
    c: Coincident(g25,g26)
    c: Coincident(g26,g27)
    c: Coincident(g27,g24)
    c: Horizontal(g24)
    c: Horizontal(g26)
    c: Vertical(g25)
    c: Vertical(g27)
    c: PointOnObject(g24,g-10)
    c: Coincident(g28,g29)
    c: Coincident(g29,g30)
    c: Coincident(g30,g31)
    c: Coincident(g31,g28)
    c: Horizontal(g28)
    c: Horizontal(g30)
    c: Vertical(g29)
    c: Vertical(g31)
    c: PointOnObject(g28,g-10)
    c: Equal(g30,g13)
    c: Vertical(g12,g29)
    c: Vertical(g0,g25)
    c: Equal(g1,g26)
    c: Equal(g9,g18)
    c: Vertical(g8,g17)
    c: Coincident(g32,g33)
    c: Coincident(g33,g34)
    c: Coincident(g34,g35)
    c: Coincident(g35,g32)
    c: Vertical(g32)
    c: Vertical(g34)
    c: Horizontal(g33)
    c: Horizontal(g35)
    c: PointOnObject(g32,g-16)
    c: Coincident(g36,g37)
    c: Coincident(g38,g39)
    c: Coincident(g39,g36)
    c: Vertical(g36)
    c: Vertical(g38)
    c: Horizontal(g37)
    c: Horizontal(g39)
    c: PointOnObject(g36,g-16)
    c: Coincident(g40,g41)
    c: Coincident(g42,g43)
    c: Coincident(g43,g40)
    c: Horizontal(g40)
    c: Horizontal(g42)
    c: Vertical(g41)
    c: Vertical(g43)
    c: PointOnObject(g40,g-16)
    c: DistanceX(g40,g-14) = 8
    c: DistanceX(g-13,g40) = 8
    c: PointOnObject(g42,g-20)
    c: Coincident(g44,g45)
    c: Coincident(g45,g46)
    c: Coincident(g47,g44)
    c: Horizontal(g44)
    c: Horizontal(g46)
    c: Vertical(g45)
    c: Vertical(g47)
    c: PointOnObject(g44,g-16)
    c: DistanceX(g44,g-15) = 16
    c: DistanceX(g-14,g44) = 8
    c: DistanceX(g38,g-13) = 8
    c: DistanceX(g-12,g36) = 8
    c: DistanceX(g34,g-12) = 8
    c: DistanceX(g-11,g32) = 16
    c: PointOnObject(g32,g-17)
    c: PointOnObject(g36,g-17)
    c: PointOnObject(g38,g-21)
    c: Coincident(g48,g-21)
    c: Coincident(g48,g37)
    c: Coincident(g48,g38)
    c: PointOnObject(g41,g-23)
    c: Coincident(g49,g-23)
    c: Coincident(g49,g42)
    c: Coincident(g49,g41)
    c: PointOnObject(g45,g-20)
    c: PointOnObject(g47,g-24)
    c: Coincident(g50,g-24)
    c: Coincident(g50,g46)
    c: Coincident(g47,g50)
    c: Coincident(g51,g52)
    c: Coincident(g52,g53)
    c: Coincident(g53,g54)
    c: Coincident(g54,g51)
    c: Horizontal(g51)
    c: Horizontal(g53)
    c: Vertical(g52)
    c: Vertical(g54)
    c: Coincident(g55,g56)
    c: Coincident(g56,g57)
    c: Coincident(g57,g58)
    c: Coincident(g58,g55)
    c: Horizontal(g55)
    c: Horizontal(g57)
    c: Vertical(g56)
    c: Vertical(g58)
    c: Coincident(g59,g60)
    c: Coincident(g60,g61)
    c: Coincident(g61,g62)
    c: Coincident(g62,g59)
    c: Horizontal(g59)
    c: Horizontal(g61)
    c: Vertical(g60)
    c: Vertical(g62)
    c: Coincident(g63,g64)
    c: Coincident(g64,g65)
    c: Coincident(g65,g66)
    c: Coincident(g66,g63)
    c: Horizontal(g63)
    c: Horizontal(g65)
    c: Vertical(g64)
    c: Vertical(g66)
    c: Equal(g33,g65)
    c: Vertical(g64,g32)
    c: PointOnObject(g64,g-19)
    c: Vertical(g60,g36)
    c: Equal(g61,g39)
    c: PointOnObject(g59,g-18)
    c: PointOnObject(g60,g-19)
    c: PointOnObject(g63,g-18)
    c: PointOnObject(g55,g-18)
    c: PointOnObject(g56,g-19)
    c: PointOnObject(g52,g-19)
    c: PointOnObject(g51,g-18)
    c: Vertical(g45,g52)
    c: Equal(g44,g51)
    c: Equal(g55,g40)
    c: Vertical(g40,g55)
    c: Coincident(g67,g68)
    c: Coincident(g68,g69)
    c: Coincident(g69,g70)
    c: Coincident(g70,g67)
    c: Vertical(g67)
    c: Vertical(g69)
    c: Horizontal(g68)
    c: Horizontal(g70)
    c: PointOnObject(g67,g-43)
    c: PointOnObject(g68,g-40)
    c: Coincident(g71,g72)
    c: Coincident(g72,g73)
    c: Coincident(g73,g74)
    c: Coincident(g74,g71)
    c: Vertical(g71)
    c: Vertical(g73)
    c: Horizontal(g72)
    c: Horizontal(g74)
    c: PointOnObject(g72,g-40)
    c: Coincident(g75,g76)
    c: Coincident(g76,g77)
    c: Coincident(g77,g78)
    c: Coincident(g78,g75)
    c: Horizontal(g75)
    c: Horizontal(g77)
    c: Vertical(g76)
    c: Vertical(g78)
    c: PointOnObject(g75,g-41)
    c: Coincident(g79,g80)
    c: Coincident(g80,g81)
    c: Coincident(g81,g82)
    c: Coincident(g82,g79)
    c: Horizontal(g79)
    c: Horizontal(g81)
    c: Vertical(g80)
    c: Vertical(g82)
    c: PointOnObject(g79,g-41)
    c: DistanceY(g-32,g67) = 8
    c: DistanceY(g71,g-32) = 8
    c: Coincident(g-43,g71)
    c: Coincident(g76,g-42)
    c: Coincident(g-42,g79)
    c: Horizontal(g67,g81)
    c: Horizontal(g75,g71)
    c: Coincident(g83,g84)
    c: Coincident(g84,g85)
    c: Coincident(g85,g86)
    c: Coincident(g86,g83)
    c: Vertical(g83)
    c: Vertical(g85)
    c: Horizontal(g84)
    c: Horizontal(g86)
    c: Coincident(g87,g88)
    c: Coincident(g88,g89)
    c: Coincident(g89,g90)
    c: Coincident(g90,g87)
    c: Vertical(g87)
    c: Vertical(g89)
    c: Horizontal(g88)
    c: Horizontal(g90)
    c: Coincident(g91,g92)
    c: Coincident(g92,g93)
    c: Coincident(g93,g94)
    c: Coincident(g94,g91)
    c: Vertical(g91)
    c: Vertical(g93)
    c: Horizontal(g92)
    c: Horizontal(g94)
    c: Coincident(g95,g96)
    c: Coincident(g96,g97)
    c: Coincident(g97,g98)
    c: Coincident(g98,g95)
    c: Vertical(g95)
    c: Vertical(g97)
    c: Horizontal(g96)
    c: Horizontal(g98)
    c: Coincident(g99,g100)
    c: Coincident(g100,g101)
    c: Coincident(g101,g102)
    c: Coincident(g102,g99)
    c: Horizontal(g99)
    c: Horizontal(g101)
    c: Vertical(g100)
    c: Vertical(g102)
    c: Coincident(g103,g104)
    c: Coincident(g104,g105)
    c: Coincident(g105,g106)
    c: Coincident(g106,g103)
    c: Horizontal(g103)
    c: Horizontal(g105)
    c: Vertical(g104)
    c: Vertical(g106)
    c: Coincident(g107,g108)
    c: Coincident(g108,g109)
    c: Coincident(g109,g110)
    c: Coincident(g110,g107)
    c: Horizontal(g107)
    c: Horizontal(g109)
    c: Vertical(g108)
    c: Vertical(g110)
    c: Coincident(g111,g112)
    c: Coincident(g112,g113)
    c: Coincident(g113,g114)
    c: Coincident(g114,g111)
    c: Horizontal(g111)
    c: Horizontal(g113)
    c: Vertical(g112)
    c: Vertical(g114)
    c: Equal(g83,g114)
    c: Equal(g87,g110)
    c: Equal(g91,g106)
    c: Equal(g95,g102)
    c: Horizontal(g95,g99)
    c: Horizontal(g91,g103)
    c: Horizontal(g87,g107)
    c: Horizontal(g83,g111)
    c: PointOnObject(g85,g-35)
    c: PointOnObject(g111,g-37)
    c: PointOnObject(g89,g-35)
    c: PointOnObject(g107,g-37)
    c: PointOnObject(g93,g-35)
    c: PointOnObject(g103,g-37)
    c: PointOnObject(g97,g-35)
    c: PointOnObject(g99,g-37)
    c: PointOnObject(g95,g-34)
    c: PointOnObject(g99,g-36)
    c: PointOnObject(g91,g-34)
    c: PointOnObject(g103,g-36)
    c: PointOnObject(g87,g-34)
    c: PointOnObject(g107,g-36)
    c: PointOnObject(g83,g-34)
    c: PointOnObject(g111,g-36)
    c: DistanceY(g-27,g83) = 8
    c: DistanceY(g87,g-27) = 4.12
    c: DistanceY(g-26,g87) = 8
    c: DistanceY(g91,g-26) = 8
    c: DistanceY(g-25,g91) = 8
    c: DistanceY(g95,g-25) = 8
    c: Distance(g-46,g111) = 20
    c: DistanceY(g-33,g95) = 8
    c: Horizontal(g79,g67)
    c: PointOnObject(g29,g-47)
    c: PointOnObject(g25,g-47)
    c: PointOnObject(g17,g-48)
    c: PointOnObject(g22,g-48)
    c: Coincident(g115,g-49)
    c: Coincident(g115,g-48)
    c: Coincident(g21,g115)
    c: PointOnObject(g22,g115)
    c: Vertical(g20,g4)
    c: Vertical(g20,g5)
FEATURE [PartDesign::Pad] Pad020  label="bottom screw gaps filler"
  BaseFeature = -> Hole022
  Direction = (0,0,-1)
  Length = 4.4
  Length2 = 10
  Profile = -> Sketch054
  ReferenceAxis = -> Sketch054 [N_Axis]
  Refine = true
  Suppressed = false
  Type = 0
FEATURE [Sketcher::SketchObject] Sketch055
  ArcFitTolerance = 1e-06
  AttachmentSupport = -> [Pad020]
  ExternalGeometry = -> [Pad020]
  FullyConstrained = true
  MakeInternals = false
  MapMode = 5
  Placement = pos=(0,176.07,0) rot=(0,0.707107,0.707107;3.14159rad)
  expr: Constraints[25] = Spreadsheet.wall_thickness
  expr: Constraints[45] = Spreadsheet.wall_thickness
  expr: Constraints[46] = Spreadsheet.wall_thickness * 2
  expr: Constraints[51] = Spreadsheet.wall_thickness
  expr: Constraints[71] = Spreadsheet.wall_thickness * 2
  expr: Constraints[8] = Spreadsheet.wall_thickness * 2
  sketch-geometry (29):
    g0: LineSegment StartX=39.265 StartY=17.13 StartZ=0 EndX=39.265 EndY=4.63 EndZ=0
    g1: LineSegment StartX=39.265 StartY=4.63 StartZ=0 EndX=47.265 EndY=4.63 EndZ=0
    g2: LineSegment StartX=47.265 StartY=4.63 StartZ=0 EndX=47.265 EndY=17.13 EndZ=0
    g3: LineSegment StartX=47.265 StartY=17.13 StartZ=0 EndX=39.265 EndY=17.13 EndZ=0
    g4: GeomPoint [constr] X=43.265 Y=4.63 Z=0
    g5: LineSegment [constr] StartX=43.265 StartY=4.63 StartZ=0 EndX=37.13 EndY=2.2 EndZ=0
    g6: LineSegment [constr] StartX=43.265 StartY=4.63 StartZ=0 EndX=49.4 EndY=2.2 EndZ=0
    g7: LineSegment StartX=-120.9 StartY=19.63 StartZ=0 EndX=-120.9 EndY=4.63 EndZ=0
    g8: LineSegment StartX=-120.9 StartY=4.63 StartZ=0 EndX=-116.9 EndY=4.63 EndZ=0
    g9: LineSegment StartX=-116.9 StartY=4.63 StartZ=0 EndX=-116.9 EndY=19.63 EndZ=0
    g10: LineSegment StartX=-116.9 StartY=19.63 StartZ=0 EndX=-120.9 EndY=19.63 EndZ=0
    g11: LineSegment StartX=-120.9 StartY=176.5 StartZ=0 EndX=-120.9 EndY=69.34 EndZ=0
    g12: LineSegment StartX=-120.9 StartY=69.34 StartZ=0 EndX=-117.88 EndY=69.34 EndZ=0
    g13: LineSegment StartX=-117.88 StartY=69.34 StartZ=0 EndX=-117.88 EndY=176.5 EndZ=0
    g14: LineSegment StartX=-117.88 StartY=176.5 StartZ=0 EndX=-120.9 EndY=176.5 EndZ=0
    g15: LineSegment StartX=34.1 StartY=176.5 StartZ=0 EndX=30.1 EndY=176.5 EndZ=0
    g16: LineSegment StartX=30.1 StartY=176.5 StartZ=0 EndX=30.1 EndY=130 EndZ=0
    g17: LineSegment StartX=34.1 StartY=130 StartZ=0 EndX=34.1 EndY=176.5 EndZ=0
    g18: LineSegment StartX=34.1 StartY=130 StartZ=0 EndX=34.1 EndY=71.84 EndZ=0
    g19: LineSegment StartX=34.1 StartY=71.84 StartZ=0 EndX=42.1 EndY=71.84 EndZ=0
    g20: LineSegment StartX=42.1 StartY=71.84 StartZ=0 EndX=42.1 EndY=130 EndZ=0
    g21: LineSegment StartX=207 StartY=126 StartZ=0 EndX=195 EndY=126 EndZ=0
    g22: LineSegment StartX=195 StartY=126 StartZ=0 EndX=195 EndY=130 EndZ=0
    g23: LineSegment StartX=195 StartY=130 StartZ=0 EndX=215 EndY=130 EndZ=0
    g24: LineSegment StartX=34.1 StartY=130 StartZ=0 EndX=42.1 EndY=130 EndZ=0
    g25: LineSegment StartX=34.1 StartY=130 StartZ=0 EndX=30.1 EndY=130 EndZ=0
    g26: LineSegment StartX=215 StartY=130 StartZ=0 EndX=215 EndY=0 EndZ=0
    g27: LineSegment StartX=215 StartY=0 StartZ=0 EndX=207 EndY=0 EndZ=0
    g28: LineSegment StartX=207 StartY=0 StartZ=0 EndX=207 EndY=126 EndZ=0
  constraints (77):
    c: Coincident(g0,g1)
    c: Coincident(g1,g2)
    c: Coincident(g2,g3)
    c: Coincident(g3,g0)
    c: Vertical(g0)
    c: Vertical(g2)
    c: Horizontal(g1)
    c: Horizontal(g3)
    c: DistanceX(g0,g2) = 8
    c: DistanceY(g1,g2) = 12.5
    c: DistanceY(g0,g-6) = 5
    c: Symmetric(g1,g1,g4)
    c: Coincident(g5,g4)
    c: Coincident(g5,g-5)
    c: Coincident(g6,g4)
    c: Coincident(g6,g-4)
    c: Equal(g5,g6)
    c: Coincident(g7,g8)
    c: Coincident(g8,g9)
    c: Coincident(g9,g10)
    c: Coincident(g10,g7)
    c: Vertical(g7)
    c: Vertical(g9)
    c: Horizontal(g8)
    c: Horizontal(g10)
    c: DistanceX(g8,g8) = 4
    c: DistanceY(g9,g-6) = 2.5
    c: DistanceY(g9,g9) = 15
    c: Coincident(g11,g12)
    c: Coincident(g12,g13)
    c: Vertical(g11)
    c: Vertical(g13)
    c: Horizontal(g12)
    c: Horizontal(g14)
    c: Distance(g12,g-7) = 2.5
    c: PointOnObject(g-8,g13)
    c: Coincident(g15,g16)
    c: Coincident(g17,g15)
    c: Horizontal(g15)
    c: Vertical(g16)
    c: Coincident(g18,g19)
    c: Coincident(g19,g20)
    c: Vertical(g18)
    c: Vertical(g20)
    c: Horizontal(g19)
    c: Distance(g16,g17) = 4
    c: DistanceX(g18,g20) = 8
    c: DistanceY(g-7,g19) = 5
    c: Horizontal(g21)
    c: Coincident(g21,g22)
    c: Vertical(g22)
    c: Distance(g22,g22) = 4
    c: PointOnObject(g22,g-9)
    c: Coincident(g23,g22)
    c: Coincident(g18,g-12)
    c: Coincident(g17,g18)
    c: Coincident(g24,g17)
    c: PointOnObject(g24,g-12)
    c: Coincident(g20,g24)
    c: Coincident(g25,g17)
    c: Horizontal(g25)
    c: Coincident(g25,g16)
    c: Coincident(g15,g-13)
    c: PointOnObject(g7,g-14)
    c: Coincident(g11,g-14)
    c: Coincident(g14,g11)
    c: Coincident(g14,g13)
    c: Coincident(g26,g-10)
    c: Coincident(g26,g27)
    c: PointOnObject(g27,g-3)
    c: DistanceX(g22,g23) = 20
    c: DistanceX(g27,g27) = 8
    c: Coincident(g28,g27)
    c: Vertical(g28)
    c: Coincident(g21,g28)
    c: Coincident(g23,g26)
    c: Coincident(g23,g-10)
FEATURE [PartDesign::Pad] Pad021  label="rear support"
  BaseFeature = -> Pad020
  Direction = (0,1,-2e-16)
  Length = 11.43
  Length2 = 10
  Profile = -> Sketch055
  ReferenceAxis = -> Sketch055 [N_Axis]
  Refine = true
  Suppressed = false
  Type = 0
  expr: Length = Spreadsheet.pcie_tab_depth
FEATURE [Sketcher::SketchObject] Sketch056
  ArcFitTolerance = 1e-06
  AttachmentSupport = -> [Pad021]
  ExternalGeometry = -> [Pad021]
  FullyConstrained = true
  MakeInternals = false
  MapMode = 5
  Placement = pos=(0,0,133.83) rot=(0,0,1;0rad)
  sketch-geometry (2):
    g0: Circle CenterX=-201 CenterY=179.785 CenterZ=0 NormalX=0 NormalY=0 NormalZ=1 AngleXU=0 Radius=1.5
    g1: GeomPoint [constr] X=-207 Y=183.5 Z=0
  constraints (4):
    c: Diameter(g0) = 3
    c: PointOnObject(g1,g-6)
    c: PointOnObject(g1,g-7)
    c: Symmetric(g-5,g1,g0)
FEATURE [Sketcher::SketchObject] Sketch063
  ArcFitTolerance = 1e-06
  AttachmentSupport = -> [Pad021]
  ExternalGeometry = -> [Pad021]
  FullyConstrained = true
  MakeInternals = false
  MapMode = 5
  Placement = pos=(0,183.5,0) rot=(1,0,0;1.5708rad)
  expr: Constraints[9] = Spreadsheet.wall_thickness
  sketch-geometry (4):
    g0: LineSegment StartX=-207 StartY=148.83 StartZ=0 EndX=-211 EndY=148.83 EndZ=0
    g1: LineSegment StartX=-211 StartY=148.83 StartZ=0 EndX=-211 EndY=133.83 EndZ=0
    g2: LineSegment StartX=-211 StartY=133.83 StartZ=0 EndX=-207 EndY=133.83 EndZ=0
    g3: LineSegment StartX=-207 StartY=133.83 StartZ=0 EndX=-207 EndY=148.83 EndZ=0
  constraints (11):
    c: Coincident(g0,g1)
    c: Coincident(g1,g2)
    c: Coincident(g2,g3)
    c: Coincident(g3,g0)
    c: Horizontal(g0)
    c: Horizontal(g2)
    c: Vertical(g1)
    c: Vertical(g3)
    c: Coincident(g1,g-4)
    c: DistanceX(g0,g0) = 4
    c: DistanceY(g3,g3) = 15
FEATURE [PartDesign::Pad] Pad022  label="rear support 2"
  BaseFeature = -> Pad021
  Direction = (0,-1,2e-16)
  Length = 11.43
  Length2 = 10
  Profile = -> Sketch063
  ReferenceAxis = -> Sketch063 [N_Axis]
  Refine = true
  Suppressed = false
  Type = 0
  expr: Length = Spreadsheet.pcie_tab_depth
FEATURE [PartDesign::Hole] Hole023
  BaseFeature = -> Pad022
  CustomThreadClearance = 0
  Depth = 8
  DepthType = 0
  Diameter = 3.4
  DrillForDepth = false
  DrillPoint = 0
  DrillPointAngle = 118
  HoleCutCountersinkAngle = 90
  HoleCutCustomValues = false
  HoleCutDepth = 0
  HoleCutDiameter = 6.1
  HoleCutType = 2
  ModelThread = false
  Profile = -> Sketch056
  Refine = true
  Suppressed = false
  Tapered = false
  TaperedAngle = 90
  ThreadClass = 0
  ThreadDepth = 8
  ThreadDepthType = 0
  ThreadDirection = 0
  ThreadFit = 0
  ThreadSize = 9
  ThreadType = 1
  Threaded = false
  UseCustomThreadClearance = false
  expr: Depth = Spreadsheet.wall_thickness * 2
FEATURE [Sketcher::SketchObject] Sketch057
  ArcFitTolerance = 1e-06
  AttachmentSupport = -> [Hole023]
  ExternalGeometry = -> [Hole023]
  FullyConstrained = true
  MakeInternals = false
  MapMode = 5
  Placement = pos=(-215,0,0) rot=(0.57735,-0.57735,-0.57735;2.0944rad)
  sketch-geometry (11):
    g0: Circle CenterX=-177.785 CenterY=141.33 CenterZ=0 NormalX=0 NormalY=0 NormalZ=1 AngleXU=0 Radius=1.5
    g1: Circle CenterX=-179.785 CenterY=94.5 CenterZ=0 NormalX=0 NormalY=0 NormalZ=1 AngleXU=0 Radius=1.5
    g2: Circle CenterX=-179.785 CenterY=63 CenterZ=0 NormalX=0 NormalY=0 NormalZ=1 AngleXU=0 Radius=1.5
    g3: Circle CenterX=-179.785 CenterY=31.5 CenterZ=0 NormalX=0 NormalY=0 NormalZ=1 AngleXU=0 Radius=1.5
    g4: GeomPoint [constr] X=-179.785 Y=126 Z=0
    g5: LineSegment [constr] StartX=-179.785 StartY=126 StartZ=0 EndX=-179.785 EndY=94.5 EndZ=0
    g6: LineSegment [constr] StartX=-179.785 StartY=94.5 StartZ=0 EndX=-179.785 EndY=63 EndZ=0
    g7: LineSegment [constr] StartX=-179.785 StartY=63 StartZ=0 EndX=-179.785 EndY=31.5 EndZ=0
    g8: LineSegment [constr] StartX=-179.785 StartY=31.5 StartZ=0 EndX=-179.785 EndY=0 EndZ=0
    g9: GeomPoint [constr] X=-176.07 Y=133.83 Z=0
    g10: GeomPoint [constr] X=-179.785 Y=133.83 Z=0
  constraints (25):
    c: Diameter(g0) = 3
    c: Diameter(g1) = 3
    c: Diameter(g2) = 3
    c: Diameter(g3) = 3
    c: Vertical(g1,g2)
    c: Vertical(g2,g3)
    c: Coincident(g5,g4)
    c: Coincident(g5,g1)
    c: Coincident(g6,g1)
    c: Coincident(g6,g2)
    c: Coincident(g7,g2)
    c: Coincident(g7,g3)
    c: Coincident(g8,g3)
    c: Vertical(g8)
    c: Equal(g8,g7)
    c: Equal(g7,g6)
    c: Equal(g6,g5)
    c: PointOnObject(g8,g-1)
    c: Symmetric(g-4,g-3,g0)
    c: PointOnObject(g9,g-3)
    c: Vertical(g-5,g9)
    c: Symmetric(g9,g-3,g10)
    c: Vertical(g4,g10)
    c: PointOnObject(g4,g-6)
    c: Vertical(g5)
FEATURE [PartDesign::Hole] Hole024
  BaseFeature = -> Hole023
  CustomThreadClearance = 0
  Depth = 8
  DepthType = 0
  Diameter = 3.4
  DrillForDepth = false
  DrillPoint = 0
  DrillPointAngle = 118
  HoleCutCountersinkAngle = 90
  HoleCutCustomValues = false
  HoleCutDepth = 0
  HoleCutDiameter = 6.1
  HoleCutType = 2
  ModelThread = false
  Profile = -> Sketch057
  Refine = true
  Suppressed = false
  Tapered = false
  TaperedAngle = 90
  ThreadClass = 0
  ThreadDepth = 8
  ThreadDepthType = 0
  ThreadDirection = 0
  ThreadFit = 0
  ThreadSize = 9
  ThreadType = 1
  Threaded = false
  UseCustomThreadClearance = false
  expr: Depth = Spreadsheet.wall_thickness * 2
FEATURE [Sketcher::SketchObject] Sketch058
  ArcFitTolerance = 1e-06
  AttachmentSupport = -> [Hole024]
  ExternalGeometry = -> [Hole024]
  FullyConstrained = true
  MakeInternals = false
  MapMode = 5
  Placement = pos=(-38.1,0,0) rot=(0.57735,-0.57735,-0.57735;2.0944rad)
  sketch-geometry (5):
    g0: Circle CenterX=-179.785 CenterY=162.277 CenterZ=0 NormalX=0 NormalY=0 NormalZ=1 AngleXU=0 Radius=1.5
    g1: Circle CenterX=-179.785 CenterY=148.053 CenterZ=0 NormalX=0 NormalY=0 NormalZ=1 AngleXU=0 Radius=1.5
    g2: LineSegment [constr] StartX=-179.785 StartY=176.5 StartZ=0 EndX=-179.785 EndY=162.277 EndZ=0
    g3: LineSegment [constr] StartX=-179.785 StartY=162.277 StartZ=0 EndX=-179.785 EndY=148.053 EndZ=0
    g4: LineSegment [constr] StartX=-179.785 StartY=148.053 StartZ=0 EndX=-179.785 EndY=133.83 EndZ=0
  constraints (13):
    c: Diameter(g0) = 3
    c: Diameter(g1) = 3
    c: Coincident(g2,g0)
    c: Vertical(g2)
    c: Coincident(g2,g3)
    c: Coincident(g3,g1)
    c: Vertical(g3)
    c: Coincident(g3,g4)
    c: PointOnObject(g4,g-5)
    c: Vertical(g4,g1)
    c: Equal(g4,g3)
    c: Equal(g3,g2)
    c: Symmetric(g-6,g-4,g2)
FEATURE [PartDesign::Hole] Hole025
  BaseFeature = -> Hole024
  CustomThreadClearance = 0
  Depth = 8
  DepthType = 0
  Diameter = 3.4
  DrillForDepth = false
  DrillPoint = 0
  DrillPointAngle = 118
  HoleCutCountersinkAngle = 90
  HoleCutCustomValues = false
  HoleCutDepth = 0
  HoleCutDiameter = 6.1
  HoleCutType = 2
  ModelThread = false
  Profile = -> Sketch058
  Refine = true
  Suppressed = false
  Tapered = false
  TaperedAngle = 90
  ThreadClass = 0
  ThreadDepth = 8
  ThreadDepthType = 0
  ThreadDirection = 0
  ThreadFit = 0
  ThreadSize = 9
  ThreadType = 1
  Threaded = false
  UseCustomThreadClearance = false
  expr: Depth = Spreadsheet.wall_thickness * 2
FEATURE [Sketcher::SketchObject] Sketch059
  ArcFitTolerance = 1e-06
  AttachmentSupport = -> [Hole025]
  ExternalGeometry = -> [Hole025]
  FullyConstrained = true
  MakeInternals = false
  MapMode = 5
  Placement = pos=(-42.1,0,0) rot=(0.57735,-0.57735,-0.57735;2.0944rad)
  sketch-geometry (9):
    g0: GeomPoint [constr] X=-181.785 Y=130 Z=0
    g1: GeomPoint [constr] X=-181.785 Y=71.84 Z=0
    g2: LineSegment [constr] StartX=-181.785 StartY=71.84 StartZ=0 EndX=-181.785 EndY=77.84 EndZ=0
    g3: LineSegment [constr] StartX=-181.785 StartY=77.84 StartZ=0 EndX=-181.785 EndY=100.92 EndZ=0
    g4: LineSegment [constr] StartX=-181.785 StartY=100.92 StartZ=0 EndX=-181.785 EndY=124 EndZ=0
    g5: LineSegment [constr] StartX=-181.785 StartY=124 StartZ=0 EndX=-181.785 EndY=130 EndZ=0
    g6: Circle CenterX=-181.785 CenterY=100.92 CenterZ=0 NormalX=0 NormalY=0 NormalZ=1 AngleXU=0 Radius=1.5
    g7: Circle CenterX=-181.785 CenterY=124 CenterZ=0 NormalX=0 NormalY=0 NormalZ=1 AngleXU=0 Radius=1.5
    g8: Circle CenterX=-181.785 CenterY=77.84 CenterZ=0 NormalX=0 NormalY=0 NormalZ=1 AngleXU=0 Radius=1.5
  constraints (19):
    c: Symmetric(g-4,g-4,g0)
    c: Symmetric(g-3,g-3,g1)
    c: Coincident(g2,g1)
    c: Vertical(g2)
    c: Coincident(g2,g3)
    c: Vertical(g3)
    c: Coincident(g3,g4)
    c: Vertical(g4)
    c: Coincident(g4,g5)
    c: Coincident(g5,g0)
    c: Equal(g5,g2)
    c: Equal(g4,g3)
    c: DistanceY(g2,g2) = 6
    c: Diameter(g6) = 3
    c: Coincident(g6,g3)
    c: Diameter(g7) = 3
    c: Coincident(g7,g4)
    c: Diameter(g8) = 3
    c: Coincident(g8,g2)
FEATURE [PartDesign::Hole] Hole026
  BaseFeature = -> Hole025
  CustomThreadClearance = 0
  Depth = 8
  DepthType = 0
  Diameter = 3.4
  DrillForDepth = false
  DrillPoint = 0
  DrillPointAngle = 118
  HoleCutCountersinkAngle = 90
  HoleCutCustomValues = false
  HoleCutDepth = 0
  HoleCutDiameter = 6.1
  HoleCutType = 2
  ModelThread = false
  Profile = -> Sketch059
  Refine = true
  Suppressed = false
  Tapered = false
  TaperedAngle = 90
  ThreadClass = 0
  ThreadDepth = 8
  ThreadDepthType = 0
  ThreadDirection = 0
  ThreadFit = 0
  ThreadSize = 9
  ThreadType = 1
  Threaded = false
  UseCustomThreadClearance = false
  expr: Depth = Spreadsheet.wall_thickness * 2
FEATURE [Sketcher::SketchObject] Sketch060
  ArcFitTolerance = 1e-06
  AttachmentSupport = -> [Hole026]
  ExternalGeometry = -> [Hole026]
  FullyConstrained = true
  MakeInternals = false
  MapMode = 5
  Placement = pos=(-47.265,0,0) rot=(0.57735,-0.57735,-0.57735;2.0944rad)
  sketch-geometry (1):
    g0: Circle CenterX=-181.785 CenterY=10.88 CenterZ=0 NormalX=0 NormalY=0 NormalZ=1 AngleXU=0 Radius=1.5
  constraints (2):
    c: Diameter(g0) = 3
    c: Symmetric(g-3,g-4,g0)
FEATURE [PartDesign::Hole] Hole027
  BaseFeature = -> Hole026
  CustomThreadClearance = 0
  Depth = 8
  DepthType = 0
  Diameter = 3.4
  DrillForDepth = false
  DrillPoint = 0
  DrillPointAngle = 118
  HoleCutCountersinkAngle = 90
  HoleCutCustomValues = false
  HoleCutDepth = 0
  HoleCutDiameter = 6.1
  HoleCutType = 2
  ModelThread = false
  Profile = -> Sketch060
  Refine = true
  Suppressed = false
  Tapered = false
  TaperedAngle = 90
  ThreadClass = 0
  ThreadDepth = 8
  ThreadDepthType = 0
  ThreadDirection = 0
  ThreadFit = 0
  ThreadSize = 9
  ThreadType = 1
  Threaded = false
  UseCustomThreadClearance = false
  expr: Depth = Spreadsheet.wall_thickness * 2
FEATURE [Sketcher::SketchObject] Sketch061
  ArcFitTolerance = 1e-06
  AttachmentSupport = -> [Hole027]
  ExternalGeometry = -> [Hole027]
  FullyConstrained = false
  MakeInternals = false
  MapMode = 5
  Placement = pos=(124.9,-1.051e-13,0) rot=(0.57735,0.57735,0.57735;2.0944rad)
  sketch-geometry (4):
    g0: Circle CenterX=179.785 CenterY=13.815 CenterZ=0 NormalX=0 NormalY=0 NormalZ=1 AngleXU=0 Radius=1.5
    g1: Circle CenterX=179.785 CenterY=79.34 CenterZ=0 NormalX=0 NormalY=0 NormalZ=1 AngleXU=0 Radius=1.5
    g2: Circle CenterX=179.785 CenterY=165 CenterZ=0 NormalX=0 NormalY=0 NormalZ=1 AngleXU=0 Radius=1.5
    g3: Circle CenterX=179.785 CenterY=122.17 CenterZ=0 NormalX=0 NormalY=0 NormalZ=1 AngleXU=0 Radius=1.5
  constraints (9):
    c: Diameter(g0) = 3
    c: Symmetric(g-7,g-4,g0)
    c: Diameter(g1) = 3
    c: Diameter(g2) = 3
    c: Diameter(g3) = 3
    c: Vertical(g0,g1)
    c: Vertical(g1,g3)
    c: Distance(g1,g-8) = 10
    c: Symmetric(g2,g1,g3)
FEATURE [PartDesign::Hole] Hole028
  BaseFeature = -> Hole027
  CustomThreadClearance = 0
  Depth = 8
  DepthType = 0
  Diameter = 3.4
  DrillForDepth = false
  DrillPoint = 0
  DrillPointAngle = 118
  HoleCutCountersinkAngle = 90
  HoleCutCustomValues = false
  HoleCutDepth = 0
  HoleCutDiameter = 6.1
  HoleCutType = 2
  ModelThread = false
  Profile = -> Sketch061
  Refine = true
  Suppressed = false
  Tapered = false
  TaperedAngle = 90
  ThreadClass = 0
  ThreadDepth = 8
  ThreadDepthType = 0
  ThreadDirection = 0
  ThreadFit = 0
  ThreadSize = 9
  ThreadType = 1
  Threaded = false
  UseCustomThreadClearance = false
  expr: Depth = Spreadsheet.wall_thickness * 2
FEATURE [Sketcher::SketchObject] Sketch062
  ArcFitTolerance = 1e-06
  AttachmentSupport = -> [Hole028]
  FullyConstrained = true
  MakeInternals = false
  MapMode = 5
  Placement = pos=(-215,0,0) rot=(0.57735,-0.57735,-0.57735;2.0944rad)
  sketch-geometry (12):
    g0: LineSegment [constr] StartX=176.5 StartY=170 StartZ=0 EndX=103.5 EndY=170 EndZ=0
    g1: LineSegment [constr] StartX=103.5 StartY=170 StartZ=0 EndX=103.5 EndY=55 EndZ=0
    g2: LineSegment [constr] StartX=103.5 StartY=55 StartZ=0 EndX=176.5 EndY=55 EndZ=0
    g3: LineSegment [constr] StartX=176.5 StartY=55 StartZ=0 EndX=176.5 EndY=170 EndZ=0
    g4: LineSegment [constr] StartX=95.5 StartY=170 StartZ=0 EndX=22.5 EndY=170 EndZ=0
    g5: LineSegment [constr] StartX=22.5 StartY=170 StartZ=0 EndX=22.5 EndY=55 EndZ=0
    g6: LineSegment [constr] StartX=22.5 StartY=55 StartZ=0 EndX=95.5 EndY=55 EndZ=0
    g7: LineSegment [constr] StartX=95.5 StartY=55 StartZ=0 EndX=95.5 EndY=170 EndZ=0
    g8: Circle CenterX=74.5 CenterY=62.7 CenterZ=0 NormalX=0 NormalY=0 NormalZ=1 AngleXU=0 Radius=1.25
    g9: Circle CenterX=34 CenterY=62.7 CenterZ=0 NormalX=0 NormalY=0 NormalZ=1 AngleXU=0 Radius=1.25
    g10: Circle CenterX=155.5 CenterY=62.7 CenterZ=0 NormalX=0 NormalY=0 NormalZ=1 AngleXU=0 Radius=1.25
    g11: Circle CenterX=115 CenterY=62.7 CenterZ=0 NormalX=0 NormalY=0 NormalZ=1 AngleXU=0 Radius=1.25
  constraints (36):
    c: Coincident(g0,g1)
    c: Coincident(g1,g2)
    c: Coincident(g2,g3)
    c: Coincident(g3,g0)
    c: Horizontal(g0)
    c: Horizontal(g2)
    c: Vertical(g1)
    c: Vertical(g3)
    c: Coincident(g4,g5)
    c: Coincident(g5,g6)
    c: Coincident(g6,g7)
    c: Coincident(g7,g4)
    c: Horizontal(g4)
    c: Horizontal(g6)
    c: Vertical(g5)
    c: Vertical(g7)
    c: Equal(g2,g6)
    c: Equal(g3,g5)
    c: Horizontal(g1,g6)
    c: DistanceX(g0,g0) = 73
    c: Distance(g2,g-3) = 8
    c: Distance(g7,g1) = 8
    c: DistanceY(g3,g3) = 115
    c: Diameter(g8) = 2.5
    c: Diameter(g9) = 2.5
    c: Diameter(g10) = 2.5
    c: Diameter(g11) = 2.5
    c: Horizontal(g10,g11)
    c: Horizontal(g11,g8)
    c: Horizontal(g8,g9)
    c: Distance(g10,g3) = 21
    c: Distance(g11,g1) = 11.5
    c: Distance(g8,g7) = 21
    c: Distance(g9,g5) = 11.5
    c: Distance(g10,g2) = 7.7
    c: DistanceY(g0,g-3) = 5
FEATURE [PartDesign::Hole] Hole029  label="side ssd holes"
  BaseFeature = -> Hole028
  CustomThreadClearance = 0
  Depth = 4
  DepthType = 0
  Diameter = 2.9
  DrillForDepth = false
  DrillPoint = 0
  DrillPointAngle = 118
  HoleCutCountersinkAngle = 90
  HoleCutCustomValues = false
  HoleCutDepth = 1
  HoleCutDiameter = 5
  HoleCutType = 1
  ModelThread = false
  Profile = -> Sketch062
  Refine = true
  Suppressed = false
  Tapered = false
  TaperedAngle = 90
  ThreadClass = 0
  ThreadDepth = 4
  ThreadDepthType = 0
  ThreadDirection = 0
  ThreadFit = 0
  ThreadSize = 8
  ThreadType = 1
  Threaded = false
  UseCustomThreadClearance = false
  expr: Depth = Spreadsheet.wall_thickness
FEATURE [Sketcher::SketchObject] Sketch065
  ArcFitTolerance = 1e-06
  AttachmentOffset = pos=(0,0,-1.5) rot=(0,0,1;0rad)
  AttachmentSupport = -> [Hole019]
  ExternalGeometry = -> [Hole019]
  FullyConstrained = true
  MakeInternals = false
  MapMode = 5
  Placement = pos=(0,0,6.5) rot=(0,0,1;0rad)
  sketch-geometry (42):
    g0: LineSegment StartX=-145.9 StartY=-178.45 StartZ=0 EndX=-150.9 EndY=-178.45 EndZ=0
    g1: LineSegment StartX=-150.9 StartY=-178.45 StartZ=0 EndX=-150.9 EndY=-180.95 EndZ=0
    g2: LineSegment StartX=-150.9 StartY=-180.95 StartZ=0 EndX=-145.9 EndY=-180.95 EndZ=0
    g3: LineSegment StartX=-145.9 StartY=-180.95 StartZ=0 EndX=-145.9 EndY=-178.45 EndZ=0
    g4: LineSegment StartX=-85.9 StartY=-178.45 StartZ=0 EndX=-90.9 EndY=-178.45 EndZ=0
    g5: LineSegment StartX=-90.9 StartY=-178.45 StartZ=0 EndX=-90.9 EndY=-180.95 EndZ=0
    g6: LineSegment StartX=-90.9 StartY=-180.95 StartZ=0 EndX=-85.9 EndY=-180.95 EndZ=0
    g7: LineSegment StartX=-85.9 StartY=-180.95 StartZ=0 EndX=-85.9 EndY=-178.45 EndZ=0
    g8: LineSegment StartX=-10.9 StartY=-178.45 StartZ=0 EndX=-15.9 EndY=-178.45 EndZ=0
    g9: LineSegment StartX=-15.9 StartY=-178.45 StartZ=0 EndX=-15.9 EndY=-180.95 EndZ=0
    g10: LineSegment StartX=-15.9 StartY=-180.95 StartZ=0 EndX=-10.9 EndY=-180.95 EndZ=0
    g11: LineSegment StartX=-10.9 StartY=-180.95 StartZ=0 EndX=-10.9 EndY=-178.45 EndZ=0
    g12: LineSegment StartX=49.1 StartY=-178.45 StartZ=0 EndX=44.1 EndY=-178.45 EndZ=0
    g13: LineSegment StartX=44.1 StartY=-178.45 StartZ=0 EndX=44.1 EndY=-180.95 EndZ=0
    g14: LineSegment StartX=44.1 StartY=-180.95 StartZ=0 EndX=49.1 EndY=-180.95 EndZ=0
    g15: LineSegment StartX=49.1 StartY=-180.95 StartZ=0 EndX=49.1 EndY=-178.45 EndZ=0
    g16: LineSegment StartX=122.5 StartY=-178.45 StartZ=0 EndX=117.5 EndY=-178.45 EndZ=0
    g17: LineSegment StartX=117.5 StartY=-178.45 StartZ=0 EndX=117.5 EndY=-180.95 EndZ=0
    g18: LineSegment StartX=117.5 StartY=-180.95 StartZ=0 EndX=122.5 EndY=-180.95 EndZ=0
    g19: LineSegment StartX=122.5 StartY=-180.95 StartZ=0 EndX=122.5 EndY=-178.45 EndZ=0
    g20: LineSegment StartX=182.5 StartY=-178.45 StartZ=0 EndX=177.5 EndY=-178.45 EndZ=0
    g21: LineSegment StartX=177.5 StartY=-178.45 StartZ=0 EndX=177.5 EndY=-180.95 EndZ=0
    g22: LineSegment StartX=177.5 StartY=-180.95 StartZ=0 EndX=182.5 EndY=-180.95 EndZ=0
    g23: LineSegment StartX=182.5 StartY=-180.95 StartZ=0 EndX=182.5 EndY=-178.45 EndZ=0
    g24: GeomPoint [constr] X=-148.4 Y=-186.5 Z=0
    g25: GeomPoint [constr] X=-88.4 Y=-186.5 Z=0
    g26: GeomPoint [constr] X=-13.4 Y=-186.5 Z=0
    g27: GeomPoint [constr] X=46.6 Y=-186.5 Z=0
    g28: GeomPoint [constr] X=120 Y=-186.5 Z=0
    g29: GeomPoint [constr] X=180 Y=-186.5 Z=0
    g30: GeomPoint [constr] X=180 Y=-180.95 Z=0
    g31: GeomPoint [constr] X=120 Y=-180.95 Z=0
    g32: GeomPoint [constr] X=46.6 Y=-180.95 Z=0
    g33: GeomPoint [constr] X=-13.4 Y=-180.95 Z=0
    g34: GeomPoint [constr] X=-88.4 Y=-180.95 Z=0
    g35: GeomPoint [constr] X=-148.4 Y=-180.95 Z=0
    g36: LineSegment [constr] StartX=-148.4 StartY=-180.95 StartZ=0 EndX=-148.4 EndY=-186.5 EndZ=0
    g37: LineSegment [constr] StartX=-88.4 StartY=-180.95 StartZ=0 EndX=-88.4 EndY=-186.5 EndZ=0
    g38: LineSegment [constr] StartX=-13.4 StartY=-180.95 StartZ=0 EndX=-13.4 EndY=-186.5 EndZ=0
    g39: LineSegment [constr] StartX=46.6 StartY=-180.95 StartZ=0 EndX=46.6 EndY=-186.5 EndZ=0
    g40: LineSegment [constr] StartX=120 StartY=-180.95 StartZ=0 EndX=120 EndY=-186.5 EndZ=0
    g41: LineSegment [constr] StartX=180 StartY=-180.95 StartZ=0 EndX=180 EndY=-186.5 EndZ=0
  constraints (96):
    c: Coincident(g0,g1)
    c: Coincident(g1,g2)
    c: Coincident(g2,g3)
    c: Coincident(g3,g0)
    c: Horizontal(g0)
    c: Horizontal(g2)
    c: Vertical(g1)
    c: Vertical(g3)
    c: DistanceY(g3,g3) = 2.5
    c: DistanceX(g0,g0) = 5
    c: Coincident(g4,g5)
    c: Coincident(g5,g6)
    c: Coincident(g6,g7)
    c: Coincident(g7,g4)
    c: Horizontal(g4)
    c: Horizontal(g6)
    c: Vertical(g5)
    c: Vertical(g7)
    c: Coincident(g8,g9)
    c: Coincident(g9,g10)
    c: Coincident(g10,g11)
    c: Coincident(g11,g8)
    c: Horizontal(g8)
    c: Horizontal(g10)
    c: Vertical(g9)
    c: Vertical(g11)
    c: Coincident(g12,g13)
    c: Coincident(g13,g14)
    c: Coincident(g14,g15)
    c: Coincident(g15,g12)
    c: Horizontal(g12)
    c: Horizontal(g14)
    c: Vertical(g13)
    c: Vertical(g15)
    c: Coincident(g16,g17)
    c: Coincident(g17,g18)
    c: Coincident(g18,g19)
    c: Coincident(g19,g16)
    c: Horizontal(g16)
    c: Horizontal(g18)
    c: Vertical(g17)
    c: Vertical(g19)
    c: Coincident(g20,g21)
    c: Coincident(g21,g22)
    c: Coincident(g22,g23)
    c: Coincident(g23,g20)
    c: Horizontal(g20)
    c: Horizontal(g22)
    c: Vertical(g21)
    c: Vertical(g23)
    c: Equal(g23,g19)
    c: Equal(g19,g15)
    c: Equal(g15,g11)
    c: Equal(g11,g7)
    c: Equal(g7,g3)
    c: Equal(g2,g6)
    c: Equal(g6,g10)
    c: Equal(g10,g14)
    c: Equal(g14,g18)
    c: Equal(g18,g22)
    c: Horizontal(g21,g17)
    c: Horizontal(g17,g13)
    c: Horizontal(g13,g9)
    c: Horizontal(g9,g5)
    c: Horizontal(g5,g1)
    c: Symmetric(g22,g22,g30)
    c: Symmetric(g18,g18,g31)
    c: Symmetric(g14,g14,g32)
    c: Symmetric(g10,g10,g33)
    c: Symmetric(g6,g6,g34)
    c: Symmetric(g2,g2,g35)
    c: Coincident(g36,g35)
    c: Coincident(g36,g24)
    c: Vertical(g36)
    c: Coincident(g37,g34)
    c: Coincident(g37,g25)
    c: Coincident(g38,g33)
    c: Coincident(g38,g26)
    c: Coincident(g39,g32)
    c: Coincident(g39,g27)
    c: Coincident(g40,g31)
    c: Coincident(g40,g28)
    c: Coincident(g41,g30)
    c: Coincident(g41,g29)
    c: Vertical(g41)
    c: Vertical(g40)
    c: Vertical(g39)
    c: Vertical(g38)
    c: Vertical(g37)
    c: Symmetric(g-8,g-8,g29)
    c: Symmetric(g-7,g-7,g28)
    c: Symmetric(g-6,g-6,g27)
    c: Symmetric(g-5,g-5,g26)
    c: Symmetric(g-4,g-4,g25)
    c: Symmetric(g-3,g-3,g24)
    c: DistanceY(g2,g-9) = 0.5
FEATURE [PartDesign::Pocket] Pocket025  label="front wall nuts pocket"
  BaseFeature = -> Hole029
  Direction = (0,0,-1)
  Length = 5
  Length2 = 5
  Profile = -> Sketch065
  ReferenceAxis = -> Sketch065 [N_Axis]
  Refine = true
  Suppressed = false
  Type = 0
FEATURE [Sketcher::SketchObject] Sketch066
  ArcFitTolerance = 1e-06
  AttachmentSupport = -> [Pocket025]
  FullyConstrained = false
  MakeInternals = false
  MapMode = 5
  Placement = pos=(0,0,0) rot=(1,0,0;3.14159rad)
  sketch-geometry (1):
    g0: LineSegment StartX=245.328 StartY=184.5 StartZ=0 EndX=-227.927 EndY=184.5 EndZ=0
  constraints (2):
    c: PointOnObject(g0,g-3)
    c: Horizontal(g0)
FEATURE [Sketcher::SketchObject] Sketch081
  ArcFitTolerance = 1e-06
  AttachmentSupport = -> [Hole029]
  FullyConstrained = true
  MakeInternals = false
  MapMode = 5
  Placement = pos=(1.058e-13,187.5,0) rot=(0,0.707107,0.707107;3.14159rad)
  sketch-geometry (4):
    g0: Circle CenterX=-205 CenterY=14 CenterZ=0 NormalX=0 NormalY=0 NormalZ=1 AngleXU=0 Radius=1.7525
    g1: Circle CenterX=-141 CenterY=14 CenterZ=0 NormalX=0 NormalY=0 NormalZ=1 AngleXU=0 Radius=1.7525
    g2: Circle CenterX=-205 CenterY=152 CenterZ=0 NormalX=0 NormalY=0 NormalZ=1 AngleXU=0 Radius=1.7525
    g3: Circle CenterX=-131 CenterY=128 CenterZ=0 NormalX=0 NormalY=0 NormalZ=1 AngleXU=0 Radius=1.7525
  constraints (8):
    c: Coincident(g0,g-5)
    c: Equal(g0,g-5)
    c: Coincident(g1,g-6)
    c: Equal(g1,g-6)
    c: Coincident(g2,g-3)
    c: Equal(g2,g-3)
    c: Coincident(g3,g-4)
    c: Equal(g3,g-4)
FEATURE [PartDesign::Hole] Hole030  label="PSU screws"
  BaseFeature = -> Pocket025
  CustomThreadClearance = 0
  Depth = 4
  DepthType = 0
  Diameter = 4.3
  DrillForDepth = false
  DrillPoint = 0
  DrillPointAngle = 118
  HoleCutCountersinkAngle = 90
  HoleCutCustomValues = false
  HoleCutDepth = 2
  HoleCutDiameter = 8
  HoleCutType = 2
  ModelThread = false
  Profile = -> Sketch081
  Refine = true
  Suppressed = false
  Tapered = false
  TaperedAngle = 90
  ThreadClass = 0
  ThreadDepth = 4
  ThreadDepthType = 0
  ThreadDirection = 0
  ThreadFit = 0
  ThreadSize = 5
  ThreadType = 3
  Threaded = false
  UseCustomThreadClearance = false
  expr: Depth = Spreadsheet.wall_thickness
FEATURE [Sketcher::SketchObject] Sketch083
  ArcFitTolerance = 1e-06
  AttachmentSupport = -> [Hole029]
  FullyConstrained = true
  MakeInternals = false
  MapMode = 5
  Placement = pos=(0,0,130) rot=(1,0,0;3.14159rad)
  sketch-geometry (7):
    g0: Circle CenterX=-167.02 CenterY=-177.15 CenterZ=0 NormalX=0 NormalY=0 NormalZ=1 AngleXU=0 Radius=3.5
    g1: Circle CenterX=-146.72 CenterY=-177.15 CenterZ=0 NormalX=0 NormalY=0 NormalZ=1 AngleXU=0 Radius=3.5
    g2: Circle CenterX=-126.42 CenterY=-177.15 CenterZ=0 NormalX=0 NormalY=0 NormalZ=1 AngleXU=0 Radius=3.5
    g3: Circle CenterX=-106.12 CenterY=-177.15 CenterZ=0 NormalX=0 NormalY=0 NormalZ=1 AngleXU=0 Radius=3.5
    g4: Circle CenterX=-85.82 CenterY=-177.15 CenterZ=0 NormalX=0 NormalY=0 NormalZ=1 AngleXU=0 Radius=3.5
    g5: Circle CenterX=-65.52 CenterY=-177.15 CenterZ=0 NormalX=0 NormalY=0 NormalZ=1 AngleXU=0 Radius=3.5
    g6: Circle CenterX=-45.22 CenterY=-177.15 CenterZ=0 NormalX=0 NormalY=0 NormalZ=1 AngleXU=0 Radius=3.5
  constraints (14):
    c: Coincident(g0,g-3)
    c: Coincident(g1,g-4)
    c: Coincident(g2,g-5)
    c: Coincident(g3,g-6)
    c: Coincident(g4,g-7)
    c: Coincident(g5,g-8)
    c: Coincident(g6,g-9)
    c: Equal(g6,g5)
    c: Equal(g5,g4)
    c: Equal(g4,g3)
    c: Equal(g3,g2)
    c: Equal(g2,g1)
    c: Equal(g1,g0)
    c: Diameter(g0) = 7
FEATURE [PartDesign::Pocket] Pocket027
  BaseFeature = -> Hole030
  Direction = (0,0,1)
  Length = 1.5
  Length2 = 10
  Profile = -> Sketch083
  ReferenceAxis = -> Sketch083 [N_Axis]
  Refine = true
  Suppressed = false
  Type = 4
FEATURE [PartDesign::Fillet] Fillet
  Base = -> Pocket027 [Edge523,Edge531,Edge539,Edge547,Edge555,Edge563,Edge571,Edge2783,Edge2773,Edge2763,Edge2753,Edge2743,Edge2733,Edge2717]
  BaseFeature = -> Pocket027
  Radius = 0.5
  Refine = true
  SupportTransform = false
  Suppressed = false
  UseAllEdges = false
FEATURE [PartDesign::Hole] Hole033  label="pcie fasteners001"
  BaseFeature = -> Fillet
  CustomThreadClearance = 0
  Depth = 4
  DepthType = 0
  Diameter = 4.3
  DrillForDepth = false
  DrillPoint = 0
  DrillPointAngle = 118
  HoleCutCountersinkAngle = 90
  HoleCutCustomValues = false
  HoleCutDepth = 0
  HoleCutDiameter = 6.1
  HoleCutType = 0
  ModelThread = false
  Profile = -> Sketch011
  Refine = true
  Suppressed = false
  Tapered = false
  TaperedAngle = 90
  ThreadClass = 0
  ThreadDepth = 4
  ThreadDepthType = 0
  ThreadDirection = 0
  ThreadFit = 0
  ThreadSize = 5
  ThreadType = 3
  Threaded = false
  UseCustomThreadClearance = false
  expr: Depth = Spreadsheet.wall_thickness
FEATURE [Sketcher::SketchObject] Sketch086
  ArcFitTolerance = 1e-06
  AttachmentSupport = -> [Hole033]
  FullyConstrained = true
  MakeInternals = false
  MapMode = 5
  Placement = pos=(-215,0,0) rot=(0.57735,-0.57735,-0.57735;2.0944rad)
  sketch-geometry (7):
    g0: LineSegment [constr] StartX=10.5 StartY=148 StartZ=0 EndX=2.5 EndY=148 EndZ=0
    g1: GeomPoint [constr] X=6.5 Y=148 Z=0
    g2: GeomPoint [constr] X=6.5 Y=172.5 Z=0
    g3: LineSegment StartX=6.5 StartY=172.5 StartZ=0 EndX=6.5 EndY=167.5 EndZ=0
    g4: LineSegment StartX=6.5 StartY=167.5 StartZ=0 EndX=184.5 EndY=167.5 EndZ=0
    g5: LineSegment StartX=184.5 StartY=167.5 StartZ=0 EndX=184.5 EndY=172.5 EndZ=0
    g6: LineSegment StartX=184.5 StartY=172.5 StartZ=0 EndX=6.5 EndY=172.5 EndZ=0
  constraints (15):
    c: Coincident(g0,g-4)
    c: Coincident(g0,g-5)
    c: Symmetric(g0,g0,g1)
    c: Vertical(g2,g1)
    c: PointOnObject(g2,g-3)
    c: Coincident(g3,g4)
    c: Coincident(g4,g5)
    c: Coincident(g5,g6)
    c: Coincident(g6,g3)
    c: Vertical(g3)
    c: Vertical(g5)
    c: Horizontal(g4)
    c: Coincident(g3,g2)
    c: DistanceY(g3,g3) = 5
    c: Coincident(g5,g-3)
FEATURE [PartDesign::Pocket] Pocket029  label="left wall lip"
  BaseFeature = -> Hole033
  Direction = (1,0,0)
  Length = 2.1
  Length2 = 5
  Profile = -> Sketch086
  ReferenceAxis = -> Sketch086 [N_Axis]
  Refine = true
  Suppressed = false
  Type = 0
FEATURE [Sketcher::SketchObject] Sketch087
  ArcFitTolerance = 1e-06
  AttachmentSupport = -> [Pocket029]
  ExternalGeometry = -> [Pocket029]
  FullyConstrained = true
  MakeInternals = false
  MapMode = 5
  Placement = pos=(215,0,0) rot=(0.57735,0.57735,0.57735;2.0944rad)
  sketch-geometry (4):
    g0: LineSegment StartX=-184.5 StartY=172.5 StartZ=0 EndX=-184.5 EndY=167.5 EndZ=0
    g1: LineSegment StartX=-184.5 StartY=167.5 StartZ=0 EndX=-6.5 EndY=167.5 EndZ=0
    g2: LineSegment StartX=-6.5 StartY=167.5 StartZ=0 EndX=-6.5 EndY=172.5 EndZ=0
    g3: LineSegment StartX=-6.5 StartY=172.5 StartZ=0 EndX=-184.5 EndY=172.5 EndZ=0
  constraints (10):
    c: Coincident(g0,g1)
    c: Coincident(g1,g2)
    c: Coincident(g2,g3)
    c: Coincident(g3,g0)
    c: Vertical(g0)
    c: Vertical(g2)
    c: Horizontal(g1)
    c: Horizontal(g3)
    c: Coincident(g0,g-4)
    c: Coincident(g1,g-6)
FEATURE [PartDesign::Pocket] Pocket030  label="right wall lip"
  BaseFeature = -> Pocket029
  Direction = (-1,0,0)
  Length = 2.1
  Length2 = 5
  Profile = -> Sketch087
  ReferenceAxis = -> Sketch087 [N_Axis]
  Refine = true
  Suppressed = false
  Type = 0
FEATURE [Sketcher::SketchObject] Sketch099
  ArcFitTolerance = 1e-06
  AttachmentSupport = -> [Pocket025]
  ExternalGeometry = -> [Pocket025]
  FullyConstrained = true
  MakeInternals = false
  MapMode = 5
  Placement = pos=(0,-184.5,0) rot=(0,0.707107,0.707107;3.14159rad)
  sketch-geometry (24):
    g0: LineSegment StartX=-168.025 StartY=1.45 StartZ=0 EndX=-161.975 EndY=1.45 EndZ=0
    g1: LineSegment StartX=-161.975 StartY=1.45 StartZ=0 EndX=-161.975 EndY=7.5 EndZ=0
    g2: LineSegment StartX=-161.975 StartY=7.5 StartZ=0 EndX=-168.025 EndY=7.5 EndZ=0
    g3: LineSegment StartX=-168.025 StartY=7.5 StartZ=0 EndX=-168.025 EndY=1.45 EndZ=0
    g4: LineSegment StartX=-138.025 StartY=1.45 StartZ=0 EndX=-131.975 EndY=1.45 EndZ=0
    g5: LineSegment StartX=-131.975 StartY=1.45 StartZ=0 EndX=-131.975 EndY=7.5 EndZ=0
    g6: LineSegment StartX=-131.975 StartY=7.5 StartZ=0 EndX=-138.025 EndY=7.5 EndZ=0
    g7: LineSegment StartX=-138.025 StartY=7.5 StartZ=0 EndX=-138.025 EndY=1.45 EndZ=0
    g8: LineSegment StartX=-34.625 StartY=1.45 StartZ=0 EndX=-28.575 EndY=1.45 EndZ=0
    g9: LineSegment StartX=-28.575 StartY=1.45 StartZ=0 EndX=-28.575 EndY=7.5 EndZ=0
    g10: LineSegment StartX=-28.575 StartY=7.5 StartZ=0 EndX=-34.625 EndY=7.5 EndZ=0
    g11: LineSegment StartX=-34.625 StartY=7.5 StartZ=0 EndX=-34.625 EndY=1.45 EndZ=0
    g12: LineSegment StartX=-4.625 StartY=1.45 StartZ=0 EndX=1.425 EndY=1.45 EndZ=0
    g13: LineSegment StartX=1.425 StartY=1.45 StartZ=0 EndX=1.425 EndY=7.5 EndZ=0
    g14: LineSegment StartX=1.425 StartY=7.5 StartZ=0 EndX=-4.625 EndY=7.5 EndZ=0
    g15: LineSegment StartX=-4.625 StartY=7.5 StartZ=0 EndX=-4.625 EndY=1.45 EndZ=0
    g16: LineSegment StartX=100.375 StartY=1.45 StartZ=0 EndX=106.425 EndY=1.45 EndZ=0
    g17: LineSegment StartX=106.425 StartY=1.45 StartZ=0 EndX=106.425 EndY=7.5 EndZ=0
    g18: LineSegment StartX=106.425 StartY=7.5 StartZ=0 EndX=100.375 EndY=7.5 EndZ=0
    g19: LineSegment StartX=100.375 StartY=7.5 StartZ=0 EndX=100.375 EndY=1.45 EndZ=0
    g20: LineSegment StartX=130.375 StartY=1.45 StartZ=0 EndX=136.425 EndY=1.45 EndZ=0
    g21: LineSegment StartX=136.425 StartY=1.45 StartZ=0 EndX=136.425 EndY=7.5 EndZ=0
    g22: LineSegment StartX=136.425 StartY=7.5 StartZ=0 EndX=130.375 EndY=7.5 EndZ=0
    g23: LineSegment StartX=130.375 StartY=7.5 StartZ=0 EndX=130.375 EndY=1.45 EndZ=0
  constraints (60):
    c: Coincident(g0,g1)
    c: Coincident(g1,g2)
    c: Coincident(g2,g3)
    c: Coincident(g3,g0)
    c: Horizontal(g2)
    c: Vertical(g1)
    c: Vertical(g3)
    c: Coincident(g0,g-3)
    c: Coincident(g4,g5)
    c: Coincident(g5,g6)
    c: Coincident(g6,g7)
    c: Coincident(g7,g4)
    c: Horizontal(g6)
    c: Vertical(g5)
    c: Vertical(g7)
    c: Coincident(g4,g-4)
    c: Coincident(g8,g9)
    c: Coincident(g9,g10)
    c: Coincident(g10,g11)
    c: Coincident(g11,g8)
    c: Horizontal(g10)
    c: Vertical(g9)
    c: Vertical(g11)
    c: Coincident(g8,g-5)
    c: Coincident(g12,g13)
    c: Coincident(g13,g14)
    c: Coincident(g14,g15)
    c: Coincident(g15,g12)
    c: Horizontal(g14)
    c: Vertical(g13)
    c: Vertical(g15)
    c: Coincident(g12,g-6)
    c: Coincident(g16,g17)
    c: Coincident(g17,g18)
    c: Coincident(g18,g19)
    c: Coincident(g19,g16)
    c: Horizontal(g18)
    c: Vertical(g17)
    c: Vertical(g19)
    c: Coincident(g16,g-7)
    c: Coincident(g20,g21)
    c: Coincident(g21,g22)
    c: Coincident(g22,g23)
    c: Coincident(g23,g20)
    c: Horizontal(g22)
    c: Vertical(g21)
    c: Vertical(g23)
    c: Coincident(g20,g-8)
    c: Coincident(g-8,g20)
    c: Coincident(g-7,g16)
    c: Coincident(g-6,g12)
    c: Coincident(g-5,g8)
    c: Coincident(g-4,g4)
    c: Coincident(g-3,g0)
    c: Equal(g1,g0)
    c: Equal(g5,g4)
    c: Equal(g9,g8)
    c: Equal(g13,g12)
    c: Equal(g17,g16)
    c: Equal(g21,g20)
FEATURE [PartDesign::Pocket] Pocket036  label="front magnets - front wall"
  BaseFeature = -> Pocket030
  Direction = (0,-1,2e-16)
  Length = 3.05
  Length2 = 5
  Profile = -> Sketch099
  ReferenceAxis = -> Sketch099 [N_Axis]
  Refine = true
  Reversed = true
  Suppressed = false
  Type = 0
  expr: Length = Spreadsheet.magnet_thickness
FEATURE [Sketcher::SketchObject] Sketch102
  ArcFitTolerance = 1e-06
  FullyConstrained = true
  MakeInternals = false
  MapMode = 5
  Placement = pos=(0,0,8) rot=(0,0,1;0rad)
  sketch-geometry (4):
    g0: LineSegment StartX=-193 StartY=-88.93 StartZ=0 EndX=193 EndY=-88.93 EndZ=0
    g1: LineSegment StartX=193 StartY=-88.93 StartZ=0 EndX=193 EndY=-132.6 EndZ=0
    g2: LineSegment StartX=193 StartY=-132.6 StartZ=0 EndX=-193 EndY=-132.6 EndZ=0
    g3: LineSegment StartX=-193 StartY=-132.6 StartZ=0 EndX=-193 EndY=-88.93 EndZ=0
  constraints (12):
    c: Coincident(g0,g1)
    c: Coincident(g1,g2)
    c: Coincident(g2,g3)
    c: Coincident(g3,g0)
    c: Horizontal(g0)
    c: Horizontal(g2)
    c: Vertical(g1)
    c: Vertical(g3)
    c: DistanceY(g-4,g2) = 4
    c: Distance(g-8,g3) = 4
    c: Distance(g-7,g1) = 4
    c: DistanceY(g0,g-5) = 4
FEATURE [PartDesign::Pocket] Pocket037  label="drives pocket"
  BaseFeature = -> Pocket036
  Direction = (0,0,-1)
  Length = 6
  Length2 = 5
  Profile = -> Sketch102
  ReferenceAxis = -> Sketch102 [N_Axis]
  Refine = true
  Suppressed = false
  Type = 0
FEATURE [Sketcher::SketchObject] Sketch103
  ArcFitTolerance = 1e-06
  AttachmentSupport = -> [Pocket037]
  ExternalGeometry = -> [Pocket037]
  FullyConstrained = true
  MakeInternals = false
  MapMode = 5
  Placement = pos=(0,0,0) rot=(1,0,0;3.14159rad)
  sketch-geometry (4):
    g0: Circle CenterX=83.3 CenterY=136.6 CenterZ=0 NormalX=0 NormalY=0 NormalZ=1 AngleXU=0 Radius=1
    g1: Circle CenterX=-50.9 CenterY=136.6 CenterZ=0 NormalX=0 NormalY=0 NormalZ=1 AngleXU=0 Radius=1
    g2: Circle CenterX=202 CenterY=102.6 CenterZ=0 NormalX=0 NormalY=0 NormalZ=1 AngleXU=0 Radius=1
    g3: Circle CenterX=-202 CenterY=102.6 CenterZ=0 NormalX=0 NormalY=0 NormalZ=1 AngleXU=0 Radius=1
  constraints (10):
    c: Symmetric(g-5,g-12,g0)
    c: DistanceY(g3,g-14) = 4
    c: DistanceX(g3,g-14) = 5
    c: DistanceY(g2,g-13) = 4
    c: DistanceX(g-13,g2) = 5
    c: Equal(g2,g0)
    c: Equal(g0,g1)
    c: Equal(g1,g3)
    c: Diameter(g3) = 2
    c: Symmetric(g-4,g-3,g1)
FEATURE [PartDesign::Hole] Hole037  label="screws for drives pocket"
  BaseFeature = -> Pocket037
  CustomThreadClearance = 0
  Depth = 8
  DepthType = 0
  Diameter = 2.4
  DrillForDepth = false
  DrillPoint = 0
  DrillPointAngle = 118
  HoleCutCountersinkAngle = 90
  HoleCutCustomValues = false
  HoleCutDepth = 1.2
  HoleCutDiameter = 4.2
  HoleCutType = 1
  ModelThread = false
  Profile = -> Sketch103
  Refine = true
  Suppressed = false
  Tapered = false
  TaperedAngle = 90
  ThreadClass = 0
  ThreadDepth = 8
  ThreadDepthType = 0
  ThreadDirection = 0
  ThreadFit = 0
  ThreadSize = 6
  ThreadType = 1
  Threaded = false
  UseCustomThreadClearance = false
  expr: Depth = Spreadsheet.bottom_thickness
FEATURE [Sketcher::SketchObject] Sketch104
  ArcFitTolerance = 1e-06
  AttachmentOffset = pos=(0,0,32) rot=(0,0,1;0rad)
  AttachmentSupport = -> [Hole037]
  ExternalGeometry = -> [Hole037]
  FullyConstrained = true
  MakeInternals = false
  MapMode = 5
  Placement = pos=(0,0,40) rot=(0,0,1;0rad)
  sketch-geometry (6):
    g0: LineSegment StartX=-211 StartY=-178.5 StartZ=0 EndX=-209 EndY=-178.5 EndZ=0
    g1: LineSegment StartX=-209 StartY=-178.5 StartZ=0 EndX=-209 EndY=-182.5 EndZ=0
    g2: LineSegment StartX=-209 StartY=-182.5 StartZ=0 EndX=-205 EndY=-182.5 EndZ=0
    g3: LineSegment StartX=-205 StartY=-182.5 StartZ=0 EndX=-205 EndY=-184.5 EndZ=0
    g4: LineSegment StartX=-205 StartY=-184.5 StartZ=0 EndX=-211 EndY=-184.5 EndZ=0
    g5: LineSegment StartX=-211 StartY=-184.5 StartZ=0 EndX=-211 EndY=-178.5 EndZ=0
  constraints (18):
    c: PointOnObject(g0,g-4)
    c: Coincident(g0,g1)
    c: Vertical(g1)
    c: Coincident(g1,g2)
    c: Coincident(g2,g3)
    c: PointOnObject(g3,g-3)
    c: Coincident(g3,g4)
    c: Horizontal(g4)
    c: Coincident(g4,g5)
    c: Coincident(g5,g0)
    c: Vertical(g5)
    c: Horizontal(g0)
    c: Horizontal(g2)
    c: Vertical(g3)
    c: Equal(g4,g5)
    c: Equal(g0,g3)
    c: DistanceX(g4,g4) = 6
    c: DistanceY(g3,g3) = 2
FEATURE [PartDesign::Pad] Pad026  label="front left support"
  BaseFeature = -> Hole037
  Direction = (0,0,1)
  Length = 103
  Length2 = 10
  Profile = -> Sketch104
  ReferenceAxis = -> Sketch104 [N_Axis]
  Refine = true
  Suppressed = false
  Type = 0
FEATURE [Sketcher::SketchObject] Sketch105
  ArcFitTolerance = 1e-06
  AttachmentSupport = -> [Pad026]
  ExternalGeometry = -> [Pad026]
  FullyConstrained = true
  MakeInternals = false
  MapMode = 5
  Placement = pos=(-215,0,0) rot=(0.57735,-0.57735,-0.57735;2.0944rad)
  sketch-geometry (8):
    g0: GeomPoint [constr] X=180.5 Y=167.5 Z=0
    g1: LineSegment [constr] StartX=180.5 StartY=167.5 StartZ=0 EndX=180.5 EndY=127.625 EndZ=0
    g2: LineSegment [constr] StartX=180.5 StartY=127.625 StartZ=0 EndX=180.5 EndY=87.75 EndZ=0
    g3: LineSegment [constr] StartX=180.5 StartY=87.75 StartZ=0 EndX=180.5 EndY=47.875 EndZ=0
    g4: LineSegment [constr] StartX=180.5 StartY=47.875 StartZ=0 EndX=180.5 EndY=8 EndZ=0
    g5: Circle CenterX=180.5 CenterY=47.875 CenterZ=0 NormalX=0 NormalY=0 NormalZ=1 AngleXU=0 Radius=1.5
    g6: Circle CenterX=180.5 CenterY=87.75 CenterZ=0 NormalX=0 NormalY=0 NormalZ=1 AngleXU=0 Radius=1.5
    g7: Circle CenterX=180.5 CenterY=127.625 CenterZ=0 NormalX=0 NormalY=0 NormalZ=1 AngleXU=0 Radius=1.5
  constraints (20):
    c: Coincident(g1,g0)
    c: Vertical(g1)
    c: Coincident(g1,g2)
    c: Vertical(g2)
    c: Coincident(g2,g3)
    c: Vertical(g3)
    c: Coincident(g3,g4)
    c: Vertical(g4)
    c: Equal(g1,g2)
    c: Equal(g2,g3)
    c: Equal(g3,g4)
    c: Coincident(g5,g3)
    c: Coincident(g6,g2)
    c: Coincident(g7,g1)
    c: Equal(g7,g6)
    c: Equal(g6,g5)
    c: Diameter(g7) = 3
    c: DistanceX(g0,g-3) = 4
    c: PointOnObject(g4,g-4)
    c: PointOnObject(g0,g-3)
FEATURE [PartDesign::Hole] Hole038  label="front left support holes - left"
  BaseFeature = -> Pad026
  CustomThreadClearance = 0
  Depth = 25
  DepthType = 0
  Diameter = 2.4
  DrillForDepth = false
  DrillPoint = 0
  DrillPointAngle = 118
  HoleCutCountersinkAngle = 90
  HoleCutCustomValues = false
  HoleCutDepth = 1
  HoleCutDiameter = 4.2
  HoleCutType = 1
  ModelThread = false
  Profile = -> Sketch105
  Refine = true
  Suppressed = false
  Tapered = false
  TaperedAngle = 90
  ThreadClass = 0
  ThreadDepth = 25
  ThreadDepthType = 0
  ThreadDirection = 0
  ThreadFit = 0
  ThreadSize = 6
  ThreadType = 1
  Threaded = false
  UseCustomThreadClearance = false
FEATURE [Sketcher::SketchObject] Sketch106
  ArcFitTolerance = 1e-06
  AttachmentSupport = -> [Hole038]
  ExternalGeometry = -> [Hole038]
  FullyConstrained = true
  MakeInternals = false
  MapMode = 5
  Placement = pos=(0,-187.5,0) rot=(1,0,0;1.5708rad)
  sketch-geometry (15):
    g0: LineSegment [constr] StartX=-215 StartY=49.975 StartZ=0 EndX=-207 EndY=49.975 EndZ=0
    g1: LineSegment [constr] StartX=-207 StartY=49.975 StartZ=0 EndX=-207 EndY=85.65 EndZ=0
    g2: LineSegment [constr] StartX=-207 StartY=85.65 StartZ=0 EndX=-215 EndY=85.65 EndZ=0
    g3: LineSegment [constr] StartX=-215 StartY=125.525 StartZ=0 EndX=-207 EndY=125.525 EndZ=0
    g4: LineSegment [constr] StartX=-207 StartY=125.525 StartZ=0 EndX=-207 EndY=89.85 EndZ=0
    g5: LineSegment [constr] StartX=-207 StartY=89.85 StartZ=0 EndX=-215 EndY=89.85 EndZ=0
    g6: LineSegment [constr] StartX=-211 StartY=143 StartZ=0 EndX=-207 EndY=143 EndZ=0
    g7: LineSegment [constr] StartX=-207 StartY=143 StartZ=0 EndX=-207 EndY=129.725 EndZ=0
    g8: LineSegment [constr] StartX=-207 StartY=129.725 StartZ=0 EndX=-215 EndY=129.725 EndZ=0
    g9: GeomPoint [constr] X=-207 Y=67.8125 Z=0
    g10: GeomPoint [constr] X=-207 Y=107.688 Z=0
    g11: GeomPoint [constr] X=-207 Y=136.363 Z=0
    g12: Circle CenterX=-207 CenterY=136.363 CenterZ=0 NormalX=0 NormalY=0 NormalZ=1 AngleXU=0 Radius=1.5
    g13: Circle CenterX=-207 CenterY=107.688 CenterZ=0 NormalX=0 NormalY=0 NormalZ=1 AngleXU=0 Radius=1.5
    g14: Circle CenterX=-207 CenterY=67.8125 CenterZ=0 NormalX=0 NormalY=0 NormalZ=1 AngleXU=0 Radius=1.5
  constraints (33):
    c: Coincident(g-6,g0)
    c: Horizontal(g0)
    c: Coincident(g0,g1)
    c: Vertical(g1)
    c: Coincident(g1,g2)
    c: Coincident(g2,g-5)
    c: Horizontal(g2)
    c: Coincident(g-4,g3)
    c: Horizontal(g3)
    c: Coincident(g3,g4)
    c: Vertical(g4)
    c: Coincident(g4,g5)
    c: Coincident(g5,g-5)
    c: Coincident(g-3,g6)
    c: Horizontal(g6)
    c: Coincident(g6,g7)
    c: Vertical(g7)
    c: Coincident(g7,g8)
    c: Coincident(g8,g-4)
    c: Horizontal(g8)
    c: Horizontal(g5)
    c: Vertical(g7,g4)
    c: Vertical(g4,g0)
    c: Symmetric(g1,g1,g9)
    c: Symmetric(g4,g4,g10)
    c: Symmetric(g7,g7,g11)
    c: Coincident(g12,g11)
    c: Coincident(g13,g10)
    c: Coincident(g14,g9)
    c: Equal(g14,g13)
    c: Equal(g13,g12)
    c: Diameter(g12) = 3
    c: DistanceX(g6,g6) = 4
FEATURE [PartDesign::Hole] Hole039  label="front left support holes - front"
  BaseFeature = -> Hole038
  CustomThreadClearance = 0
  Depth = 25
  DepthType = 0
  Diameter = 2.4
  DrillForDepth = false
  DrillPoint = 0
  DrillPointAngle = 118
  HoleCutCountersinkAngle = 90
  HoleCutCustomValues = false
  HoleCutDepth = 1
  HoleCutDiameter = 4.2
  HoleCutType = 1
  ModelThread = false
  Profile = -> Sketch106
  Refine = true
  Suppressed = false
  Tapered = false
  TaperedAngle = 90
  ThreadClass = 0
  ThreadDepth = 25
  ThreadDepthType = 0
  ThreadDirection = 0
  ThreadFit = 0
  ThreadSize = 6
  ThreadType = 1
  Threaded = false
  UseCustomThreadClearance = false
FEATURE [Sketcher::SketchObject] Sketch108
  ArcFitTolerance = 1e-06
  AttachmentSupport = -> [Hole039]
  ExternalGeometry = -> [Hole039]
  FullyConstrained = true
  MakeInternals = false
  MapMode = 5
  Placement = pos=(0,187.5,8.46e-14) rot=(0,0.707107,0.707107;3.14159rad)
  sketch-geometry (4):
    g0: LineSegment StartX=215 StartY=130 StartZ=0 EndX=207 EndY=130 EndZ=0
    g1: LineSegment StartX=207 StartY=130 StartZ=0 EndX=207 EndY=-8.53e-14 EndZ=0
    g2: LineSegment StartX=207 StartY=-8.53e-14 StartZ=0 EndX=215 EndY=-8.53e-14 EndZ=0
    g3: LineSegment StartX=215 StartY=-8.53e-14 StartZ=0 EndX=215 EndY=130 EndZ=0
  constraints (11):
    c: Coincident(g0,g1)
    c: Coincident(g1,g2)
    c: Coincident(g2,g3)
    c: Coincident(g3,g0)
    c: Horizontal(g0)
    c: Horizontal(g2)
    c: Vertical(g1)
    c: Vertical(g3)
    c: Horizontal(g0,g-4)
    c: PointOnObject(g0,g-5)
    c: Coincident(g2,g-3)
FEATURE [PartDesign::Pocket] Pocket038  label="rear wall shaper"
  BaseFeature = -> Hole039
  Direction = (0,-1,2e-16)
  Length = 4
  Length2 = 5
  Profile = -> Sketch108
  ReferenceAxis = -> Sketch108 [N_Axis]
  Refine = true
  Suppressed = false
  Type = 0
  expr: Length = Spreadsheet.wall_thickness
FEATURE [PartDesign::Body] Body
  AllowCompound = false
  Group = -> [Sketch,Pad,Sketch001,Pad001,Sketch002,Pad002,Sketch003,Pad003,Sketch004,Pocket,Sketch006,Pad004,Sketch005,Pocket001,Sketch008,Sketch009,Pad006,Sketch011,Pocket003,Sketch016,Pocket007,MultiTransform,LinearPattern,LinearPattern004,Sketch020,Hole,ShapeString,ShapeString001,ShapeString002,ShapeString003,ShapeString004,ShapeString005,Sketch021,Pad016,Sketch022,Hole001,Sketch024,Hole003,Pocket010,+99 more]
  Origin = -> Origin
  Tip = -> Pocket038
FEATURE [Part::Extrusion] Extrude
  Base = -> Sketch066
  Dir = (0,0,-1)
  DirMode = 2
  FaceMakerClass = Part::FaceMakerBullseye
  FaceMakerMode = 3
  LengthFwd = 10
  LengthRev = 180
  Solid = false
  Symmetric = false
FEATURE [Part::FeaturePython] Slice  # WARN: FeaturePython — macro-defined, semantics opaque (R4)
  Base = -> Pocket038
  Mode = 1
  Tolerance = 0
  Tools = -> [Extrude]
FEATURE [Part::FeaturePython] Slice_child0  label="case without front wall"  # WARN: FeaturePython — macro-defined, semantics opaque (R4)
  Base = -> Slice
  FilterType = 1
  Invert = false
  OverrideMaxVal = 0
  WindowFrom = 80
  WindowTo = 100
  items = 0
FEATURE [Part::FeaturePython] Slice_child1  label="lone front wall"  # WARN: FeaturePython — macro-defined, semantics opaque (R4)
  Base = -> Slice
  FilterType = 1
  Invert = false
  OverrideMaxVal = 0
  WindowFrom = 80
  WindowTo = 100
  items = 1
FEATURE [App::DocumentObjectGroup] GrExplode_Slice  label="Exploded Slice"
  Group = -> [Slice_child0,Slice_child1]
FEATURE [PartDesign::FeatureBase] BaseFeature
  BaseFeature = -> Slice_child0
  Suppressed = false
FEATURE [Sketcher::SketchObject] Sketch109
  ArcFitTolerance = 1e-06
  AttachmentSupport = -> [BaseFeature]
  ExternalGeometry = -> [BaseFeature]
  FullyConstrained = false
  MakeInternals = false
  MapMode = 5
  Placement = pos=(0,-184.4,0) rot=(1,0,0;1.5708rad)
  sketch-geometry (1):
    g0: LineSegment StartX=-183.846 StartY=8 StartZ=0 EndX=210 EndY=8 EndZ=0
  constraints (2):
    c: Horizontal(g0)
    c: Coincident(g0,g-4)
FEATURE [PartDesign::Body] Body001  label="case without front wall body"
  AllowCompound = false
  BaseFeature = -> Slice_child0
  Group = -> [BaseFeature,Sketch109]
  Origin = -> Origin001
  Tip = -> BaseFeature
FEATURE [Part::Extrusion] Extrude001
  Base = -> Sketch109
  Dir = (0,-1,2e-16)
  DirMode = 2
  FaceMakerClass = Part::FaceMakerBullseye
  FaceMakerMode = 3
  LengthFwd = 180
  LengthRev = 180
  Solid = false
  Symmetric = false
FEATURE [Part::Extrusion] Extrude002
  Base = -> Sketch109
  Dir = (0,-1,2e-16)
  DirMode = 2
  FaceMakerClass = Part::FaceMakerBullseye
  FaceMakerMode = 3
  LengthFwd = 180
  LengthRev = 180
  Solid = false
  Symmetric = false
FEATURE [Part::FeaturePython] Slice001  # WARN: FeaturePython — macro-defined, semantics opaque (R4)
  Base = -> BaseFeature
  Mode = 1
  Tolerance = 0
  Tools = -> [Extrude001]
FEATURE [Part::FeaturePython] Slice001_child0  label="case without drive studs"  # WARN: FeaturePython — macro-defined, semantics opaque (R4)
  Base = -> Slice001
  FilterType = 1
  Invert = false
  OverrideMaxVal = 0
  WindowFrom = 80
  WindowTo = 100
  items = 0
FEATURE [Part::FeaturePython] Slice001_child1  label="large stud 1"  # WARN: FeaturePython — macro-defined, semantics opaque (R4)
  Base = -> Slice001
  FilterType = 1
  Invert = false
  OverrideMaxVal = 0
  WindowFrom = 80
  WindowTo = 100
  items = 1
FEATURE [Part::FeaturePython] Slice001_child2  label="small stud 1"  # WARN: FeaturePython — macro-defined, semantics opaque (R4)
  Base = -> Slice001
  FilterType = 1
  Invert = false
  OverrideMaxVal = 0
  WindowFrom = 80
  WindowTo = 100
  items = 2
FEATURE [Part::FeaturePython] Slice001_child3  label="large stud 2"  # WARN: FeaturePython — macro-defined, semantics opaque (R4)
  Base = -> Slice001
  FilterType = 1
  Invert = false
  OverrideMaxVal = 0
  WindowFrom = 80
  WindowTo = 100
  items = 3
FEATURE [Part::FeaturePython] Slice001_child4  label="small stud 2"  # WARN: FeaturePython — macro-defined, semantics opaque (R4)
  Base = -> Slice001
  FilterType = 1
  Invert = false
  OverrideMaxVal = 0
  WindowFrom = 80
  WindowTo = 100
  items = 4
FEATURE [Part::FeaturePython] Slice001_child5  label="large stud 3"  # WARN: FeaturePython — macro-defined, semantics opaque (R4)
  Base = -> Slice001
  FilterType = 1
  Invert = false
  OverrideMaxVal = 0
  WindowFrom = 80
  WindowTo = 100
  items = 5
FEATURE [Part::FeaturePython] Slice001_child6  label="small stud 3"  # WARN: FeaturePython — macro-defined, semantics opaque (R4)
  Base = -> Slice001
  FilterType = 1
  Invert = false
  OverrideMaxVal = 0
  WindowFrom = 80
  WindowTo = 100
  items = 6
FEATURE [App::DocumentObjectGroup] GrExplode_Slice001  label="Exploded Slice001"
  Group = -> [Slice001_child0,Slice001_child1,Slice001_child2,Slice001_child3,Slice001_child4,Slice001_child5,Slice001_child6]
FEATURE [PartDesign::FeatureBase] BaseFeature001
  BaseFeature = -> Slice_child1
  Suppressed = false
FEATURE [Sketcher::SketchObject] Sketch110
  ArcFitTolerance = 1e-06
  AttachmentSupport = -> [BaseFeature001]
  ExternalGeometry = -> [BaseFeature001]
  FullyConstrained = false
  MakeInternals = false
  MapMode = 5
  Placement = pos=(0,-187.5,0) rot=(1,0,0;1.5708rad)
  sketch-geometry (17):
    g0: LineSegment StartX=277.784 StartY=-56.7757 StartZ=0 EndX=83.35 EndY=-56.7757 EndZ=0
    g1: LineSegment StartX=83.35 StartY=-56.7757 StartZ=0 EndX=83.35 EndY=206.168 EndZ=0
    g2: LineSegment StartX=83.35 StartY=206.168 StartZ=0 EndX=83.25 EndY=206.168 EndZ=0
    g3: LineSegment StartX=83.25 StartY=206.168 StartZ=0 EndX=83.25 EndY=-68.2081 EndZ=0
    g4: LineSegment StartX=83.25 StartY=-68.2081 StartZ=0 EndX=-50.85 EndY=-68.2081 EndZ=0
    g5: LineSegment StartX=-50.85 StartY=-68.2081 StartZ=0 EndX=-50.85 EndY=211.445 EndZ=0
    g6: LineSegment StartX=-50.85 StartY=211.445 StartZ=0 EndX=-50.95 EndY=211.445 EndZ=0
    g7: LineSegment StartX=-50.95 StartY=211.445 StartZ=0 EndX=-50.95 EndY=-85.7357 EndZ=0
    g8: LineSegment StartX=-50.95 StartY=-85.7357 StartZ=0 EndX=-183.4 EndY=-85.7357 EndZ=0
    g9: LineSegment StartX=-183.4 StartY=-85.7357 StartZ=0 EndX=-183.4 EndY=200.073 EndZ=0
    g10: LineSegment StartX=-183.4 StartY=200.073 StartZ=0 EndX=-183.6 EndY=200.073 EndZ=0
    g11: LineSegment StartX=-183.6 StartY=200.073 StartZ=0 EndX=-183.6 EndY=-84.0375 EndZ=0
    g12: LineSegment StartX=-183.6 StartY=-84.0375 StartZ=0 EndX=-283.281 EndY=-84.0375 EndZ=0
    g13: GeomPoint [constr] X=83.3 Y=164.3 Z=0
    g14: GeomPoint [constr] X=-50.9 Y=164.3 Z=0
    g15: GeomPoint [constr] X=-50.9 Y=211.445 Z=0
    g16: GeomPoint [constr] X=83.3 Y=206.168 Z=0
  constraints (35):
    c: Horizontal(g0)
    c: Coincident(g0,g1)
    c: Vertical(g1)
    c: Coincident(g1,g2)
    c: Horizontal(g2)
    c: Coincident(g2,g3)
    c: Coincident(g3,g4)
    c: Horizontal(g4)
    c: Coincident(g4,g5)
    c: Coincident(g5,g6)
    c: Horizontal(g6)
    c: Coincident(g6,g7)
    c: Coincident(g7,g8)
    c: Horizontal(g8)
    c: Coincident(g8,g9)
    c: Vertical(g9)
    c: Coincident(g9,g10)
    c: Horizontal(g10)
    c: Coincident(g10,g11)
    c: Coincident(g11,g12)
    c: Horizontal(g12)
    c: Vertical(g11)
    c: Vertical(g7)
    c: Vertical(g5)
    c: Vertical(g3)
    c: Symmetric(g6,g6,g15)
    c: Symmetric(g2,g2,g16)
    c: DistanceX(g2,g2) = 0.1
    c: DistanceX(g6,g6) = 0.1
    c: DistanceX(g10,g10) = 0.2
    c: Vertical(g16,g13)
    c: Symmetric(g-3,g-4,g13)
    c: Symmetric(g-5,g-6,g14)
    c: Vertical(g14,g15)
    c: Distance(g-7,g9) = 5
FEATURE [PartDesign::Body] Body002  label="lone front wall body"
  AllowCompound = false
  BaseFeature = -> Slice_child1
  Group = -> [BaseFeature001,Sketch110]
  Origin = -> Origin002
  Tip = -> BaseFeature001
FEATURE [Part::Extrusion] Extrude003
  Base = -> Sketch110
  Dir = (0,-1,2e-16)
  DirMode = 2
  FaceMakerClass = Part::FaceMakerBullseye
  FaceMakerMode = 3
  LengthFwd = 10
  LengthRev = 10
  Solid = false
  Symmetric = false
FEATURE [Part::FeaturePython] Slice002  # WARN: FeaturePython — macro-defined, semantics opaque (R4)
  Base = -> BaseFeature001
  Mode = 1
  Tolerance = 0
  Tools = -> [Extrude003]
FEATURE [Part::FeaturePython] Slice002_child0  label="power button"  # WARN: FeaturePython — macro-defined, semantics opaque (R4)
  Base = -> Slice002
  FilterType = 1
  Invert = false
  OverrideMaxVal = 0
  WindowFrom = 80
  WindowTo = 100
  items = 0
FEATURE [Part::FeaturePython] Slice002_child1  label="Slice002.1"  # WARN: FeaturePython — macro-defined, semantics opaque (R4)
  Base = -> Slice002
  FilterType = 1
  Invert = false
  OverrideMaxVal = 0
  WindowFrom = 80
  WindowTo = 100
  items = 1
FEATURE [Part::FeaturePython] Slice002_child2  label="left mesh"  # WARN: FeaturePython — macro-defined, semantics opaque (R4)
  Base = -> Slice002
  FilterType = 1
  Invert = false
  OverrideMaxVal = 0
  WindowFrom = 80
  WindowTo = 100
  items = 2
FEATURE [Part::FeaturePython] Slice002_child3  label="Slice002.3"  # WARN: FeaturePython — macro-defined, semantics opaque (R4)
  Base = -> Slice002
  FilterType = 1
  Invert = false
  OverrideMaxVal = 0
  WindowFrom = 80
  WindowTo = 100
  items = 3
FEATURE [Part::FeaturePython] Slice002_child4  label="middle mesh"  # WARN: FeaturePython — macro-defined, semantics opaque (R4)
  Base = -> Slice002
  FilterType = 1
  Invert = false
  OverrideMaxVal = 0
  WindowFrom = 80
  WindowTo = 100
  items = 4
FEATURE [Part::FeaturePython] Slice002_child5  label="Slice002.5"  # WARN: FeaturePython — macro-defined, semantics opaque (R4)
  Base = -> Slice002
  FilterType = 1
  Invert = false
  OverrideMaxVal = 0
  WindowFrom = 80
  WindowTo = 100
  items = 5
FEATURE [Part::FeaturePython] Slice002_child6  label="right mesh"  # WARN: FeaturePython — macro-defined, semantics opaque (R4)
  Base = -> Slice002
  FilterType = 1
  Invert = false
  OverrideMaxVal = 0
  WindowFrom = 80
  WindowTo = 100
  items = 6
FEATURE [App::DocumentObjectGroup] GrExplode_Slice002  label="sliced lone front wall"
  Group = -> [Slice002_child0,Slice002_child1,Slice002_child2,Slice002_child3,Slice002_child4,Slice002_child5,Slice002_child6]
FEATURE [PartDesign::FeatureBase] BaseFeature002
  BaseFeature = -> Slice001_child0
  Suppressed = false
FEATURE [Sketcher::SketchObject] Sketch111
  ArcFitTolerance = 1e-06
  AttachmentSupport = -> [BaseFeature002]
  ExternalGeometry = -> [BaseFeature002]
  FullyConstrained = false
  MakeInternals = false
  MapMode = 5
  Placement = pos=(0,0,8) rot=(0,0,1;0rad)
  sketch-geometry (5):
    g0: LineSegment StartX=253.437 StartY=183.5 StartZ=0 EndX=124.9 EndY=183.5 EndZ=0
    g1: LineSegment StartX=124.9 StartY=183.5 StartZ=0 EndX=124.9 EndY=172.07 EndZ=0
    g2: LineSegment StartX=124.9 StartY=172.07 StartZ=0 EndX=-211 EndY=172.07 EndZ=0
    g3: LineSegment StartX=-211 StartY=172.07 StartZ=0 EndX=-211 EndY=183.5 EndZ=0
    g4: LineSegment StartX=-211 StartY=183.5 StartZ=0 EndX=-215 EndY=183.5 EndZ=0
  constraints (12):
    c: Horizontal(g0)
    c: Coincident(g0,g1)
    c: Coincident(g1,g2)
    c: Horizontal(g2)
    c: Coincident(g2,g3)
    c: Vertical(g3)
    c: Coincident(g-5,g0)
    c: Coincident(g-5,g1)
    c: PointOnObject(g-6,g3)
    c: PointOnObject(g3,g-7)
    c: Coincident(g4,g3)
    c: Coincident(g4,g-7)
FEATURE [PartDesign::Body] Body003  label="case without drive studs body"
  AllowCompound = false
  BaseFeature = -> Slice001_child0
  Group = -> [BaseFeature002,Sketch111]
  Origin = -> Origin003
  Tip = -> BaseFeature002
FEATURE [Part::Extrusion] Extrude004
  Base = -> Sketch111
  Dir = (0,0,1)
  DirMode = 2
  FaceMakerClass = Part::FaceMakerBullseye
  FaceMakerMode = 3
  LengthFwd = 180
  LengthRev = 10
  Solid = false
  Symmetric = false
FEATURE [Part::FeaturePython] Slice003  # WARN: FeaturePython — macro-defined, semantics opaque (R4)
  Base = -> BaseFeature002
  Mode = 1
  Tolerance = 0
  Tools = -> [Extrude004]
FEATURE [Part::FeaturePython] Slice003_child0  label="lone rear wall"  # WARN: FeaturePython — macro-defined, semantics opaque (R4)
  Base = -> Slice003
  FilterType = 1
  Invert = false
  OverrideMaxVal = 0
  WindowFrom = 80
  WindowTo = 100
  items = 0
FEATURE [Part::FeaturePython] Slice003_child1  label="sidewalls and bottom"  # WARN: FeaturePython — macro-defined, semantics opaque (R4)
  Base = -> Slice003
  FilterType = 1
  Invert = false
  OverrideMaxVal = 0
  WindowFrom = 80
  WindowTo = 100
  items = 1
FEATURE [App::DocumentObjectGroup] GrExplode_Slice003  label="Exploded Slice003"
  Group = -> [Slice003_child0,Slice003_child1]
FEATURE [PartDesign::FeatureBase] BaseFeature003
  BaseFeature = -> Slice003_child1
  Suppressed = false
FEATURE [Sketcher::SketchObject] Sketch112
  ArcFitTolerance = 1e-06
  AttachmentSupport = -> [BaseFeature003]
  ExternalGeometry = -> [BaseFeature003]
  FullyConstrained = false
  MakeInternals = false
  MapMode = 5
  Placement = pos=(0,0,8) rot=(0,0,1;0rad)
  sketch-geometry (3):
    g0: LineSegment StartX=-211 StartY=-214.137 StartZ=0 EndX=-211 EndY=251.042 EndZ=0
    g1: LineSegment StartX=-211 StartY=251.042 StartZ=0 EndX=211 EndY=251.042 EndZ=0
    g2: LineSegment StartX=211 StartY=251.042 StartZ=0 EndX=211 EndY=-240.237 EndZ=0
  constraints (7):
    c: Vertical(g0)
    c: Coincident(g0,g1)
    c: Horizontal(g1)
    c: Coincident(g1,g2)
    c: Vertical(g2)
    c: PointOnObject(g-3,g0)
    c: PointOnObject(g-4,g2)
FEATURE [PartDesign::Body] Body004  label="sidewalls and bottom body"
  AllowCompound = false
  BaseFeature = -> Slice003_child1
  Group = -> [BaseFeature003,Sketch112]
  Origin = -> Origin004
  Tip = -> BaseFeature003
FEATURE [Part::Extrusion] Extrude005
  Base = -> Sketch112
  Dir = (0,0,1)
  DirMode = 2
  FaceMakerClass = Part::FaceMakerBullseye
  FaceMakerMode = 3
  LengthFwd = 180
  LengthRev = 10
  Solid = false
  Symmetric = false
FEATURE [Part::FeaturePython] Slice004  # WARN: FeaturePython — macro-defined, semantics opaque (R4)
  Base = -> BaseFeature003
  Mode = 1
  Tolerance = 0
  Tools = -> [Extrude005]
FEATURE [Part::FeaturePython] Slice004_child0  label="left wall part"  # WARN: FeaturePython — macro-defined, semantics opaque (R4)
  Base = -> Slice004
  FilterType = 1
  Invert = false
  OverrideMaxVal = 0
  WindowFrom = 80
  WindowTo = 100
  items = 0
FEATURE [Part::FeaturePython] Slice004_child1  label="bottom part"  # WARN: FeaturePython — macro-defined, semantics opaque (R4)
  Base = -> Slice004
  FilterType = 1
  Invert = false
  OverrideMaxVal = 0
  WindowFrom = 80
  WindowTo = 100
  items = 1
FEATURE [Part::FeaturePython] Slice004_child2  label="front left support part"  # WARN: FeaturePython — macro-defined, semantics opaque (R4)
  Base = -> Slice004
  FilterType = 1
  Invert = false
  OverrideMaxVal = 0
  WindowFrom = 80
  WindowTo = 100
  items = 2
FEATURE [Part::FeaturePython] Slice004_child3  label="right wall part"  # WARN: FeaturePython — macro-defined, semantics opaque (R4)
  Base = -> Slice004
  FilterType = 1
  Invert = false
  OverrideMaxVal = 0
  WindowFrom = 80
  WindowTo = 100
  items = 3
FEATURE [App::DocumentObjectGroup] GrExplode_Slice004  label="Exploded Slice004"
  Group = -> [Slice004_child0,Slice004_child1,Slice004_child2,Slice004_child3]
FEATURE [PartDesign::FeatureBase] BaseFeature004
  BaseFeature = -> Slice004_child0
  Suppressed = false
FEATURE [PartDesign::FeatureBase] BaseFeature005
  BaseFeature = -> Slice004_child3
  Suppressed = false
FEATURE [Sketcher::SketchObject] Sketch113
  ArcFitTolerance = 1e-06
  AttachmentSupport = -> [BaseFeature004]
  ExternalGeometry = -> [BaseFeature004]
  FullyConstrained = false
  MakeInternals = false
  MapMode = 5
  Placement = pos=(-215,0,0) rot=(0.57735,-0.57735,-0.57735;2.0944rad)
  sketch-geometry (5):
    g0: GeomPoint [constr] X=6.5 Y=204.713 Z=0
    g1: GeomPoint [constr] X=6.5 Y=148 Z=0
    g2: LineSegment StartX=6.55 StartY=-13.2578 StartZ=0 EndX=6.55 EndY=204.713 EndZ=0
    g3: LineSegment StartX=6.55 StartY=204.713 StartZ=0 EndX=6.45 EndY=204.713 EndZ=0
    g4: LineSegment StartX=6.45 StartY=204.713 StartZ=0 EndX=6.45 EndY=-16.3521 EndZ=0
  constraints (9):
    c: Vertical(g0,g1)
    c: Symmetric(g-3,g-4,g1)
    c: Vertical(g2)
    c: Coincident(g2,g3)
    c: Horizontal(g3)
    c: Coincident(g3,g4)
    c: Vertical(g4)
    c: Symmetric(g2,g3,g0)
    c: DistanceX(g3,g3) = 0.1
FEATURE [PartDesign::Body] Body005  label="left wall body"
  AllowCompound = false
  BaseFeature = -> Slice004_child0
  Group = -> [BaseFeature004,Sketch113]
  Origin = -> Origin005
  Tip = -> BaseFeature004
FEATURE [Sketcher::SketchObject] Sketch114
  ArcFitTolerance = 1e-06
  AttachmentSupport = -> [BaseFeature005]
  ExternalGeometry = -> [BaseFeature005]
  FullyConstrained = false
  MakeInternals = false
  MapMode = 5
  Placement = pos=(215,0,0) rot=(0.57735,0.57735,0.57735;2.0944rad)
  sketch-geometry (5):
    g0: LineSegment StartX=-6.55 StartY=-19.1566 StartZ=0 EndX=-6.55 EndY=209.515 EndZ=0
    g1: LineSegment StartX=-6.55 StartY=209.515 StartZ=0 EndX=-6.45 EndY=209.515 EndZ=0
    g2: LineSegment StartX=-6.45 StartY=209.515 StartZ=0 EndX=-6.45 EndY=-29.1245 EndZ=0
    g3: GeomPoint [constr] X=-6.5 Y=148 Z=0
    g4: GeomPoint [constr] X=-6.5 Y=209.515 Z=0
  constraints (9):
    c: Vertical(g0)
    c: Coincident(g0,g1)
    c: Horizontal(g1)
    c: Coincident(g1,g2)
    c: Vertical(g2)
    c: Vertical(g4,g3)
    c: Symmetric(g-3,g-4,g3)
    c: Symmetric(g1,g0,g4)
    c: DistanceX(g1,g1) = 0.1
FEATURE [PartDesign::Body] Body006  label="right wall body"
  AllowCompound = false
  BaseFeature = -> Slice004_child3
  Group = -> [BaseFeature005,Sketch114]
  Origin = -> Origin006
  Tip = -> BaseFeature005
FEATURE [Part::Extrusion] Extrude006
  Base = -> Sketch114
  Dir = (1,0,0)
  DirMode = 2
  FaceMakerClass = Part::FaceMakerBullseye
  FaceMakerMode = 3
  LengthFwd = 10
  LengthRev = 10
  Solid = false
  Symmetric = false
FEATURE [Part::FeaturePython] Slice005  # WARN: FeaturePython — macro-defined, semantics opaque (R4)
  Base = -> BaseFeature005
  Mode = 1
  Tolerance = 0
  Tools = -> [Extrude006]
FEATURE [Part::FeaturePython] Slice005_child0  label="right wall - front"  # WARN: FeaturePython — macro-defined, semantics opaque (R4)
  Base = -> Slice005
  FilterType = 1
  Invert = false
  OverrideMaxVal = 0
  WindowFrom = 80
  WindowTo = 100
  items = 0
FEATURE [Part::FeaturePython] Slice005_child1  label="Slice005.1"  # WARN: FeaturePython — macro-defined, semantics opaque (R4)
  Base = -> Slice005
  FilterType = 1
  Invert = false
  OverrideMaxVal = 0
  WindowFrom = 80
  WindowTo = 100
  items = 1
FEATURE [Part::FeaturePython] Slice005_child2  label="right wall - rear"  # WARN: FeaturePython — macro-defined, semantics opaque (R4)
  Base = -> Slice005
  FilterType = 1
  Invert = false
  OverrideMaxVal = 0
  WindowFrom = 80
  WindowTo = 100
  items = 2
FEATURE [App::DocumentObjectGroup] GrExplode_Slice005  label="Exploded Slice005"
  Group = -> [Slice005_child0,Slice005_child1,Slice005_child2]
FEATURE [Part::Extrusion] Extrude007
  Base = -> Sketch113
  Dir = (-1,0,0)
  DirMode = 2
  FaceMakerClass = Part::FaceMakerBullseye
  FaceMakerMode = 3
  LengthFwd = 10
  LengthRev = 10
  Solid = false
  Symmetric = false
FEATURE [Part::FeaturePython] Slice006  # WARN: FeaturePython — macro-defined, semantics opaque (R4)
  Base = -> BaseFeature004
  Mode = 1
  Tolerance = 0
  Tools = -> [Extrude007]
FEATURE [Part::FeaturePython] Slice006_child0  label="left wall - rear"  # WARN: FeaturePython — macro-defined, semantics opaque (R4)
  Base = -> Slice006
  FilterType = 1
  Invert = false
  OverrideMaxVal = 0
  WindowFrom = 80
  WindowTo = 100
  items = 0
FEATURE [Part::FeaturePython] Slice006_child1  label="Slice006.1"  # WARN: FeaturePython — macro-defined, semantics opaque (R4)
  Base = -> Slice006
  FilterType = 1
  Invert = false
  OverrideMaxVal = 0
  WindowFrom = 80
  WindowTo = 100
  items = 1
FEATURE [Part::FeaturePython] Slice006_child2  label="left wall - front"  # WARN: FeaturePython — macro-defined, semantics opaque (R4)
  Base = -> Slice006
  FilterType = 1
  Invert = false
  OverrideMaxVal = 0
  WindowFrom = 80
  WindowTo = 100
  items = 2
FEATURE [App::DocumentObjectGroup] GrExplode_Slice006  label="Exploded Slice006"
  Group = -> [Slice006_child0,Slice006_child1,Slice006_child2]
FEATURE [PartDesign::FeatureBase] BaseFeature006
  BaseFeature = -> Slice004_child1
  Suppressed = false
FEATURE [Sketcher::SketchObject] Sketch115
  ArcFitTolerance = 1e-06
  AttachmentSupport = -> [BaseFeature006]
  ExternalGeometry = -> [BaseFeature006]
  FullyConstrained = false
  MakeInternals = false
  MapMode = 5
  Placement = pos=(0,0,0) rot=(1,0,0;3.14159rad)
  sketch-geometry (31):
    g0: GeomPoint [constr] X=-9.254e-13 Y=6.6 Z=0
    g1: LineSegment StartX=-210.9 StartY=6.65 StartZ=0 EndX=-2.425 EndY=6.65 EndZ=0
    g2: LineSegment StartX=210.9 StartY=6.55 StartZ=0 EndX=0.05 EndY=6.55 EndZ=0
    g3: LineSegment StartX=0.05 StartY=6.55 StartZ=0 EndX=0.05 EndY=-331.414 EndZ=0
    g4: LineSegment StartX=0.05 StartY=-331.414 StartZ=0 EndX=-0.05 EndY=-331.414 EndZ=0
    g5: LineSegment StartX=-0.05 StartY=-331.414 StartZ=0 EndX=-0.05 EndY=6.55 EndZ=0
    g6: GeomPoint [constr] X=-9.254e-13 Y=-331.414 Z=0
    g7: GeomPoint [constr] X=-1.2 Y=78.43 Z=0
    g8: LineSegment StartX=-2.425 StartY=77.03 StartZ=0 EndX=-2.425 EndY=180.9 EndZ=0
    g9: LineSegment StartX=-2.525 StartY=180.9 StartZ=0 EndX=-2.525 EndY=76.93 EndZ=0
    g10: LineSegment StartX=182.7 StartY=203.534 StartZ=0 EndX=182.7 EndY=181.05 EndZ=0
    g11: LineSegment StartX=182.7 StartY=181.05 StartZ=0 EndX=-151.1 EndY=181.05 EndZ=0
    g12: LineSegment StartX=-151.1 StartY=181.05 StartZ=0 EndX=-151.1 EndY=204.03 EndZ=0
    g13: LineSegment StartX=182.9 StartY=203.261 StartZ=0 EndX=182.9 EndY=180.9 EndZ=0
    g14: LineSegment StartX=-2.525 StartY=180.9 StartZ=0 EndX=-151.3 EndY=180.9 EndZ=0
    g15: LineSegment StartX=-151.3 StartY=180.9 StartZ=0 EndX=-151.3 EndY=204.698 EndZ=0
    g16: GeomPoint [constr] X=1.6 Y=180.95 Z=0
    g17: LineSegment StartX=-2.425 StartY=6.65 StartZ=0 EndX=-0.05 EndY=6.65 EndZ=0
    g18: LineSegment StartX=182.9 StartY=180.9 StartZ=0 EndX=-2.425 EndY=180.9 EndZ=0
    g19: LineSegment StartX=-210.9 StartY=6.65 StartZ=0 EndX=-210.9 EndY=245.398 EndZ=0
    g20: LineSegment StartX=-210.9 StartY=6.55 StartZ=0 EndX=-210.9 EndY=-214.931 EndZ=0
    g21: GeomPoint [constr] X=211 Y=6.6 Z=0
    g22: LineSegment StartX=210.9 StartY=191.916 StartZ=0 EndX=210.9 EndY=6.65 EndZ=0
    g23: LineSegment StartX=210.9 StartY=6.55 StartZ=0 EndX=210.9 EndY=-191.143 EndZ=0
    g24: GeomPoint [constr] X=210.9 Y=6.6 Z=0
    g25: LineSegment StartX=-0.05 StartY=6.55 StartZ=0 EndX=-210.9 EndY=6.55 EndZ=0
    g26: LineSegment StartX=0.05 StartY=6.65 StartZ=0 EndX=0.05 EndY=77.03 EndZ=0
    g27: LineSegment StartX=0.05 StartY=77.03 StartZ=0 EndX=-2.425 EndY=77.03 EndZ=0
    g28: LineSegment StartX=-0.05 StartY=6.65 StartZ=0 EndX=-0.05 EndY=76.93 EndZ=0
    g29: LineSegment StartX=-0.05 StartY=76.93 StartZ=0 EndX=-2.525 EndY=76.93 EndZ=0
    g30: LineSegment StartX=0.05 StartY=6.65 StartZ=0 EndX=210.9 EndY=6.65 EndZ=0
  constraints (78):
    c: Symmetric(g-4,g-3,g0)
    c: Horizontal(g1)
    c: Horizontal(g2)
    c: DistanceY(g2,g30) = 0.1
    c: Vertical(g3)
    c: Coincident(g3,g4)
    c: Coincident(g4,g5)
    c: Vertical(g5)
    c: Horizontal(g4)
    c: Symmetric(g4,g4,g6)
    c: Vertical(g6,g0)
    c: DistanceX(g4,g4) = 0.1
    c: Symmetric(g-5,g-6,g7)
    c: Vertical(g8)
    c: Vertical(g9)
    c: Vertical(g10)
    c: Coincident(g10,g11)
    c: Horizontal(g11)
    c: Coincident(g11,g12)
    c: Vertical(g12)
    c: Distance(g-10,g12) = 1.5
    c: Distance(g-9,g10) = 1.5
    c: Horizontal(g14)
    c: Coincident(g14,g15)
    c: Vertical(g15)
    c: Vertical(g13)
    c: DistanceX(g10,g13) = 0.2
    c: DistanceX(g15,g12) = 0.2
    c: DistanceY(g14,g11) = 0.15
    c: Symmetric(g-7,g-8,g16)
    c: Distance(g16,g11) = 0.1
    c: Coincident(g2,g3)
    c: Horizontal(g2,g5)
    c: PointOnObject(g17,g8)
    c: Horizontal(g17)
    c: Coincident(g14,g9)
    c: Coincident(g18,g13)
    c: Coincident(g18,g8)
    c: Horizontal(g18)
    c: Horizontal(g8,g9)
    c: Vertical(g19)
    c: Vertical(g20)
    c: Coincident(g1,g19)
    c: Vertical(g1,g20)
    c: Distance(g-11,g19) = 0.1
    c: PointOnObject(g21,g-12)
    c: Horizontal(g21,g0)
    c: Vertical(g22)
    c: Vertical(g23)
    c: Vertical(g22,g23)
    c: Coincident(g30,g22)
    c: Coincident(g2,g23)
    c: Horizontal(g21,g24)
    c: Distance(g21,g24) = 0.1
    c: Symmetric(g30,g2,g24)
    c: Coincident(g25,g5)
    c: Coincident(g25,g20)
    c: Horizontal(g25)
    c: PointOnObject(g26,g30)
    c: Coincident(g26,g27)
    c: Horizontal(g27)
    c: Vertical(g28)
    c: Coincident(g28,g29)
    c: Horizontal(g29)
    c: Vertical(g26)
    c: Vertical(g26,g2)
    c: Vertical(g28,g5)
    c: Coincident(g17,g28)
    c: PointOnObject(g30,g26)
    c: DistanceY(g2,g26) = 0.1
    c: DistanceY(g5,g17) = 0.1
    c: DistanceX(g9,g8) = 0.1
    c: DistanceX(g8,g-13) = 1
    c: DistanceY(g28,g26) = 0.1
    c: Coincident(g8,g27)
    c: Coincident(g9,g29)
    c: DistanceY(g-6,g9) = 2.5
    c: Coincident(g17,g1)
FEATURE [PartDesign::Body] Body007  label="bottom part body"
  AllowCompound = false
  BaseFeature = -> Slice004_child1
  Group = -> [BaseFeature006,Sketch115]
  Origin = -> Origin007
  Tip = -> BaseFeature006
FEATURE [Part::Extrusion] Extrude008
  Base = -> Sketch115
  Dir = (0,0,-1)
  DirMode = 2
  FaceMakerClass = Part::FaceMakerBullseye
  FaceMakerMode = 3
  LengthFwd = 10
  LengthRev = 10
  Solid = false
  Symmetric = false
FEATURE [Part::FeaturePython] Slice007  # WARN: FeaturePython — macro-defined, semantics opaque (R4)
  Base = -> BaseFeature006
  Mode = 1
  Tolerance = 0
  Tools = -> [Extrude008]
FEATURE [Part::FeaturePython] Slice007_child0  label="Slice007.0"  # WARN: FeaturePython — macro-defined, semantics opaque (R4)
  Base = -> Slice007
  FilterType = 1
  Invert = false
  OverrideMaxVal = 0
  WindowFrom = 80
  WindowTo = 100
  items = 0
FEATURE [Part::FeaturePython] Slice007_child1  label="middle left"  # WARN: FeaturePython — macro-defined, semantics opaque (R4)
  Base = -> Slice007
  FilterType = 1
  Invert = false
  OverrideMaxVal = 0
  WindowFrom = 80
  WindowTo = 100
  items = 1
FEATURE [Part::FeaturePython] Slice007_child2  label="rear left"  # WARN: FeaturePython — macro-defined, semantics opaque (R4)
  Base = -> Slice007
  FilterType = 1
  Invert = false
  OverrideMaxVal = 0
  WindowFrom = 80
  WindowTo = 100
  items = 2
FEATURE [Part::FeaturePython] Slice007_child3  label="front"  # WARN: FeaturePython — macro-defined, semantics opaque (R4)
  Base = -> Slice007
  FilterType = 1
  Invert = false
  OverrideMaxVal = 0
  WindowFrom = 80
  WindowTo = 100
  items = 3
FEATURE [Part::FeaturePython] Slice007_child4  label="middle right"  # WARN: FeaturePython — macro-defined, semantics opaque (R4)
  Base = -> Slice007
  FilterType = 1
  Invert = false
  OverrideMaxVal = 0
  WindowFrom = 80
  WindowTo = 100
  items = 4
FEATURE [Part::FeaturePython] Slice007_child5  label="rear right"  # WARN: FeaturePython — macro-defined, semantics opaque (R4)
  Base = -> Slice007
  FilterType = 1
  Invert = false
  OverrideMaxVal = 0
  WindowFrom = 80
  WindowTo = 100
  items = 5
FEATURE [App::DocumentObjectGroup] GrExplode_Slice007  label="Exploded Slice007"
  Group = -> [Slice007_child0,Slice007_child1,Slice007_child2,Slice007_child3,Slice007_child4,Slice007_child5]
FEATURE [PartDesign::FeatureBase] BaseFeature007
  BaseFeature = -> Slice007_child1
  Suppressed = false
FEATURE [PartDesign::FeatureBase] BaseFeature008
  BaseFeature = -> Slice007_child4
  Suppressed = false
FEATURE [Sketcher::SketchObject] Sketch116
  ArcFitTolerance = 1e-06
  AttachmentSupport = -> [BaseFeature008]
  ExternalGeometry = -> [BaseFeature008]
  FullyConstrained = true
  MakeInternals = false
  MapMode = 5
  Placement = pos=(0,0,0) rot=(1,0,0;3.14159rad)
  sketch-geometry (12):
    g0: LineSegment StartX=-2.425 StartY=133.6 StartZ=0 EndX=80.3 EndY=133.6 EndZ=0
    g1: LineSegment StartX=80.3 StartY=133.6 StartZ=0 EndX=80.3 EndY=139.6 EndZ=0
    g2: LineSegment StartX=80.3 StartY=139.6 StartZ=0 EndX=86.3 EndY=139.6 EndZ=0
    g3: LineSegment StartX=86.3 StartY=139.6 StartZ=0 EndX=86.3 EndY=133.6 EndZ=0
    g4: LineSegment StartX=86.3 StartY=133.6 StartZ=0 EndX=195 EndY=133.6 EndZ=0
    g5: LineSegment StartX=195 StartY=133.6 StartZ=0 EndX=195 EndY=105.6 EndZ=0
    g6: LineSegment StartX=195 StartY=105.6 StartZ=0 EndX=205 EndY=105.6 EndZ=0
    g7: LineSegment StartX=205 StartY=105.6 StartZ=0 EndX=205 EndY=99.6 EndZ=0
    g8: LineSegment StartX=205 StartY=99.6 StartZ=0 EndX=195 EndY=99.6 EndZ=0
    g9: LineSegment StartX=195 StartY=99.6 StartZ=0 EndX=195 EndY=87.93 EndZ=0
    g10: LineSegment StartX=195 StartY=87.93 StartZ=0 EndX=-2.425 EndY=87.93 EndZ=0
    g11: LineSegment StartX=-2.425 StartY=87.93 StartZ=0 EndX=-2.425 EndY=133.6 EndZ=0
  constraints (36):
    c: Horizontal(g0)
    c: Coincident(g0,g1)
    c: Vertical(g1)
    c: Coincident(g1,g2)
    c: Horizontal(g2)
    c: Coincident(g2,g3)
    c: Coincident(g3,g4)
    c: Horizontal(g4)
    c: Coincident(g4,g5)
    c: Vertical(g5)
    c: Coincident(g5,g6)
    c: Coincident(g6,g7)
    c: Coincident(g7,g8)
    c: Coincident(g8,g9)
    c: Coincident(g9,g10)
    c: Horizontal(g10)
    c: Coincident(g10,g11)
    c: Coincident(g0,g11)
    c: Vertical(g11)
    c: Vertical(g3)
    c: Vertical(g9)
    c: Vertical(g7)
    c: Horizontal(g6)
    c: Horizontal(g8)
    c: Vertical(g5,g8)
    c: Horizontal(g3,g0)
    c: PointOnObject(g-4,g11)
    c: DistanceY(g-4,g0) = 1
    c: DistanceY(g10,g-3) = 1
    c: DistanceX(g5,g-7) = 2
    c: DistanceY(g-6,g6) = 3
    c: DistanceY(g7,g-6) = 3
    c: DistanceX(g-6,g7) = 3
    c: DistanceX(g-5,g2) = 3
    c: DistanceX(g1,g-5) = 3
    c: DistanceY(g-5,g2) = 3
FEATURE [PartDesign::Pocket] Pocket039
  BaseFeature = -> BaseFeature008
  Direction = (0,0,1)
  Length = 2
  Length2 = 5
  Profile = -> Sketch116
  ReferenceAxis = -> Sketch116 [N_Axis]
  Refine = true
  Suppressed = false
  Type = 0
FEATURE [PartDesign::Body] Body009  label="middle right body"
  AllowCompound = false
  BaseFeature = -> Slice007_child4
  Group = -> [BaseFeature008,Sketch116,Pocket039]
  Origin = -> Origin009
  Tip = -> Pocket039
FEATURE [Sketcher::SketchObject] Sketch117
  ArcFitTolerance = 1e-06
  AttachmentSupport = -> [BaseFeature007]
  ExternalGeometry = -> [BaseFeature007]
  FullyConstrained = true
  MakeInternals = false
  MapMode = 5
  Placement = pos=(0,0,0) rot=(1,0,0;3.14159rad)
  sketch-geometry (12):
    g0: LineSegment StartX=-2.525 StartY=133.6 StartZ=0 EndX=-47.9 EndY=133.6 EndZ=0
    g1: LineSegment StartX=-47.9 StartY=133.6 StartZ=0 EndX=-47.9 EndY=139.6 EndZ=0
    g2: LineSegment StartX=-47.9 StartY=139.6 StartZ=0 EndX=-53.9 EndY=139.6 EndZ=0
    g3: LineSegment StartX=-53.9 StartY=139.6 StartZ=0 EndX=-53.9 EndY=133.6 EndZ=0
    g4: LineSegment StartX=-53.9 StartY=133.6 StartZ=0 EndX=-195 EndY=133.6 EndZ=0
    g5: LineSegment StartX=-195 StartY=133.6 StartZ=0 EndX=-195 EndY=105.6 EndZ=0
    g6: LineSegment StartX=-195 StartY=105.6 StartZ=0 EndX=-205 EndY=105.6 EndZ=0
    g7: LineSegment StartX=-205 StartY=105.6 StartZ=0 EndX=-205 EndY=99.6 EndZ=0
    g8: LineSegment StartX=-205 StartY=99.6 StartZ=0 EndX=-195 EndY=99.6 EndZ=0
    g9: LineSegment StartX=-195 StartY=99.6 StartZ=0 EndX=-195 EndY=87.93 EndZ=0
    g10: LineSegment StartX=-195 StartY=87.93 StartZ=0 EndX=-2.525 EndY=87.93 EndZ=0
    g11: LineSegment StartX=-2.525 StartY=87.93 StartZ=0 EndX=-2.525 EndY=133.6 EndZ=0
  constraints (36):
    c: Horizontal(g0)
    c: Coincident(g0,g1)
    c: Coincident(g1,g2)
    c: Horizontal(g2)
    c: Coincident(g2,g3)
    c: Coincident(g3,g4)
    c: Horizontal(g4)
    c: Coincident(g4,g5)
    c: Coincident(g5,g6)
    c: Coincident(g6,g7)
    c: Coincident(g7,g8)
    c: Coincident(g8,g9)
    c: Coincident(g9,g10)
    c: Horizontal(g10)
    c: Coincident(g10,g11)
    c: Coincident(g11,g0)
    c: Horizontal(g8)
    c: Horizontal(g6)
    c: Vertical(g7)
    c: Vertical(g9)
    c: Vertical(g5)
    c: Vertical(g3)
    c: Vertical(g1)
    c: Vertical(g11)
    c: PointOnObject(g-4,g11)
    c: Horizontal(g0,g3)
    c: Vertical(g5,g8)
    c: DistanceY(g-4,g4) = 1
    c: DistanceY(g9,g-3) = 1
    c: DistanceY(g-7,g1) = 3
    c: DistanceX(g-7,g1) = 3
    c: DistanceX(g2,g-7) = 3
    c: DistanceY(g-6,g6) = 3
    c: DistanceY(g7,g-6) = 3
    c: DistanceX(g7,g-6) = 3
    c: DistanceX(g-5,g5) = 2
FEATURE [PartDesign::Pocket] Pocket040
  BaseFeature = -> BaseFeature007
  Direction = (0,0,1)
  Length = 2
  Length2 = 5
  Profile = -> Sketch117
  ReferenceAxis = -> Sketch117 [N_Axis]
  Refine = true
  Suppressed = false
  Type = 0
FEATURE [PartDesign::Body] Body008  label="middle left body"
  AllowCompound = false
  BaseFeature = -> Slice007_child1
  Group = -> [BaseFeature007,Sketch117,Pocket040]
  Origin = -> Origin008
  Tip = -> Pocket040
FEATURE [PartDesign::FeatureBase] BaseFeature009
  BaseFeature = -> Slice007_child4
  Suppressed = false
FEATURE [Sketcher::SketchObject] Sketch118
  ArcFitTolerance = 1e-06
  AttachmentSupport = -> [BaseFeature009]
  ExternalGeometry = -> [BaseFeature009]
  FullyConstrained = true
  MakeInternals = false
  MapMode = 5
  Placement = pos=(0,0,0) rot=(1,0,0;3.14159rad)
  sketch-geometry (20):
    g0: LineSegment StartX=210.9 StartY=184.5 StartZ=0 EndX=182.9 EndY=184.5 EndZ=0
    g1: LineSegment StartX=182.9 StartY=184.5 StartZ=0 EndX=182.9 EndY=180.9 EndZ=0
    g2: LineSegment StartX=182.9 StartY=180.9 StartZ=0 EndX=-2.425 EndY=180.9 EndZ=0
    g3: LineSegment StartX=-2.425 StartY=180.9 StartZ=0 EndX=-2.425 EndY=133.5 EndZ=0
    g4: LineSegment StartX=-2.425 StartY=133.5 StartZ=0 EndX=80.4 EndY=133.5 EndZ=0
    g5: LineSegment StartX=80.4 StartY=133.5 StartZ=0 EndX=80.4 EndY=139.5 EndZ=0
    g6: LineSegment StartX=80.4 StartY=139.5 StartZ=0 EndX=86.2 EndY=139.5 EndZ=0
    g7: LineSegment StartX=86.2 StartY=139.5 StartZ=0 EndX=86.2 EndY=133.5 EndZ=0
    g8: LineSegment StartX=86.2 StartY=133.5 StartZ=0 EndX=194.9 EndY=133.5 EndZ=0
    g9: LineSegment StartX=194.9 StartY=133.5 StartZ=0 EndX=194.9 EndY=105.5 EndZ=0
    g10: LineSegment StartX=194.9 StartY=105.5 StartZ=0 EndX=204.9 EndY=105.5 EndZ=0
    g11: LineSegment StartX=204.9 StartY=105.5 StartZ=0 EndX=204.9 EndY=99.7 EndZ=0
    g12: LineSegment StartX=204.9 StartY=99.7 StartZ=0 EndX=194.9 EndY=99.7 EndZ=0
    g13: LineSegment StartX=194.9 StartY=99.7 StartZ=0 EndX=194.9 EndY=88.03 EndZ=0
    g14: LineSegment StartX=194.9 StartY=88.03 StartZ=0 EndX=-2.425 EndY=88.03 EndZ=0
    g15: LineSegment StartX=0.05 StartY=77.03 StartZ=0 EndX=0.05 EndY=6.65 EndZ=0
    g16: LineSegment StartX=0.05 StartY=6.65 StartZ=0 EndX=210.9 EndY=6.65 EndZ=0
    g17: LineSegment StartX=210.9 StartY=6.65 StartZ=0 EndX=210.9 EndY=184.5 EndZ=0
    g18: LineSegment StartX=0.05 StartY=77.03 StartZ=0 EndX=-2.425 EndY=77.03 EndZ=0
    g19: LineSegment StartX=-2.425 StartY=77.03 StartZ=0 EndX=-2.425 EndY=88.03 EndZ=0
  constraints (54):
    c: Horizontal(g0)
    c: Coincident(g0,g1)
    c: Vertical(g1)
    c: Coincident(g1,g2)
    c: Coincident(g2,g3)
    c: Coincident(g3,g4)
    c: Horizontal(g4)
    c: Coincident(g4,g5)
    c: Coincident(g5,g6)
    c: Horizontal(g6)
    c: Coincident(g6,g7)
    c: Coincident(g7,g8)
    c: Horizontal(g8)
    c: Coincident(g8,g9)
    c: Vertical(g9)
    c: Coincident(g9,g10)
    c: Horizontal(g10)
    c: Coincident(g10,g11)
    c: Vertical(g11)
    c: Coincident(g11,g12)
    c: Coincident(g12,g13)
    c: Coincident(g13,g14)
    c: Horizontal(g14)
    c: Coincident(g15,g16)
    c: Horizontal(g16)
    c: Coincident(g16,g17)
    c: Coincident(g17,g0)
    c: Vertical(g3)
    c: Horizontal(g12)
    c: Vertical(g13)
    c: Coincident(g-7,g1)
    c: Coincident(g0,g-8)
    c: Coincident(g16,g-8)
    c: Vertical(g15)
    c: Coincident(g15,g18)
    c: Coincident(g18,g19)
    c: Coincident(g19,g14)
    c: Vertical(g19)
    c: Coincident(g15,g-9)
    c: Coincident(g-9,g18)
    c: DistanceY(g14,g-5) = 0.9
    c: DistanceY(g-6,g3) = 0.9
    c: Coincident(g-7,g2)
    c: Vertical(g7)
    c: Vertical(g5)
    c: Horizontal(g7,g4)
    c: DistanceX(g-3,g6) = 2.9
    c: DistanceX(g5,g-3) = 2.9
    c: DistanceY(g-3,g5) = 2.9
    c: DistanceY(g-4,g10) = 2.9
    c: DistanceY(g11,g-4) = 2.9
    c: DistanceX(g-4,g11) = 2.9
    c: DistanceX(g8,g-10) = 2.1
    c: Vertical(g12,g9)
FEATURE [PartDesign::Pocket] Pocket041
  BaseFeature = -> BaseFeature009
  Direction = (0,0,1)
  Length = 8
  Length2 = 5
  Profile = -> Sketch118
  ReferenceAxis = -> Sketch118 [N_Axis]
  Refine = true
  Suppressed = false
  Type = 0
FEATURE [Sketcher::SketchObject] Sketch119
  ArcFitTolerance = 1e-06
  AttachmentSupport = -> [Pocket041]
  ExternalGeometry = -> [Pocket041]
  FullyConstrained = true
  MakeInternals = false
  MapMode = 5
  Placement = pos=(0,-88.03,0) rot=(0,0.707107,0.707107;3.14159rad)
  sketch-geometry (4):
    g0: LineSegment StartX=-204.9 StartY=8 StartZ=0 EndX=-204.9 EndY=1.9 EndZ=0
    g1: LineSegment StartX=-204.9 StartY=1.9 StartZ=0 EndX=2.425 EndY=1.9 EndZ=0
    g2: LineSegment StartX=2.425 StartY=1.9 StartZ=0 EndX=2.425 EndY=8 EndZ=0
    g3: LineSegment StartX=2.425 StartY=8 StartZ=0 EndX=-204.9 EndY=8 EndZ=0
  constraints (10):
    c: Coincident(g0,g1)
    c: Coincident(g1,g2)
    c: Coincident(g2,g3)
    c: Coincident(g3,g0)
    c: Vertical(g0)
    c: Vertical(g2)
    c: Horizontal(g1)
    c: Coincident(g0,g-4)
    c: Coincident(g-3,g2)
    c: DistanceY(g-5,g0) = 1.9
FEATURE [PartDesign::Pocket] Pocket042
  BaseFeature = -> Pocket041
  Direction = (0,-1,2e-16)
  Length = 5
  Length2 = 5
  Profile = -> Sketch119
  ReferenceAxis = -> Sketch119 [N_Axis]
  Refine = true
  Suppressed = false
  Type = 1
FEATURE [PartDesign::Body] Body011  label="right bottom plate body"
  AllowCompound = false
  BaseFeature = -> Slice007_child4
  Group = -> [BaseFeature009,Sketch118,Pocket041,Sketch119,Pocket042]
  Origin = -> Origin011
  Tip = -> Pocket042
FEATURE [PartDesign::FeatureBase] BaseFeature010
  BaseFeature = -> Slice007_child1
  Suppressed = false
FEATURE [Sketcher::SketchObject] Sketch120
  ArcFitTolerance = 1e-06
  AttachmentSupport = -> [BaseFeature010]
  ExternalGeometry = -> [BaseFeature010]
  FullyConstrained = true
  MakeInternals = false
  MapMode = 5
  Placement = pos=(0,0,0) rot=(1,0,0;3.14159rad)
  sketch-geometry (20):
    g0: LineSegment StartX=-2.525 StartY=180.9 StartZ=0 EndX=-151.3 EndY=180.9 EndZ=0
    g1: LineSegment StartX=-151.3 StartY=180.9 StartZ=0 EndX=-151.3 EndY=184.5 EndZ=0
    g2: LineSegment StartX=-151.3 StartY=184.5 StartZ=0 EndX=-210.9 EndY=184.5 EndZ=0
    g3: LineSegment StartX=-210.9 StartY=184.5 StartZ=0 EndX=-210.9 EndY=6.65 EndZ=0
    g4: LineSegment StartX=-210.9 StartY=6.65 StartZ=0 EndX=-0.05 EndY=6.65 EndZ=0
    g5: LineSegment StartX=-0.05 StartY=6.65 StartZ=0 EndX=-0.05 EndY=76.93 EndZ=0
    g6: LineSegment StartX=-0.05 StartY=76.93 StartZ=0 EndX=-2.525 EndY=76.93 EndZ=0
    g7: LineSegment StartX=-2.525 StartY=76.93 StartZ=0 EndX=-2.525 EndY=88.03 EndZ=0
    g8: LineSegment StartX=-2.525 StartY=180.9 StartZ=0 EndX=-2.525 EndY=133.5 EndZ=0
    g9: LineSegment StartX=-2.525 StartY=133.5 StartZ=0 EndX=-48 EndY=133.5 EndZ=0
    g10: LineSegment StartX=-48 StartY=133.5 StartZ=0 EndX=-48 EndY=139.5 EndZ=0
    g11: LineSegment StartX=-48 StartY=139.5 StartZ=0 EndX=-53.8 EndY=139.5 EndZ=0
    g12: LineSegment StartX=-53.8 StartY=139.5 StartZ=0 EndX=-53.8 EndY=133.5 EndZ=0
    g13: LineSegment StartX=-53.8 StartY=133.5 StartZ=0 EndX=-194.9 EndY=133.5 EndZ=0
    g14: LineSegment StartX=-194.9 StartY=133.5 StartZ=0 EndX=-194.9 EndY=105.5 EndZ=0
    g15: LineSegment StartX=-194.9 StartY=105.5 StartZ=0 EndX=-204.9 EndY=105.5 EndZ=0
    g16: LineSegment StartX=-204.9 StartY=105.5 StartZ=0 EndX=-204.9 EndY=99.7 EndZ=0
    g17: LineSegment StartX=-204.9 StartY=99.7 StartZ=0 EndX=-194.9 EndY=99.7 EndZ=0
    g18: LineSegment StartX=-194.9 StartY=99.7 StartZ=0 EndX=-194.9 EndY=88.03 EndZ=0
    g19: LineSegment StartX=-194.9 StartY=88.03 StartZ=0 EndX=-2.525 EndY=88.03 EndZ=0
  constraints (53):
    c: Coincident(g0,g1)
    c: Coincident(g1,g2)
    c: Coincident(g2,g3)
    c: Vertical(g3)
    c: Coincident(g3,g4)
    c: Horizontal(g4)
    c: Coincident(g4,g5)
    c: Coincident(g5,g6)
    c: Coincident(g6,g7)
    c: Vertical(g7)
    c: Coincident(g4,g-5)
    c: Coincident(g2,g-4)
    c: Coincident(g1,g-4)
    c: Coincident(g0,g-3)
    c: Coincident(g0,g-3)
    c: Coincident(g0,g8)
    c: Coincident(g8,g9)
    c: Horizontal(g9)
    c: Coincident(g9,g10)
    c: Coincident(g10,g11)
    c: Coincident(g11,g12)
    c: Coincident(g12,g13)
    c: Horizontal(g13)
    c: Coincident(g13,g14)
    c: Vertical(g14)
    c: Coincident(g14,g15)
    c: Coincident(g15,g16)
    c: Coincident(g16,g17)
    c: Horizontal(g17)
    c: Coincident(g17,g18)
    c: Coincident(g18,g19)
    c: Coincident(g19,g7)
    c: Horizontal(g19)
    c: Vertical(g8)
    c: DistanceY(g-11,g8) = 0.9
    c: Horizontal(g11)
    c: Vertical(g10)
    c: Vertical(g12)
    c: Horizontal(g12,g9)
    c: DistanceX(g-9,g10) = 2.9
    c: DistanceX(g11,g-9) = 2.9
    c: DistanceY(g-9,g10) = 2.9
    c: Vertical(g16)
    c: Horizontal(g15)
    c: Vertical(g18)
    c: Vertical(g14,g17)
    c: DistanceY(g-8,g15) = 2.9
    c: DistanceY(g16,g-8) = 2.9
    c: DistanceX(g16,g-8) = 2.9
    c: DistanceY(g18,g-10) = 0.9
    c: DistanceX(g-7,g13) = 2.1
    c: Coincident(g-6,g5)
    c: Coincident(g-6,g6)
FEATURE [PartDesign::Pocket] Pocket043
  BaseFeature = -> BaseFeature010
  Direction = (0,0,1)
  Length = 8
  Length2 = 5
  Profile = -> Sketch120
  ReferenceAxis = -> Sketch120 [N_Axis]
  Refine = true
  Suppressed = false
  Type = 0
FEATURE [Sketcher::SketchObject] Sketch121
  ArcFitTolerance = 1e-06
  AttachmentSupport = -> [Pocket043]
  ExternalGeometry = -> [Pocket043]
  FullyConstrained = true
  MakeInternals = false
  MapMode = 5
  Placement = pos=(0,-88.03,0) rot=(0,0.707107,0.707107;3.14159rad)
  sketch-geometry (4):
    g0: LineSegment StartX=2.525 StartY=8 StartZ=0 EndX=2.525 EndY=1.9 EndZ=0
    g1: LineSegment StartX=2.525 StartY=1.9 StartZ=0 EndX=204.9 EndY=1.9 EndZ=0
    g2: LineSegment StartX=204.9 StartY=1.9 StartZ=0 EndX=204.9 EndY=8 EndZ=0
    g3: LineSegment StartX=204.9 StartY=8 StartZ=0 EndX=2.525 EndY=8 EndZ=0
  constraints (10):
    c: Coincident(g0,g1)
    c: Coincident(g1,g2)
    c: Coincident(g2,g3)
    c: Coincident(g3,g0)
    c: Vertical(g0)
    c: Vertical(g2)
    c: Horizontal(g1)
    c: Coincident(g0,g-4)
    c: DistanceY(g-4,g0) = 1.9
    c: Coincident(g-3,g2)
FEATURE [PartDesign::Pocket] Pocket044
  BaseFeature = -> Pocket043
  Direction = (0,-1,2e-16)
  Length = 5
  Length2 = 5
  Profile = -> Sketch121
  ReferenceAxis = -> Sketch121 [N_Axis]
  Refine = true
  Suppressed = false
  Type = 1
FEATURE [PartDesign::Body] Body012  label="left bottom plate body"
  AllowCompound = false
  BaseFeature = -> Slice007_child1
  Group = -> [BaseFeature010,Sketch120,Pocket043,Sketch121,Pocket044]
  Origin = -> Origin012
  Tip = -> Pocket044
FEATURE [PartDesign::FeatureBase] BaseFeature011
  BaseFeature = -> Slice003_child0
  Suppressed = false
FEATURE [Sketcher::SketchObject] Sketch122
  ArcFitTolerance = 1e-06
  AttachmentSupport = -> [BaseFeature011]
  ExternalGeometry = -> [BaseFeature011]
  FullyConstrained = false
  MakeInternals = false
  MapMode = 5
  Placement = pos=(0,187.5,8.46e-14) rot=(0,0.707107,0.707107;3.14159rad)
  sketch-geometry (20):
    g0: LineSegment StartX=-237.3 StartY=-19.7324 StartZ=0 EndX=-121 EndY=-19.7324 EndZ=0
    g1: LineSegment StartX=-121 StartY=-19.7324 StartZ=0 EndX=-121 EndY=202.302 EndZ=0
    g2: LineSegment StartX=-121 StartY=202.302 StartZ=0 EndX=-120.9 EndY=202.302 EndZ=0
    g3: LineSegment StartX=-120.9 StartY=202.302 StartZ=0 EndX=-120.9 EndY=-7.21227 EndZ=0
    g4: LineSegment StartX=-120.9 StartY=-7.21227 StartZ=0 EndX=43.265 EndY=-7.21227 EndZ=0
    g5: GeomPoint [constr] X=43.265 Y=4.63 Z=0
    g6: GeomPoint [constr] X=38.1 Y=71.84 Z=0
    g7: GeomPoint [constr] X=38.1 Y=69.34 Z=0
    g8: GeomPoint [constr] X=38.1 Y=66.84 Z=0
    g9: LineSegment StartX=43.265 StartY=-7.21227 StartZ=0 EndX=43.265 EndY=69.34 EndZ=0
    g10: LineSegment StartX=43.265 StartY=69.34 StartZ=0 EndX=38.1 EndY=69.34 EndZ=0
    g11: LineSegment StartX=38.1 StartY=69.34 StartZ=0 EndX=38.1 EndY=130 EndZ=0
    g12: LineSegment StartX=38.1 StartY=130 StartZ=0 EndX=34.1 EndY=130 EndZ=0
    g13: LineSegment StartX=34.1 StartY=130 StartZ=0 EndX=34.1 EndY=193.303 EndZ=0
    g14: LineSegment StartX=34.1 StartY=193.303 StartZ=0 EndX=34.2 EndY=193.303 EndZ=0
    g15: LineSegment StartX=34.2 StartY=193.303 StartZ=0 EndX=34.2 EndY=130.1 EndZ=0
    g16: LineSegment StartX=34.2 StartY=130.1 StartZ=0 EndX=38.2 EndY=130.1 EndZ=0
    g17: LineSegment StartX=38.2 StartY=130.1 StartZ=0 EndX=38.2 EndY=69.44 EndZ=0
    g18: LineSegment StartX=38.2 StartY=69.44 StartZ=0 EndX=43.365 EndY=69.44 EndZ=0
    g19: LineSegment StartX=43.365 StartY=69.44 StartZ=0 EndX=43.365 EndY=-7.50023 EndZ=0
  constraints (46):
    c: Horizontal(g0)
    c: Coincident(g0,g1)
    c: Vertical(g1)
    c: Coincident(g1,g2)
    c: Horizontal(g2)
    c: Coincident(g2,g3)
    c: Vertical(g3)
    c: Coincident(g3,g4)
    c: Horizontal(g4)
    c: PointOnObject(g-3,g3)
    c: DistanceX(g2,g2) = 0.1
    c: Symmetric(g-4,g-4,g5)
    c: Symmetric(g-5,g-5,g6)
    c: PointOnObject(g8,g-6)
    c: Vertical(g6,g8)
    c: Symmetric(g8,g6,g7)
    c: Coincident(g4,g9)
    c: Coincident(g9,g10)
    c: Horizontal(g10)
    c: Coincident(g10,g11)
    c: Vertical(g11)
    c: PointOnObject(g5,g9)
    c: Vertical(g9)
    c: Coincident(g10,g7)
    c: Coincident(g11,g12)
    c: Coincident(g12,g-8)
    c: Coincident(g12,g13)
    c: Vertical(g13)
    c: Horizontal(g12)
    c: Coincident(g13,g14)
    c: Horizontal(g14)
    c: Coincident(g14,g15)
    c: Vertical(g15)
    c: Coincident(g15,g16)
    c: Coincident(g16,g17)
    c: Coincident(g17,g18)
    c: Horizontal(g18)
    c: Coincident(g18,g19)
    c: Vertical(g19)
    c: DistanceX(g14,g14) = 0.1
    c: Horizontal(g16)
    c: DistanceY(g12,g15) = 0.1
    c: DistanceX(g11,g16) = 0.1
    c: Vertical(g17)
    c: DistanceY(g7,g17) = 0.1
    c: DistanceX(g9,g18) = 0.1
FEATURE [PartDesign::Body] Body013  label="lone rear wall body"
  AllowCompound = false
  BaseFeature = -> Slice003_child0
  Group = -> [BaseFeature011,Sketch122]
  Origin = -> Origin013
  Tip = -> BaseFeature011
FEATURE [Part::Extrusion] Extrude009
  Base = -> Sketch122
  Dir = (0,1,-2e-16)
  DirMode = 2
  FaceMakerClass = Part::FaceMakerBullseye
  FaceMakerMode = 3
  LengthFwd = 20
  LengthRev = 20
  Solid = false
  Symmetric = false
FEATURE [Part::FeaturePython] Slice008  # WARN: FeaturePython — macro-defined, semantics opaque (R4)
  Base = -> BaseFeature011
  Mode = 1
  Tolerance = 0
  Tools = -> [Extrude009]
FEATURE [Part::FeaturePython] Slice008_child0  label="pcie"  # WARN: FeaturePython — macro-defined, semantics opaque (R4)
  Base = -> Slice008
  FilterType = 1
  Invert = false
  OverrideMaxVal = 0
  WindowFrom = 80
  WindowTo = 100
  items = 0
FEATURE [Part::FeaturePython] Slice008_child1  label="Slice008.1"  # WARN: FeaturePython — macro-defined, semantics opaque (R4)
  Base = -> Slice008
  FilterType = 1
  Invert = false
  OverrideMaxVal = 0
  WindowFrom = 80
  WindowTo = 100
  items = 1
FEATURE [Part::FeaturePython] Slice008_child2  label="middle"  # WARN: FeaturePython — macro-defined, semantics opaque (R4)
  Base = -> Slice008
  FilterType = 1
  Invert = false
  OverrideMaxVal = 0
  WindowFrom = 80
  WindowTo = 100
  items = 2
FEATURE [Part::FeaturePython] Slice008_child3  label="Slice008.3"  # WARN: FeaturePython — macro-defined, semantics opaque (R4)
  Base = -> Slice008
  FilterType = 1
  Invert = false
  OverrideMaxVal = 0
  WindowFrom = 80
  WindowTo = 100
  items = 3
FEATURE [Part::FeaturePython] Slice008_child4  label="psu"  # WARN: FeaturePython — macro-defined, semantics opaque (R4)
  Base = -> Slice008
  FilterType = 1
  Invert = false
  OverrideMaxVal = 0
  WindowFrom = 80
  WindowTo = 100
  items = 4
FEATURE [App::DocumentObjectGroup] GrExplode_Slice008  label="Exploded Slice008"
  Group = -> [Slice008_child0,Slice008_child1,Slice008_child2,Slice008_child3,Slice008_child4]
FEATURE [PartDesign::FeatureBase] BaseFeature012
  BaseFeature = -> Slice008_child0
  Suppressed = false
FEATURE [Sketcher::SketchObject] Sketch123
  ArcFitTolerance = 1e-06
  AttachmentSupport = -> [BaseFeature012]
  ExternalGeometry = -> [BaseFeature012]
  FullyConstrained = false
  MakeInternals = false
  MapMode = 5
  Placement = pos=(0,172.07,0) rot=(1,0,0;1.5708rad)
  sketch-geometry (3):
    g0: LineSegment StartX=-10.04 StartY=129.9 StartZ=0 EndX=-218.639 EndY=129.9 EndZ=0
    g1: LineSegment StartX=-218.639 StartY=129.9 StartZ=0 EndX=-218.639 EndY=130 EndZ=0
    g2: LineSegment StartX=-218.639 StartY=130 StartZ=0 EndX=-12.593 EndY=130 EndZ=0
  constraints (7):
    c: Horizontal(g0)
    c: Coincident(g0,g1)
    c: Coincident(g1,g2)
    c: Horizontal(g2)
    c: Vertical(g1)
    c: PointOnObject(g-3,g2)
    c: DistanceY(g1,g1) = 0.1
FEATURE [PartDesign::Body] Body014  label="rear wall pcie part body"
  AllowCompound = false
  BaseFeature = -> Slice008_child0
  Group = -> [BaseFeature012,Sketch123]
  Origin = -> Origin014
  Tip = -> BaseFeature012
FEATURE [Part::Extrusion] Extrude010
  Base = -> Sketch123
  Dir = (0,-1,2e-16)
  DirMode = 2
  FaceMakerClass = Part::FaceMakerBullseye
  FaceMakerMode = 3
  LengthFwd = 20
  LengthRev = 20
  Solid = false
  Symmetric = false
FEATURE [Part::FeaturePython] Slice009  # WARN: FeaturePython — macro-defined, semantics opaque (R4)
  Base = -> BaseFeature012
  Mode = 1
  Tolerance = 0
  Tools = -> [Extrude010]
FEATURE [Part::FeaturePython] Slice009_child0  label="Slice009.0"  # WARN: FeaturePython — macro-defined, semantics opaque (R4)
  Base = -> Slice009
  FilterType = 1
  Invert = false
  OverrideMaxVal = 0
  WindowFrom = 80
  WindowTo = 100
  items = 0
FEATURE [Part::FeaturePython] Slice009_child1  label="Slice009.1"  # WARN: FeaturePython — macro-defined, semantics opaque (R4)
  Base = -> Slice009
  FilterType = 1
  Invert = false
  OverrideMaxVal = 0
  WindowFrom = 80
  WindowTo = 100
  items = 1
FEATURE [Part::FeaturePython] Slice009_child2  label="Slice009.2"  # WARN: FeaturePython — macro-defined, semantics opaque (R4)
  Base = -> Slice009
  FilterType = 1
  Invert = false
  OverrideMaxVal = 0
  WindowFrom = 80
  WindowTo = 100
  items = 2
FEATURE [App::DocumentObjectGroup] GrExplode_Slice009  label="Exploded Slice009"
  Group = -> [Slice009_child0,Slice009_child1,Slice009_child2]
FEATURE [PartDesign::FeatureBase] BaseFeature013
  BaseFeature = -> Slice008_child2
  Suppressed = false
FEATURE [Sketcher::SketchObject] Sketch124
  ArcFitTolerance = 1e-06
  AttachmentSupport = -> [BaseFeature013]
  ExternalGeometry = -> [BaseFeature013]
  FullyConstrained = true
  MakeInternals = false
  MapMode = 5
  Placement = pos=(0,4.9e-15,22.13) rot=(0,0,1;0rad)
  sketch-geometry (4):
    g0: LineSegment StartX=-41.13 StartY=176.07 StartZ=0 EndX=-41.13 EndY=172.07 EndZ=0
    g1: LineSegment StartX=-41.13 StartY=172.07 StartZ=0 EndX=117.88 EndY=172.07 EndZ=0
    g2: LineSegment StartX=117.88 StartY=172.07 StartZ=0 EndX=117.88 EndY=176.07 EndZ=0
    g3: LineSegment StartX=117.88 StartY=176.07 StartZ=0 EndX=-41.13 EndY=176.07 EndZ=0
  constraints (10):
    c: Coincident(g0,g1)
    c: Coincident(g1,g2)
    c: Coincident(g2,g3)
    c: Coincident(g3,g0)
    c: Vertical(g0)
    c: Vertical(g2)
    c: Horizontal(g1)
    c: Horizontal(g3)
    c: Coincident(g-3,g2)
    c: Coincident(g0,g-4)
FEATURE [PartDesign::Pocket] Pocket045
  BaseFeature = -> BaseFeature013
  Direction = (0,0,-1)
  Length = 4.5
  Length2 = 5
  Profile = -> Sketch124
  ReferenceAxis = -> Sketch124 [N_Axis]
  Refine = true
  Suppressed = false
  Type = 0
FEATURE [Sketcher::SketchObject] Sketch125
  ArcFitTolerance = 1e-06
  AttachmentSupport = -> [Pocket045]
  ExternalGeometry = -> [Pocket045]
  FullyConstrained = true
  MakeInternals = false
  MapMode = 5
  Placement = pos=(0,1.48e-14,66.84) rot=(1,0,0;3.14159rad)
  sketch-geometry (4):
    g0: LineSegment StartX=117.88 StartY=-172.07 StartZ=0 EndX=-41.13 EndY=-172.07 EndZ=0
    g1: LineSegment StartX=-41.13 StartY=-172.07 StartZ=0 EndX=-41.13 EndY=-176.07 EndZ=0
    g2: LineSegment StartX=-41.13 StartY=-176.07 StartZ=0 EndX=117.88 EndY=-176.07 EndZ=0
    g3: LineSegment StartX=117.88 StartY=-176.07 StartZ=0 EndX=117.88 EndY=-172.07 EndZ=0
  constraints (10):
    c: Coincident(g0,g1)
    c: Coincident(g1,g2)
    c: Coincident(g2,g3)
    c: Coincident(g3,g0)
    c: Horizontal(g0)
    c: Horizontal(g2)
    c: Vertical(g1)
    c: Vertical(g3)
    c: Coincident(g2,g-4)
    c: Coincident(g0,g-3)
FEATURE [PartDesign::Pad] Pad027
  BaseFeature = -> Pocket045
  Direction = (0,0,-1)
  Length = 4.5
  Length2 = 10
  Profile = -> Sketch125
  ReferenceAxis = -> Sketch125 [N_Axis]
  Refine = true
  Suppressed = false
  Type = 0
FEATURE [PartDesign::Body] Body015
  AllowCompound = false
  BaseFeature = -> Slice008_child2
  Group = -> [BaseFeature013,Sketch124,Pocket045,Sketch125,Pad027]
  Origin = -> Origin015
  Tip = -> Pad027
note: 6 file-system paths scrubbed to <path> (originals preserved in the JSON sidecar)
